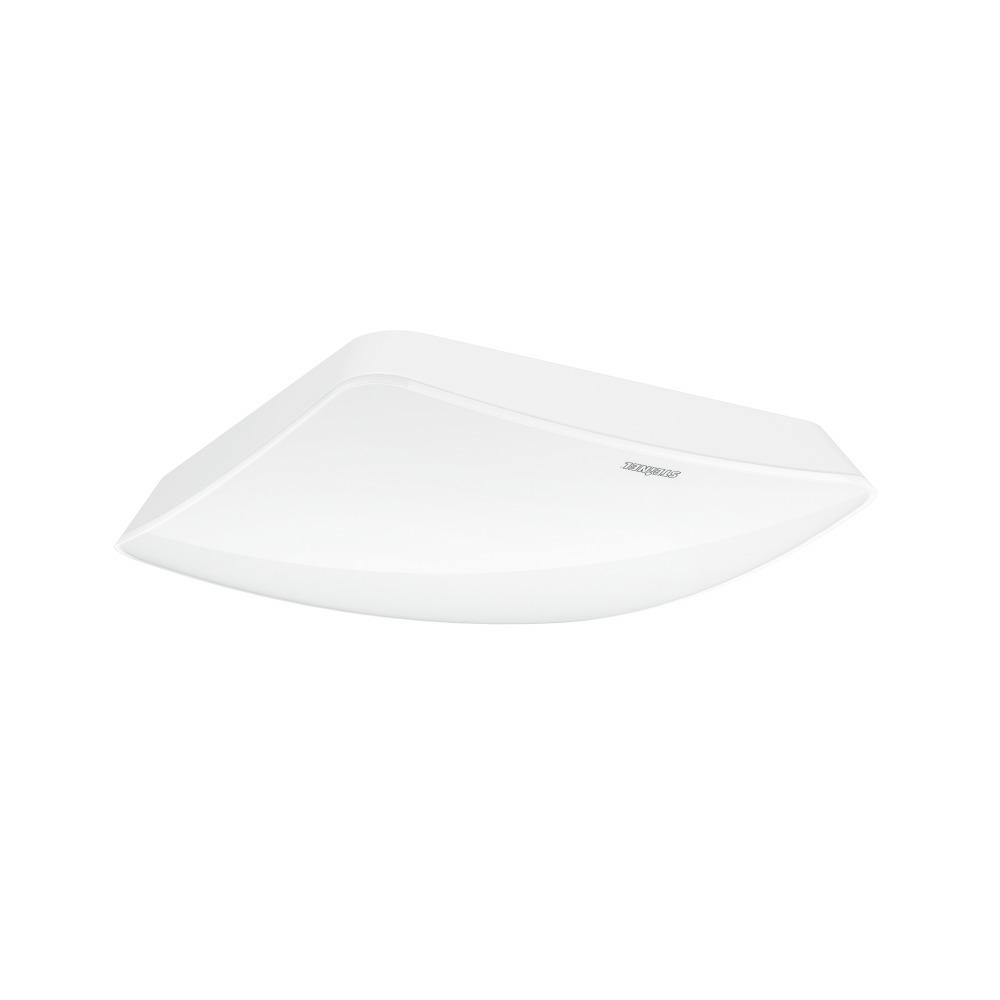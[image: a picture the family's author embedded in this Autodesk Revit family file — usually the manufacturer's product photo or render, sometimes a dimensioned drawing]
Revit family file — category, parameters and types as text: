
# Revit family: truepresence_057947
name_source: partatom
category: Electrical Fixtures
revit_build: Autodesk Revit 2016 (Build: 20151007_0715(x64)
units: mm (PartAtom-declared; Revit-internal decimal feet)

## family parameters
Cut with Voids When Loaded = No
Host = Face
Maintain Annotation Orientation = No
Part Type = Normal
Room Calculation Point = No
Round Connector Dimension = Use Diameter
Shared = No

## types (1)
- True Presence
    Apparent Load = 0 VA
    Default Elevation = 1800 mm
    Description = Type: Presence detector; Dimensions (L x W x H): 50 x 103 x 103 mm; Mains power supply: 220 – 240 V / 50 – 60 Hz; Power consumption: 1 W; Sensor Technology: High frequency; Application, place: Indoors; Application, room: classroom, lecture hall, one-person office, open-plan office, high-bay warehouse, production facilities, conference room / meeting room, hotel room, care room, duty room, recreation room, dining hall / staff restaurant, changing room, kitchenette, sports hall, reception / lobby, WC / washroom, warehouse, Indoors; Installation site: ceiling; Installation: Concealed wiring; HF-system: 7,2 GHz; Electronic scalability: Yes; Mechanical scalability: No; Mounting height: 2 – 12 m; Optimum mounting height: 2,8 m; Detection angle: 360 °; Angle of aperture: 360 °; Sneak-by guard: Yes; Capability of masking out individual segments: No; Reach, radial: Ø 15 m (177 m²); Reach, tangential: Ø 15 m (177 m²); Reach, presence: Ø 15 m (177 m²); True Presence reach: Ø 9 m (64 m²); Twilight setting TEACH: Yes; Twilight setting: 2 – 1000 lx; Time setting: 30 sec – 30 min; Switching output 1, resistive: 2000 W; Switching output 1, number of LEDs / fluorescent lamps: 8 pcs.; Switching output 1, floating: No; Switching output 2, resistive: 230 W; Switching output 2, floating: Yes; Constant-lighting control: No; Basic light level function: No; Functions: Group parameterisation, Semi-/fully automatic, Lighting scenario, Manual ON / ON-OFF, Neighbouring-group function, Normal / test mode; Settings via: Bluetooth; With remote control: No; Interconnection: Yes; IP-rating: IP20; Material: Plastic; Ambient temperature: -20 – 50 °C; Colour: white; Colour, RAL: 9003; Manufacturer's Warranty: 5 years; Version: COM2 - Concealed wiring; PU1, EAN: 4007841057947
    Height = 0 mm  [stored 0 ft]
    Length = 200 mm
    Manufacturer = Steinel
    ModVariant = No
    Model = 057947
    Number of Poles = 1
    OnlyDefault = No
    Power Factor = 1
    Product Name = True Presence
    Product group = Presence detector
    ProductGroupID = 4
    RLX_Detail_Level = 1
    RLX_LegendID = 5.1
    RlxData = Q
eAHUvXeUVNW7rtuAICAioiiCICINSM6hq1YVOWdQSUKD5JxDEyRIzjlKTgYEFFDsqi5EzAqI
OWPO6acoRs73zHrnPrXHPfeO+88Z4xzGfvp9v7e+NddccwW6W/Zv5Uq7fDnN/lz+1wnW/cnv
jell++PLWzt4l9yG7TxpabOiRsI63Be34eXLX+e5Pq3p6JH9h47qN2Ho6FHtJo40N3TcwPz5
8rLpjd3SxqVNTBuYViatk7mBaeONUWn3uKRiWo20umn10xqm1bGvZdJuT2tkozfQHFInmcey
y5e/y1Mord3QwUMmNB85dMKEgePSyuRiHwXHpfVLG5DW97+NxkgN/5cj5baRvs5zRVr7geOH
5CrsRnD7zfhfdOdKu0LpT3bw/3/+/O/pu9btevSYtLQT5kblSkt7sGTb4M2JFYNres+IPfJc
+yBP8f3hVdWmxa6JNgvy/5URzBkyO3bLu8WDtAcLBZ+NWBnbsf2b8Jjpd4Xe+2RTrPWST8Jd
ap0MN3hlc+zuVtvD/Rp0Du+ptDNWoPyU8MuzJ4Ue3bI7VrfevHDZnz4PTcm/O/bzbx2CudXb
ZDSvmxVberxDMDXXdbHqw7Jiyz5oH+R03RHbePM0v684+/rA5vb2xIrxL3rN8POJMx/tN5ay
3xj71b6y2ZfmkM0cut8zJpyWdqFcwbd2x76MhLJfHf96Rt6Xkz6t4blY3YxNsXfDj8UuNW8f
H7toQqxho5viN990dTxfh5WxvlUrxsefbhOvv2YSc4jbmrg5vPhZg3ixm5rHf7phWmxSv9Xh
gYfax0vVnhB7bGi9oPTyFvEGP0+N9alaMehv2zazbasNuRgqOrZDvNba8bGVdQtkP7q5Q/zS
2PGx1X99Gtv22VOxm/Zsjr25ZUesY+SOWKEiO2PXfj0vNqjXd9nP/70r9snDU2LHPpuZvWmD
O5bY7HV50jkW5SFy9Yfo1zhhxuF4OWeVeq33+wqzLx1jwDFu/ntVbM3h9kF6rQn+GN15t/nH
u55uE3Sy+U9fVy/ecVKL4K88WbEHC/6S/e3YDsHsNeNjJYdeE+q/uUMQHjc+1nXA0XCJJu2D
LUsnsG7BJNu2jm377BsNghVlmwezrpkWs+stbtdbXNdb3K63GNebXQ9xux7CXA+cE66xL57a
GnvP+u0aCL60a8Cun7hdP09y/dg1E7drJsw189dP7eIzHt0f7ll0eOzfJ9vG3zi6L3y4a9dY
rnlt4tUe3xvOuy4UG/RHu/i+LadvI7/vqbbOk1//dZv4uBYfxsjvOto6Hvz6foz83n9b2Tjl
4+QPv9zSxkmPk387uml86t56Ll/aokl81Yq6LifjM/rJ+Ix+xmAscsZgLHL2yb7J2Sf7Jh9d
NM9u5kqOZ67qD6f0h32/jR+kjB/48W0+Qcp8Aj8fy4KU+Qd+/jZGkHK8gT9e22eQsj6BXx+b
YxCbsGYP87Q5Bt0bHt3DPNXv1t/mSL9bf40f0G9zZPyAfs3H5TZH5uNyzd/lZHxGv47X5YzB
WCnr43L2yb7JbQ3LMVf2W/Ct28oxV/W7uZJr/f34nC8/PufL5Tq/Ltf5dTlrzFwZhzX28/9k
c4v48hPlAttn7N2Hm8Rv+rSm861qdnDXHtfq+VLt4vs3fhTDd63Rxq7hCnF8m03N4v2y6zuP
UpPzOX14tmN7PNcJ4yoP+9z6A99v4wR+HNPAj2+fB36/tl3g52PjufPLmMrd/aX+gFzjOK/x
ndd+nbfxmI/z3H+Mq3m6cfE6LpfreJ1nvoxLT7uGGfEVm8NuDb9+qHr81MtNnbc1jv+yuYXz
78zeHvuhb2vnq0zunFF0URvnL258MDwhlMwX2DkJq/+tj2oGjz3SxPV8uCIcnGmW4XzBc02D
s3uqO/+P9a7QebwUbhVkHP02zDktMr11ML/uBuc/WNgmeKBa7yfJv+rXOnh7yHautdixhq2C
yvO+c77GipbB9DcLxMkr1WsZvHfiOuf/k79lcPDR4s7X+E+L4PcaJZ3/450WwWfvlnL+a5sD
x8m2J6Y3CS41qOX80kYZwRtrws7f+WX14NThps5z3X1s1x/9E2/5Ovxmy1bO3z9+VXjx8tbO
ZxS5Nvt2ez7SUyw4HOtSIZnb+sSbatvBsZrxwqeauJ6nh4bjy0ZmOH/piabxwm9Wd/775HXu
/Hc9W8UXLvnMHe8/+1rHP5+7yPmp09rE830zJ8S+Fv7VKj7ln+ww/us/5sfGFV7wX77/owtd
/7vhBeFBHy34L+97+ObFvmVJyy3wfEcHeL7HwqN5BT6fwF8pj/KdIdsVMPgM8AXl0avk0UIC
f7U8Wlj+GlM/Dr6IapT9AZ7vwvBoUXGdMnL89QJPDzXKNni0mMAzLjXKvoH5+h78DarRGwW+
uDx6k8CXMPicbUsKPMdLjd4sSikjL22wHeBvMdhfGcPPB3+rarSsPOqPHX+barScSFdGH768
arSCPFpR4G+XRyvJo5UFvoo8WlXgqymvburHxNdQjdaUR7kGAV9LHq0tuH59D9epHxPPtUqN
+nXA51eNco3UMeoa/nzh/TnF11ONlhH4+vIo6w541hrwrDXg/ZrjWWvAs9aAZ30Bz/oCnv3h
UdYX8PxkhkdZX+bLz1h8BvwExWdoSJ4ab9/Iu8/QQOAj8ig/YgG+kTzaWOCbyKNNBb6ZPNpc
4FvIoy0FvpU82lrg28ijbQW+nTzaXuA7yKMdBb6TPNpZ4LvIo10Fvps8eofA3ymP3iXw3eXR
HgLfUx7tJfC95dG7Bb6PPNpX4DPl0X4C318evUfgB8ijAwV+kDw6WOCHyKNDBX6YPDpc4EfI
oyMFfpQ8Olrgx8ijYwV+nDw63uBa5drlGgX8BHmUaxTwXJd8zjVPDXjuAzw6UeDryKOTBH6y
PMq1C3iuVz6/STUZvoRqdIrAF5dHpwp8ljzKNQ14rmM+v0E1GZ4c8NMEnuc/NVpaHuW6B3xJ
eZTrHvDT5dEZAs/fN9TozQa9eN9HNlPgC8uj9wo8f39To7MEfrY8eqfAdzf4nO8BqAFfUB6d
I/AF5NFc8uhcgecPNX/uE/h58mgfgc80+JPboAY8f7/g0fkCX0seXSDwC+VR7jHAc1/xOX9/
UQOeHPCLBL6GPMrfi3yGDhH4yvLoMIFfLI8uEfiq8mg1g1687yNbKvBV5NFlAt9AHuW+Bfw4
g/t2uTFW4Ln30RXy1PiR0pXy1Pjh0lXy1Pih0tXy1Pg1qlH/HMOvVY0OFPh18qh/TuLXq0b7
CfwGebSvwG+URzfJo3cL/GZ5tJfAb5FHt8qjPQT+fnl0mzx6l8Bvl0d3iJ3K6MPvUo3uFnuU
0YO/Q7pXnhrfVbpPnhrfWbpfnhp/QDXaUeAfkEfbC/yD8uhD8mhbgX9YHm0t8Afl0ZYC/4g8
2lzgD8mjTQX+sDx6RB5tLPCPyqNRgX9MHg0E/qg8yr0B+HHGGGOUsUzglyobIU+NXyIdJs/9
z/NikZFpzDPmGzxn+hsLBJ4czZTnedfbuE/g5xrdjdnGHIOsp0EOeHKUPjzP7m7GLIG/10C7
yFPjZ0o7yVPjZ0g7yLczbWNMM5oZk40pRiujhTFV4MlR+vARY4Ix0WhiNDImCTw5Sh/+qHHM
4FwAfqU8Ol7glwv8CoNtOb9sA/jj8ujjAs81TY1yrdP7qMFngOfawqOHDa7HR+Sp8VzTePRh
edSPg+c+oUb9/rjv/HzwPEeoUZ4v3K88N/gM8NvkUfr2GbsNegG/Sx7l+UIPzwo+A/weg892
GH5bPPtg3zz3/NzwT6hG/driV6tGVxn08vzkM8DznMWjG+XRtQK/QR5dL9Ypo2+NwRiA9/vj
vDOf14zUP6eeacnllJZz/bTELw/XiqStqpw9pOj0RLPRlSIvTqwcCw+bnrglLY/rmf35jES5
h88F55dVzn7swZmJvpWfDF6vVTlW9PuZiW8mpkeeXFk5e+2u6Ymp09JdP/7XtZUi53amhRnn
pkdtfPvD+P98Vj8yaulDoT1vTEuU+CN3ZN2KytmM/0z8XEAP46/qnB0cWFo5xPiVDu1w+R91
701c9595zh8af2+C3uSf5H8x9D671LLYqnW149HH7018u6l09oYtO+JsW+yefg3rFPwt3j19
ZuLzMz9m31W4eM6DFWYkvsz3b+ixNuk5zPlM2YoNhzxTKYc5F3q1dHjK8Fo5zHnW1zeGns0I
ckpumJb4q/Ct2Y+cTPb802ZfdrUjST8yq0b2OzOa5Jy9c1qiYfOy2bufapnD2n689frsz/O0
z/n2XFbi9NRS2Uf/uejmsLFcx4b5DyXn1nbP3PDTfeu6OV937UPh8r9Wcf7tNX3ChU82CDiW
2Y8/FX7g9NSAY+/75ZHQinY7gpTjCjguHUuEY3nzpcOhJY9UinAsNxwoHxows0mEuT1wYmeo
Q9UgwrFkF08PdZ2U7vo35jv7xGQ7f2yr43Lbak2c/7rt1bE6WbUirMnrX/SPvXpr0o/Z0zD0
0qWLbg6T/t6TndkzObd9r0yINRs8x835iVe/zj7+RMQdy9FnWub8dHptQ7c++2vl9M0eG2LM
4EitnNE9l2bgz80umvPkxtrhl3rMSKwvUTznruFnQpyvUQOy4w9/d2UG10bT5jviA3s/EWId
3li5I35mWHPn9zyyIz6i3NkT5OrJTulxfk337Hj3tQXcNXbXLWVyrtu3Jjv9nemJostuzPlq
1eAY+2p/uFbOxRdedPPJfKt+zo/9Pszmuv0pX/uc5fvrZ3BOGxnV0q8IDg9qE6mxICtxpnih
YOr+jpEv92YlRpaeE07xMecHZyU+a5g33qVll8gfp4clrt+wO6dUkwmR5u9XS4zZWC3R7Oy8
yORX9uQ8snxYgnzvmeviT/TNStB/rtSO2MqdWQnGaVl6aXj5nqQv/XPuoOTQZM/UJ3dF2nyb
3HbD/GrRYj8kxzy/Y1g0/6A9bl/LB2RFf+t7lZvDzbuzoteVXu/mduO+rOiah2e5ObcdlhXt
diAtYL93vDMsWqDs7gjz+fRytWh8QrUo81z97+7Id48Oi5IfOXB10OKerCj9u1fsDHfbmRVl
nqMfXhw7tSfp699YIP7qwGTPykW7c7o9l9z24/7VEoeure7G7Lh0WOL3d/e4fa05Mj7x/Fer
IllFvggu98hKfPrcvvArX3SL/LtoUqLGiinh9w8tijxddFri5yF/h3ienS+elbh0cWhsd7me
kbxVJiVCG+fE+jdbGmmwflqia7vLsV+2ZER+WZqVqNEvV5y5nf9rROLr0NGct3dcHVl8tmKi
7FNVErfsfSDy0ydVE+/OqZrofOvKyPz5+3Muvj488fW8uyJllxaJn35xWuLoHXUjaRcuxmqt
TK7/4T/Wxs6dmJIYsX9spP3vq2N3XzPZncdGleeEnvgl2X9k1dzQmYPJ/m8aLA1vLTYlsfWa
6ZHnP/44/MXaZL4lM1/QZXHSh79fE7lm3kg35jM/fx/+7efpidKflYgUmXJ/5P6v+iVmhI5H
rhuZHi30c8Q9dy98USlasWPlRK5S+yON3xsRff2L5HFdc2hatEDmVfF/LtWPvHF4UrTmiodi
4YELIyuDCdGLpdbHLpTcFDlUdFp018G0GGv4zU1Z0Ycm3hlmDVtUmRSdb9cDa3h03bRof7se
WMMuy7Kid5pnDRsXHxktse+xCGv44dcVowP2V4myhiVurhad2bpqlDV8qdH+yPNPDo8y5tBv
iwTLXpwWZQ1PdP49/NaK5LUxoMmG8OQTU6Ks4fFmm8JDCk9218NN/WZm5/yS7K+/dlr2uweT
/SdWLY69XWxKlDW8csyFWMN1yfzU/rzxY4uT/o4X1+TMWDzSjTny3Nex7/8zPcoa3nLP/TkN
H+4fLTDl0Ui4bfnEsg1BtHrhGpH46UqJ6mMrR1nDHTkjEjOmH3PHdXJBJJF/1Q3R5gV2Rd7N
qp04/mPtaIeCvwVHv70yUfrHltF6/Q5Ebh2wP+fCt2OiXx0/HPzYYnLOn63HRp8eMyIy/eu/
Y7lWTo3O+bdfZEn9GbEr8s1wcxg8NhKbFM2Kcl3d+NzicMWrpkVZ/+ub7g7//tL0aK8aZSI3
1CkYHHx9avTvU70jS19eHlnVfpQ7loo99ke23TE6yppPnXZD9PmNETe3VTfVib7bKTm3Xq+2
jGY/eqU7F9vzj40OvnF/pE3fh4LOM8ZGf75lQoS5fXMoK9rdzmOTK9tHSrTLin574Vt3fz3X
YEZ0s533F9cXi3RqlBU9u6pymHnOKjQtuvbhWe46OZPbjsOeG6ynnhXueVL9wazon/ZsYcwN
C7Kil8xznQyabfu68Qbn7TvvqP/bu3cfu5Ys57mx+MmR0VxrV+dwDZz5aFR0aMH9OYz/1bpI
9I45Nyay6m+L9NxRO9ryxdoJ1v+tr/NH75/X0l3zv2/dF5n275hE/cLHg8tPT4nMrDk2wTHm
e6ZAUPShrATzmZ/7vfCg8cnn5Nc7V4W7dZyRyP6xaGTJiPTw/PlTE49sGRApm39VrPZL0xLc
L+MOrYm9sCH5fU3dn/LHK/05NcE1/GDmspwX5o5y9+YjJ/fnDOk9OpHvj4KR0S8US5wvF01w
nVT+tXai/6TkPLs2bJnYcTF/guuk/3tjEjMG789hntszxibq1JuSwzwHjMtKNF37UYx1eGDW
jMQNh+36tvMbOzUlUTeaN8aaLK8wPfH89LlhrtV1z05NnD16MPxzZl/3vZW+/4nmMpPbyGNc
YeQ18okrTfOLAqYFjauMQsbVRmHjGqOIuNa0qLjOFK43ihk3GDcaxY2bjBJGSeNmo5RR2rhF
lDG91Shr3Gb4MRkfyhnpRnmjglHRuN2oZFQ2qoiqptWM6kYNo6ZRy6ht1DHqGoxXz6hvNDAa
GhlGyAgLvolk0bgIGxmNjSZGU4OfyZobLURL01aitSm0EW1NoZ1obwodREdT6CQ6m0IX0dUU
uok7TOFOcZcpdBc9TKGn6GUKvcXdptBH9DWFTNHPFPqLe0wHGAONQYY/vsHmhxhDjWHGcMMf
IzrCGGmMMkYbHK8/VnSMMdYYZ4w3JhgTjUlisilrMMWYamQZ04zpxgxjppG6DqzHvcYsY7Yx
x5hr3GfMM+Ybfk3QBcZCY5Gx2GB9/NqgS4ylxjJjubHCWGmsEqtNM401xlpjnbHe2GBsNDYZ
rB1sNrYYW437jW1GprHd2GHsNHYZu409Bvvfa+wz9hsHjAeMB42HDM7vw8ZB4xHjkHHYOGI8
ajwmjpoeM46Lx02fME4YTxrZRsyIGzkG650wThpPGaeMp43TxjMG5+1Z4znjeeMF40XjJeNl
o60x3HjFOGOcNc4ZrxotjVaGv664xiDT4FpMvUbxHCOkXtt4zjn4+4F7A5h7J6O9wbUG+DYG
8wL8+f+LqZfLnoG57RofNinj6kXZQVqhjQ1XXr8qyDxaOfTGi6eD50d1D9+282BwoMtj4X+u
6x28PSo7/En3DcGUw/+GoxNmBzdfLBKcT+sTHO1TKKjaa3hgS5G29qnOQdqBaQ3GvX97kLZi
WcNin/4drr+8QYTtTx/pEKHeMbZxpPxnc8OMj7L/SwuLh8vm7hBBn2zdLjL64tYQ+7s97wdh
9vd+2xLBjLLVI2jz7EoRv9/K79R081hQOxr89HHRoIr9G8CsQz2DD8N3OM357eXwo23XBg8/
s79h2VuOBpP+mRNevCY7uMP2+c3mFwL2s+uHp4NyVxUPzXw2b/DKoUENOX7yw1tOh0qXzBUq
UrFkmP7H29SwcSo0WLH6Lnes9abtCE61ey+8cu+KoHanm4L+lxYGP19bM7i0en5Q76FIsHbB
PDcf6rKL+rjPh5QdETzSrniE+fWaXjBCfTr9ykjn32e7/NFfdwafTPwn+PvZDcFvr34dnH33
YJDrr/yRN8qfCard+XrAeVl+9ydB94MvB0Uqvhe8Nf/FoP3O6yJ15p0JZk8pFamy+Uxw/tma
kdu/fyVgnTl/V7VoHqG/x6jWkWs/eiFgfRnnyOL6Ec4n68r5/OhC5Qjnsd/n5wLOw4aVZ4Nx
N/wWZr+sB/Nh/XIVPxt8cdd4N0+O/3itXMnza8fBOnBcrEORQ1dFWIdTdQrZvDoEB5dsCbgO
WC+Ol/XjOG9854wbj/PD8bJ/rsfHr3rFKeeJ+S69dCZ4ZlzboOT8s8HgfiuCP6tUj7ySb1Po
q+I1IrtvOxF6uVHzSKvTa0Pj/qgeKb3/q9C/71SPtC9WKPxq2ZKuRqkfO/ZvwOfrC1wOqEt9
+4mrfx7yqat3/fKuq/8z7T1Xv7vidVfvL/uGq39rfsppyzOnXP7ym086vdT9SZfXLbTd1V2e
2ObqpZc6uBplf72PJMLs/6u0p8LU+Qvf6uoDf5dzdeaeUyE+bzTjpRCfnzzbwNWZt7d1dfmJ
yf1P+ie5/7/yZrvxKyxM7n9gKLn/OV8m9//dnR3d5yjj3TzqZHJ/8eT+Zy0o6+qKk8q7/Xfa
8ExyfzefSe7/WCRZX9PZ1bu2tnLrOPTTVm5dH/6ymdNTB5q5PDN3fVePfrtesi8juf5DTdn/
p58l1//ZBsn1b1fiUze/MhuT6/9q2fdcXfah5Pq/fCK5/m91Tq7/AwuS+z//UnL/jbo0i9i/
4wpnb2nptFGXcpHQg5tDnG+ui9+7l4iU/ndz6PpoPne9nOv3b0D+UIFPAq6XViM/cfV1g951
+ulzbwcVdiwK3fTiC67m+qPmOcH19vkTrzk9+/tr7vM3ez3tlOfK1tq7Qju6Zbv6zoHbnfL8
iZTdF+L8s1+eH+NGHgjxPFlx0wH33Pmy1P7QuX45YT7PvKWUU547jMdzKK3LllCnW54Muc/t
+cR8Ms+kuzrvkuT+697+jJvnyC+z3XGdm5ucR6sVyXk8l1jh5r3v+gkB68P1wHj3VW8XsD4/
rfg9zPGtLJ1w+780rWSY9bmwsbSrx+TE3P7GvLfL7b9Lv3ZufXmeMB+eL4d6bgplVr8t5NTm
yfirK7R2fTyHOJ715Zu7ukuV+k55XrE+XB/08xxjfXiusT48/1ifU0uS523K1uT54jnIeDwH
WZ8m65Lnj+cV87lc/nV3fBuLJvd/+OPWbp5L27Rx18m4O94JuG5KbvvQ6cVinzmd3OZK93mZ
Qjcnr6elNZw2GJy8zo4eTl5nX/ROjjPL5so4F7b/4/T5AZX4t4Th5/991Gm9J/O4cU881yW5
v/krnB54aZfTk+sedrpg8RGn315x1Gms2TGn8zYdd9q14JNOQ8+ddPrIxWecZp7Z6/a78tgl
pw2K3e72W/Hlo067Ncvn+u4p0t3pr8vXOL3tvRNOb+2RHG/+keR4ra9NrssvPZLr8swXn7q+
tLL/OB3+cwG3HgNCtzjNt7uW0xv+eim4t/36YHF4UbCp6KIg7aUXg18eOhGwn3NbXgwOvfZ8
8E3kZGD//jZYtvWZ4J8uiaBwrReC6+IvB1l/93HbjQ0KBiu7XxW021cwYL6ji87NYP6/1t+Z
8UeHl4N1rxcIxj78UnBm7xNhxn9hbIXw5V4v8PdUiPm/uWRniOOpMCgIsd9yGy5ncLwDuz6S
wXq89s4LGWnN385Y/djh8MlVj2U888I/YdaLvlkF/sgoP2Z4eFbwfUb1JYvCrOfArtVCO47k
DbGftKdzhRpcahLOHJ8Wum9b+zDrfqHqytCsT1qGChf7NHSy5b8ZBe+/K2zf92T0vb2tOw7W
4fCRtsGta14Obu+9ImCN0nYfyhhbclnAPN5tsCtgfNaJebBOF76uFVpeOhGcnLAmdHTs6SDt
r69C9+55PhjQ/5dwr29te/tj37q5n7nt2zfn85gC+RXyaF6BzyfwV8qj+Q22K2DwGeALyqNX
GYWMq43CxjUGWRHV15oWNcivM/w4+OsNti1m3GCwT7Ib5dHi4iZl9OBLCDw91Cjb4NGSAs+4
1Cj7Bubke/A3q0ZLCXxpefQWgS9j8Dnb3irwZeXR20Q5ZfSlG2wH+PIG+6tg+PngK6pGb5dH
/bHjK6lGK4sqyujDVzWqGdWNGvJoTYGvJY/WlkfrCHxdebSewNdX3sDUj4lvqBrNkEdDAh+W
R7mAIaKMvqjhx8Q3Uo1yTIBvbHC8XLNcI02MpkYzgW8u8C3k0ZYC30oebS3wbQSen/EA385g
3fkZkLUGPGsO+A4Ga0w/69vRIO8kj3Y2WGPm0EV1V9NuBvO9w+AzuNOg5y6ju9FD4HvKo70E
vrc8erfA95FH+wp8pjzaT+D7y6P3CPwAeXSgMcgYbAyRR4cK/DB5dLjAj5BHRwr8KHl0tMCP
kUfHCvw4eXS8wE+QRycak4zJxhR5dKrAZ8mj0wR+ujw6Q+BnyqP3CvwseXS2wM+RR+cK/H3y
6DxjvrHAWCiPLhL4xfLoEoFfKo8uE/jl8ugKgV8pj64S+NXy6BqBXyuPrjPWGxuMjfLoJoNr
dbPRXeC3yKM9BZ7rks+3GtSAv18e3Sbw2+XRHQK/Ux7NFHiuVz7fZVDvNvYYe1XvM91vHFD2
gDz6oMA/JI8OEfhhBp8/bFADnhzwBwX+EXn0kDw6QuAPy6OjBP6IPPqowD8mjx416MX7PrJj
An9cHn3ceMI4YTwpj2YLfEwenSLwWQafxw1qwOfIowmBPymPPiWPnhL4p+XR0wL/jDw6S+C5
f/j8WYP6OeN54wXVL5q+ZLys7BV59IzAn5VHuccAv9jg83OqyfDkgH9V4M/Lo6/Jo0sF/nV5
dLnAvyGPvinwb8mjbxv04n0f2TsC/648+p7xvvGB0UMe3SDwG41NxocG9/Q64yNjjfSCPDV+
lfRjeWr8Cukn8tT4ZdJP5anxn6lGlwj85/LoIoH/Qh6dL/BfGvOMr4y5Av+1PDpb4L+RR7+V
R+8V+O/k0RkC/708+oM8Ok3gf5RHf5JHpwr8z/Lof8QvyujD/6oavSh+U0YPfpL0d/mJppeM
8dI/5KnxY6V/ylPj/1KNjhb4v+XRkQL/jzz6rzw6XOAvy6NDBZ4fNKjRQSaAz2UMNJvb9B5T
wOdRjfazDPBXqEbzyqN97XPA51ON3m0Z4K9UjfayDPD5VaM9LAM898haY7XxnsC/o2ylPDX+
TSn3N577n+fFqwbPrGeMlwyeMwuMMwL/snGfQR89s4yZxmmBP2VkGTEjYZBNN8gBT47Sh59i
TDayBf4JY4Ixznhc4I8pGyNPjX9UOkp+hOkw46DR39hp7DeGGIONBwX+gDHAoI+e3sYWY5uR
afQxdgg8OUofvoCdh4LGVQJfSB69WuDtfwTDgb/GYNsiBtsA/lp5tKjAXyePXm/QW8zgM8Df
II/eaBQ3bpKnxpdQjZaUR/04+JtVo35/pcz7+eBLq0ZvMcoYtxp8Bviy8ih9txnlDHoBny6P
ljfoqWDwGeArGnx2u+G3xbMP9l3J8HPDV1aN+rXFV1GNVjXorWbwGeCry6M15NGaAl9LHq0t
6iijr67hx8T7/XHemQ9/JO5esbvpv/6twv/8LPnvQnK77uT3Jr4vj7ZPfjYrivos5PqT411h
ns+uVEaPz/CMR53X8J+R4X0WNu/78pnz/WT0+CygTeOxPz67hsgyenyGJ6POb1A3Mnyfz6LK
WKcCBv1PKmMOPqOfbakLGtQnDDL6fMbnZNRXGdQ8W3yfz/icjLqQ4ft9n8+upk19ePqPE1lG
j8/wZNSFDeojhu/zWZmUjHWj/yZlHIfP6Gdb6iIGdXGDjD6f+bVn3ch8P33U1yq/0ZSMPp+h
ZGhRAy1m+D6foWTodQZ6veH7fIaSoXzu1ff5rJF95scjA79f5uDrG8zT5+dF7Y8jtaei+jhe
xqHHrxXrQUbt15lzQ0ZdwmAfZIxPfYtBRo/PSirzc6C+WZnfJ1l6Sh/7pGenMj8vslLK/Lyo
S6f0MTeyJsroY270bFXm50+2WRnHwTw4hjIGx8GcfXabMq4nsjLGrQZ9ZMyN+pBBRo/Pyirz
86d+WBl9zJfsYErG3NjnfmXMxWfllFEzX+q9yujz2R5lrF8ZgzVuZvhzVMYcWXmDrIx95Rio
Wxi+z2cVlFEzX+qWyjiXPvPXFdcaGfXtBuNRc1zUrQwy+nxWSRk1x0XdWhl9PqusjJpjoG6j
jD6fVVHmj5O6bUofx0pWVRk1x0XdThnj+ayaMmqOi7q6Mvp8FlFGH8dKT3tlfj3Iaiijh2Ol
7qiMPp/VVEbNsVLXUkafz+oqo4/joqezMnp8VluZP3bqOil9HD/ZG8ro41jpeUsZPT57XRn7
4LiYx1llzM9n9ZRRc6zUryijz2f1lVFzrNQvK6PPZw2U5VFG3TAlo5csrMyvGz0vKGNb1oks
Qxk1x099Whl9Pgspy62M+pSyvKbsl30GyvIpo/bXBhnXDHXU4F7Ib1/JqBsZZKw569nYWGuQ
8QzzWZOUjF76Ninj3qePnqbKqFl36i7K6PNZM2VllFE3V0YP54K6g7Iypj5roYxnBBl1S2Vl
lVG3UnabMmp/n3NPsy11G4Pj5f4lo25rkJW3r2TU7Qwy7jcyan+/cW+RUfs5k3Es1B0NtuWe
IaPuZJBRc/1QdzV8n8/8vcX9QUb9jkEf68w1xRqvNvx4PluVknGdMf4yZYzls27KqLnOqFP7
fHaH+qi59qhXKGM8n92pzF+f1Hel9HGNkvFzCnOmj2uUnpUGmb+Oybor89cxdQ9l9HEtk/Gz
E9vS18igJ6LMX+9kPQ36GtnXxgZ1L4OMPp/x85rv4/qmJ6yMHp/1Nk8fNdc89d0GGX0+42dA
38c1T89GIuujx2d9lPn7grqvMvq4N8j4OZRt6eM+oCdDGT0+yzRPn79XqPsRWUYf90umwc9w
vo/7hZ4Gyvw9RdbfoM/fU9T3KKOP+4qMn5F9H/cVPTsMMn/vkQ1Q5u896oHK6OP+I+Pnd7al
j/uPHv6tIpm/R8kGEVnm71Hqwcro4z4l4+dB38d9Ss8BItvW38tkQ5T5e5l6qDL6uJ/J+H0C
29LH/UwPP3+S+XuebBiRZfRwP1MPN3yfz/jdk+/jHqeHn3fJ6PHZCCLLqLnHqUcavs9nV2hb
+rjH6eHnZfro8dkoIsuoucepRxu+z2e5tS193M/08HM7ffT4bAyRZf45QD1WGX3c465H29LH
/UzPMYNt/XOAbJwy/xygHq+MPu5xsj+U0cc9Tg+/Y2A8/xwgm0BkmX8OUE9URh/3Pdlvyujj
HqeH3y2wLT0+m0RkmX8OUE9WRh/3PdkvyujjfqaH36uwLT0+m0JkmX8OUE9VRh/3PdnPyujL
NOg5abAtPZkGWZZBlmlf+xnU0wzf57MflGWacj/Tw++C6KPHZ9OJLPPPAeoZyujjHif7Thl9
3M/08HsltvXPAbKZRJb55wD1vcro4x4n+0YZfdzP9DyvzD8HyGYp888B6tnK6OMen2V8ZbBf
+rif6eF3YGT+OUA2h8gyerifqecavs9nXyijj3ucnnPK/HOA7D5l/jlAPS+lj/ue7FNl9HGP
08Pv69gvPT6bT2SZfw5QL1BGH/c92cfK6OMep4ff6bEtPT5bSGSZfw5QL1JGH/c92UfK6ON+
poffD7ItPT5bTGQZNfcz9RLD9/nsA2X0cT/T854y/xwgW6rMPweoG2u/9HGPk71vsI969jVk
LDOWGz7jHqdeRWR99PhshbKwMuqVyiLKqEPab0NljLXaYLy69pXxqNcYPuM5Qr2WyPro8Zkf
r44yetYZ9JHxHKFeb5Cxnc8CzYU+ni30bDLoo8dnG5Q1UUa9MSWjl8x/79PMPNvSU1/7uEkZ
42822EcJ+0of9RbDZzyrqLcSWR89PvPjFVdGz/0GfWRTDeptBhnb+ayh5kIfzzR6dhr00eOz
7cpaKaPekZLRS+a/92ljnm13GLsMxrvBvpIxfmpGL/Vuw/dNU71HGT0+89+/3KKMnr3qK62M
el9K1k71fmXUjEePH6+keXJ6DhjMhayDQf2A4bPpqg8qo8dnDyqj5tlM/ZAy+nzmv88pZRm9
9PjxyOgje9hgvzfbVzLqRwyfzVR9SBk9PuN3/PQVVkbPYSJl96o+ooztfMZ/K6DvamX0PEqk
bJY56scMMrabZZDx3xx832xz9Bwnsr5Z9tVnR4ksu1MZ9TEiZbPMkfnvkbqbZ1t6+O8V9F1l
X8kY/3GDrKB9JaN+wvDZHNUnlNHjMz9eAWX0PKk+dkUfdXZKxt9F1DFl9PiM/17DfvlKRk+c
Qtl9qnOU0eMz/juP75tnjp6niGxbenyWUNZHGfXJlIxeMv89UqZ5tj1p8N+vGC+3fSVj/FMG
WW37Skb9tOGz+apPK6PHZ368WsroeUZ9ZPxdSf2sMrbzGf/NjH3Qx9+L9LxgkNHjs+eUDVBG
/XxKRi+Z/x5pkHm2pedFg/Fq2lcyxk/N6KV+yfB9i1S/rIwen5XTnGsoo+cV9VVXRn0mJRui
+qwyasajx49X2Tw5PecM5kI2zKB+1fDZYtVvKKPHZ+eVUS8xqF9TRp/P/PdDVS2jlx4/Hhl9
ZK8b7LeafSWjftPw2VLVbymjx2dltVZVlNHztvrIlql+Rxnb+ayMtm2gjJ531Uc2RvV7yqjZ
lh7/vRR94wx6+O+6zHm8fV1uvG80UTY2JfvAPH2jlVF/SGQZ260wqJtqW/p89pF5+kYqo75g
kNGz0rhg+G3p89nH5ukbroz6EyLL6FllUI/Ufunz2afm6RuqjPozIsvoWW1Q36Nt6fPZ5+bp
o15jUI9I6fPZF5bTN9i+klF/aZBRrzWoh2tb+nz2lXn6Biqj/prIMnrWGdTDtC19PvvGPH33
KKP+lsgyetYb1H5b+nz2nXn6+imj/p7IMno2GNRDtV/6fPaDefr6KqP+kcgyejYa1EO0LX0+
+8k8fdSbDOpBKX0++9ly+u62r2TU/zHIqDcb1AO1LX0++8U8fb2UUf9KZBk9WwzqAdqWPp9d
NE8f9VaDum9Kn89+s5y+HvaVjPp3g4z6foO6m7alz2eXzNNHvc2gviulz2d/WE7fXfaVjPpP
g4x6u0F9p7alz2d/maePeodB3Selz2d/W04f9U6D+u6UPp/9Yzl91LsM6p4pfT7713L6qHcb
1D1S+nx22XL6qPcY1L1T+nyWpuwO9VHnUkbPXoPab0ufz/zvlroqo86jbenZZ1D3Ukafz65Q
1lkZdV5l9Ow3qLun9PksnzLqAwb1HSl9PvO/m+uoPmr+TRjrQs8DBnUXZfT5zP+esL0y6uS/
S5kVpedBg7qVtqXPZ1cpo37IoO6c0ucz/7vNtuqj5t9CMT96HjaoOymjz2f+96ytlVFfoz56
DhrUHZTR5zP/O9+WyqivVR89jxjU7ZXR5zP/++fmyqj590/MmZ5DBnU7ZfT5zP8uvKky6mLq
o+ewQe23pc9nN6iP+ohB3VYZfT7zv79vrIyaf+PF/Oh51KBuo6xxSub/W0JUGTX/Boxt2e4x
g7q1Mvp85v+7RqCM+mb10XPUoG6mjD6f+f/G0kAZtf+eYZwyavcPoGwuoyxbZvC9hv9ehWyp
Qe1/PzRCGbX/fohsiUF9m8GxZdrX+Ua61RWV9bd6gcH3tf57ZTL6qH1fb6vvM263rJK2JZtr
UFdR1t3qOUZlq/3vd3uqj56q6iOjj9r3dbN6lsHPZP7nPLJ7DWr/+/Euyqj9z5JkMw1q/3v5
Tsqo/c+rZDMMav9zcjOrpxj8viPDYK1a2NepBr938L/LIKOP2vdFrJ5o8LuhiLZtZPUkI2y1
/70PGX3Uvo/r4pjB+fbXC9eBzxppvJXKqEcqo4+crLGy8cqomyhbroy6qTKuU/bBPpunZMct
o/bXPT0+a6E+6scN6pbK6PNZP2U8E+mlp3NKRh+Zf57yjCWj7qK+R61mW+bh71/uaTJq/zw4
rIy6o7bl2UTOs8U/13jWkVH75yTPTjJqvy0Z+6DuZHAd8Hwmo/bHwd8pzJn5dlXf/VaTU/vv
QcjoI+umvq3KqP33Q9st4+84/m7roz4yxiPz35dsU0bt97Hbsn0Gf3/6v3/JGI+sh8Fx7FJG
3VPZTmXUdytjW/5OZyz/vcAO9dHj58f3dRwbx5CpbcmeMKgHKKPHZ/7a4Hoho+6vvtXKqEek
ZPSS3aNsldVk1P5e2Kxt2edA9W1SRj1I2UZl1IOVrbWMnHpISsb8yIanZBsso2doSrbeMuph
ytZYzbZs548j1+XLf/xy+fJH9d7ixYffXt7+rcmfxl+XE/8SNVz+aYPlu6fw1f3f4i8rLv8r
8eflFX9eXvbn5Xv/taYW/1xOKe+9ePkjNufPL32dXP7RyfZ9X3fe03LNrqFZ17dcU6ZU2uJu
BbqUabP2k4pp1xc4v8v9cxObnfuzceG2Ro9tLt2YYmEysq//e14m+F/D/7+a/7nfm1N6WFW3
sinZf7f5rHy5CY/9vLNyFbYXLdr7IxtZFlJbfinyf9arFddPT/6q4mGb+7WfNYrXevP+8Iqe
9zfI2292zHD+rXYRy0sF5KZxq50/kR6KP9nqdufLbKodN5y3LG6fOb/w2ibxji9+ujtlzJh8
mH3gW375+G30Jce/P8w88JqP69Ec1OPm4Lz25bzm4Lzmpv77Y35MjoOxGJ/j4Hi0L/P3u31x
TGxPzjExLp5jYn94m2/QKKi8F886+bWq8vGxcnxGzni2X+dRv7bar3rcfJzX+M5rv85rPup3
6+N86ivbUl9Tdf7fJvGrVmwPr6lQJntN9WZx+59GuA3/Vd0m8RM5r8fwvTMbWc8tcfyzhUPx
E+eqOY9Sk/M5fXi2Y3u8/c8y7GZc5WGfW3/wX/3nqgV+HNPAj2+fB36/tl3g52PjBTXzV9nL
mMrd/NUfkGsc5208xnde+03mOa8zH+ftlZPlGFfzZP6+n+NK5snjdZ75Mi79m64L4iceqxH8
s3VXdu4bIvEGe2sGGz5+KduyuH3mcsvi9pnLP215a/zj8U1c3qlc2fjuGU1dPq/gW7GZHZq5
fFiNt2Mv9Gzucjsn5ba1b+HyJpkDy+3p3dL3h1P6w77fxg9Sxg/8+MwxZT6Bnw9ZyvwDP3/G
YCyOizFsrm6/7NPmGiZnnzbXMMfLHGMTrttLzhzt1X17ydUfS+mPkWv8eMr4cXLNx+XMkbUj
1/xdzhxZa3Idr8uZo83V5czR9u1y5mhzdTmvFLS5utzWdrfN1fez/r6f9ffjc778+HE/vs6v
y3V+Xb/Nn+vB5czRz58xOPc63jjnnvmzT8691ifOuSdnjrxWkJw5cm+Sr7FXs37acqdb/1/K
t7Bxdrn171anZTyWtjtcs/zF7GONW8UrfrA7PKjuNbFDWa3dOPjU19Wlvsau7/iW8XrT343R
k/qqu4qrmts4t8XJU1+Hl/qavDdKNIo3WFjb9aS+So+Mz9g29XV7jMe45Kmv5GP/zIM89bV9
nCOOgTz11X6pr/yzbcN+29TXAtq+Ar+v1FcHpr5S0OYZ+HmmvnbQssAfV+qrCW28wK9J6usL
U19rmPq6w9TXIKa+HjH1tYk298Cv/8AFzYJY2m1xzuP1g1sEne58J+bOacorF1NfxWhrE6w4
dXEP65P6usbU1zhqfHc9pL7qUccSsG3q6yBTXxOpdXA9qa+S1Lq5PPV1k1pzl6e+klLnyOWp
r63ct6VZOY6BOaS+2jL1lZe6NlxP6msxdS25PPXVmbr2XJ76ek3OM/NmX6mvLh1RPBp/Yn2t
gHU2jVvtPOeB80HOeeB84HkOPzC8lc/DPrf+wPcznh8H9ePr/LptdX7dPct4TTI/38P46o9r
PozjvMZ33ubDfp3nmWbb+5x5+n7m77yOy3nGo2Z8Pk+53uL+emM8nj/0/H+9ztK/wjL11ZbJ
717/n/9zQrntgzzGFQKfV+D57pg/Vxr+e2k83xVTowUEvqA8epVBbyGDzwB/tTxaWOCvEfgi
An+tQV9Rw4+D9/u4zryfA/561Wgxg+wGgxrwN8qjxQ36bjL8OPgSqlF/7PiSqlF+1qC3lMFn
gC8tj94i8GXk0VtFWWX03Wb4cfB+H5wL5lDOSDc4b4AvL4/6P/gKKlDOA+A5B4CvKI+y1oC/
XR5l/QFfSR715whfWTXqzyO+imrUn2t8VdUo5xLw1eRRzi/guZYAX10e5dwCvoY8yjkGfE15
lPMN+FryKNcA4GvLo/6awddRjXK9AL6uPMq1AHiuA8DXk0e5DgBfXx4tI/AN5FF/neAbqka5
bgCfIY/66w3PT7HUKNcT4MPyKNcY4LmeAR/Io1x/gI/IozwfAB+VR/0zBN9INeqfM/jGqtEm
At9UHuVXq4BvLo+2EPiW8mgrgW8tj7YR+LbyaDuBby+PdhD4jvJoJ4HvLI92Efiu8mg3gb9D
Hr1T4O+SR7sLfA95tKfA95JHewv83fJoH4HvK49mCnw/ebS/wN8jjw4Q+IHy6CCBHyyPDhH4
ofLoMIEfLo+OEPiR8ugogR8tj44R+LHy6DiBHy+PThD4ifLoJIFPl0cnC/wUeXSqwGfJo9MM
evG+j2y6wM+QR2cK/L3y6Cx5dLbAz5FH5wr8ffLoPIGfL48uEPiF8ugigV8sjy6RR5cK/DJ5
dLnAr5BHV8qjqwR+tTy6RuDXyqPrBH69PLpBbFRGH36TanSz2KKMHvxW1ej9Ar9NHu0t8D0N
tttu0Af4HfLoToHfJY/ulkf3CPxeeXSfwO+XRw/Iow8I/IPy6EMC/7A8elDgH5FHDwn8YXn0
iMA/Ko8+Jo8eFfhj8uhxgX9cHn1C4E/Io08KfLY8Ws7IbVwhT42nP92YaJQX+PHyaAWB5z6n
RisKPM8FavR2gR8pj1YS+OHyaGWB5zlFjVYR+MHyaFWBHyiPVhP4e+TR6gLPc5YarSHwfeXR
mgJ/tzxaS+B7yaO1Bb6HPFpH4O+SR+sK/B3yaD2B7yqP1hf4zvJoA4HvKI82FPj28miGwLeV
R0MC31oeDQt8S3k0EPjm8mhE4JvKo1GBbyyPNjK4BmOGv27xcdWov87xOapRf1/gE6pRfx/h
T6pGjwj8U/LoIYE/JY8eFPin5dGHBP60PPqAwD8jj/rnD/5Z1egegX9OHt0p8NvkUZ6La4x1
xvMCf7882kfgexurDLZ5QeDZlhrNFHi2XW6wzYsCTy812l/gM42lBtu8JPD0UqMDBJ5tFxls
87LA00uNDhJ4tl1gsM0rAk8vNTpE4Nl2nsE2ZwSeXmp0mMCz7VyDbc4KPL3U6AiBZ9vZBtuc
E3h6qdFRAs+2Mw22eVXg6aVGxwg820432Oa8wNNLjY4TeLadarDNawJPLzU6QeDZNmZcYTQR
zZSR47nH0Bby1PgcaSt5ajz3GNpGnhp/UtpOnhr/lLSDPDWeewztJE+Nf1raRZ4af1raTZ4a
zz2G3ilPjX/W6GlsM7ivyLob5IAnR+nDTzImG35t8aw3ORlrm20cM8oJ/OvyaLrAZwn8G/Lo
NIGfIfD3Cvx8efQ+g/2eMI4J/OPyj5myD8A/Ko++KfCH5dFHjIeNB+Wp8QdUo/vlUT8Ofq9q
dLfYpYw+/FuqUT83PMfG5zsMasBvl0eXCfwWeXSzPLpC4DfJoxvFBmX04derRlcK/GqBX2uw
7yWGnxt+sWqU+QN+oTzqz9Mc8/484mcZPMP+139mRf/b6yaTr5V0r2v8MuXVkxMPZCWG9Ojh
Xu/447fTEpHhs2O8ei9aNivR++dccV7r9mXKKym/vX1M4psf5uS0LzQ6siNzVGJTrn05I5+p
FKkypXkiX/kiiXavb4gsyFsrMfjXmgleBXjvQ0USk29o7vKVC/fn1L15VIL+B6vMy7n87ugE
46S+wnJv37zxsWWy3OsUR0/eEZvyZfL1iHpNpHu1ZdceI8Nd9ydfg/jY6SXhZd8kez79+Pdw
2/TktqmvvIw+Mjfy9DVj3L4uRPdGms1JzuHuckWi/aYm51bqz5rR85eTc25UrHm0wsHksRSr
PSraJt9+d4wTLo6O3jvyPnfsqa/IrFwqK/ofe40da1Xk62nRm+y1d6yhXpfp1vb+A1nRg/ba
RF51d+V306Ib7PV59HxdNiva2V6xx7apr9T8sOyY6IaycyOsz67ho6JdTu2NsG4bsppHj5Ut
EmWdW46vFe0xv2aUdT77SJFogeubu/zS3H2Rz1qPitJf6I/7IhU/GR1lnNRXcB48kC84eUvy
9YJF6+0M9/gy+QpFvTbUvZpzy8RhsZn7k69KvDrfktj+b5I9z3S8GPs+Pblt6is7v/h4bs7D
+ce4fT3ebF/OD900h1uLJF6Zlpxb0aU1E+tH1nJzPl+0eWLS4eSxXJH3zkTGjX9EVn43O5L6
us/U14Cmvio09RWiqa8ZTX39aOprSVNfXZr6StPU156mvg419TWpqa9STX3FauprWFNfz5r6
2lbda+4aaLw6K3Gwy/fuGugRm5JofXFOmNf21d0xPbFjSEH7b4jpkTcWT0t8X/X+8PpIEKnf
a1Ki9VX3xiJ/Lo70zM5KLL/iXIzXFKa+FnDL3X0SH/y0OWfohecj7/7QMXHXF4UTF4dWjdT8
PT1xQ8X0RJl8ZyNvvF0i0feP5vbK0iaRW/dvy3lyfP8Er7a8WGN5ztvLR7n7okXfIvFT9yXv
qT3PXR3/4+ppiaxyzSPF8uyIbSuafBVp+OLq2K6a9lrB14dGrsypG178avI1iLf8Oj183F65
yutWv3zwq/CPx5KvU0x9zeLAs5sir63ok2CeGwYVjv74b0f32udSW9OjdT5PT9z08iuRw9c2
izYYdrN7FWO/V++JLqywPSf21YP/7bWPqa+DtCdg1D/79KpK91rJz+zVoLntHuQVtE+EsqKr
7ZWU3F931poWfdVeVclx9Xp8UnSB3YO86rT6Mbt/7dWWrO35FlnRrnY/8hrZ1FdhXvXX3dHz
P2yKXLrzpcjHRzpF6/59tbu/+hQrHz03PD3K/MefLRk9dHXzKONvumJ7ZOau/tHG9Y5E+rdY
Eblz4Ch3X5Qofm3Q/b7kPTWzRqHgserTopyX13ruCzeITY4u2jErct8jS8MlM5L318JimbGT
1sOYD9ZZHGsSTI7+MPe+SLNrf4nZe12jXCeprxPN7Ls5Z9aXd0eZ5+cvXp1YdLhTlOvh76Pp
id4vJ+e5PL15InKkpBuz4PYBiXp7F0VqxZ6IrP57dOL9hve5Z067jOGJalP3R3gtqV9jW+9E
Liv+TyS3zSuPgV4h8prmM6408hsFjILGVUYh42qjsHGNUcS41ihqXGdcbxQzbjBuNIobNxkl
jJLGzUYpo7Rxi1HGuNUoa9xm8D1culHeqGBUNG43KhmVjSpGVaOaUd2oYdQ0ahm1jTpGXaOe
Ud9oYDQ0MoyQCJtCIOgHThhwcwD7gEaisSk0EcwRmopmpsBxQXPRwhRaCtYFWonWpsBaQhvR
1hT4nh04F9Be+PPVwWoPWUejk9HZ6GJ0Nfy23czfYdxp3GXwvXYPo6fRy+ht3G30MfoamUY/
w8+5v/l7jAHGQGOQMdgYYgw1hgk8a1BG6tfE63DLRxgjjVHGaGOMMdZgTccZ440JxkRjkjHZ
mGJMNbKMacZ0g+/XZxr3GpzHWcZsY44x17jPmGfMNxYYrBXrBH4t/fr4tfZr78+FPzf+XLWy
bcGviz+3nGfw594fbzPLwF8rHCP4a4nrChqJaqYQFf7a5PjAX7v+Wuba9t5/5nv9tn4sP3Yj
2wb8vv1c/Nz8XP3c/TF55ThT8Wvg1a+NV79mXv1aevVr7NWvvVd/Trz6c+U1v80nFX9uvf7v
WKPUc4q/IoWF5v9vhf9Xjjm57Wf8488Erz++NFi6dZ69zmpeMGnE6eD9akcdDQafDp5++1Sw
/fMTweuFEw78fa+dCs52eDbYNLuN247XWa030GJL2wTX5royVCj8e3hi7hIhxscz7nuJWmHG
LtmuaYhxVpyaGGLcOrMeD7GfMx9dEWYubPe29dJ34ZemIbabZRnjnCyQN8x2NWwbtsscNinE
dhcOXBliPsyD42AeK1s/647taZsD2zM24zEHxuf42J65MB5zYXyOj32x3c4ijbm90gb3q+40
o3s0sr58evj0a5UjF078Hjq+tbKra398o6tRPu9Q8Qqnu1f/GdC39p0LAXm/fz5y9ZpS77n6
hR5vu3rrH2+4ekj0vKuZC/37H4m5mjlSX3PVMVdzDNSvTNyc7Ldjo+a42R9KzXGgZXqcDJNz
3NSNPqzsao6X+sKbH4T4nHVw9YnJrl5fIDmPoQ8k5/Fq3uT+t92e3P+KMcn9r380uX/OAeO4
c2HjXl8huf+KzZL7/2pdcv+djib3f87OHftLm5vcf6cqyf2XKZrc/8Znmrl1/GR1U7e+/9Ro
4upjT0ddvfWO5PmYOKmWq4tvTp6PtR8mzwfK+IfSk+dj4LLk+bjz9eT5uO1S8nws6ZY8D31+
TZ6HShnJ81Dv+eT+Z69L7n9r7eT+byxMvjfUv00z2+/kUM3j5+y4J4fy1nnV1n1vqM89bzl9
/ps3Xf5jyY9c/ebBD1298c8/XF3ryB+uTs5zbyg578mh9xO13PjLP+O4JofO1Gzk6veHNHL1
lKuS+3+6ZXL/aWta2PmaHGp08U47f3tDjcaccXrhi2ddfvh8OVvnvaGv+t1q531y6NdLcVf3
fi3m6uT52uvOG5/3zrPFze9Uuy1ufld8cszVpTsdd/W6zXFXV74ux9UnM1q6/ZQ5ndzvyYzn
XM3rQNnv20uS+/3u6hxXd/squd/kdbrXXa/sd3P+5H7tVYhu3KZfJvfb+47kfl/fntzvsOLJ
/Y7OTq5704bJdb9/SHLdr/wpue7Vbk2u+/WPJdf9zcvJdR9zPLnuyft1byh5/04OnStYxa3z
vgpV3Dp/0Jg6PfRYH5dnqD/j2T9KuufBiEfzOd19mxs34+ltv/HXc5rdT6xPxnNDPnD18Tff
cvruv1xfezOuXn7e1W2OnXV18j7bm9Fm2tMu/6JsjtOVNR93nz+4/XFXn/nMrU9GVtdVrtb6
ZYzZ1NXVma/kclrm/idZ54wGvzzEtw1pDR4s4eoxDW909U//vM5fl2llXud+25tx8oY5rr5Q
qoKru1/Bfb83g9dy0re6d3I+Xaok5zN8c3I+PIf4vOi7jzptvPmI0x0lDjm9sfKDTld8lJx3
g5zjNm566Pb11OmhfzN3uM/H8SpB+6PrMGPwf9q7+rS92pC84sLk8VSMPuDqVrOSxzPrmuTx
ZO58Mzn/U7OTxzWpvDuOS6fcfZJxOE9Ld55m3tXM6W9vuvspI3fh5PP9YtXanPeMgrWrus91
P2a0PVzc1bt+yON0QOnkeV54T/K87no1eZ4PfZs8v8nnuK3b7uT5LXQ4eX5/yJ/c/809k/s/
ON89V0Kla59z61Br3JtOY9EPnb40mP2ku+cB2qQA80sPfbWdeaeHCt+X3H5HjXp2nOmhWXcn
nBb/uZSd5/TQyYPZTvUcDj21JMeNl3kk2Tfr7eR2+UuWdn1PnEr26++N0OAtyfMz6enk+Upb
ldx+7OTkPHs3SM77z2bJ+RYYmZyv/v4L1d34bLCjVk7AdTt/xfOOB8wXybUg6JhvQbA18UJQ
t/Fa+x7ixeDLT3u6vGf1fEG8+IsBr7C+NOaFYP+Ew2G2HWnXLOPMOTAtg/tihL3ismrmqaDp
yqeDuTfGg9yVnwt+SF8WFPz1haBh85buddLFv8vn9jN9wjdhXhfNdc9YY5o+4+aWmdU3NHzg
qaDRxTczGGOWjc380l4pmnG2pl2TnRc2rHjNEncNvlSkZcB4dTfms89XN9y28WKYvuFzDoS5
vy5ULZIx6+5oRv6es8Npd3bLeLF+rzD7Y76zzvfJiGe0DKcdHpRRLxyE034YnvGN/R3I/jgu
7sMvP33X3X+LzvcJZdprOcd1OhXiPrbtG3Kfv5vnYEOeC6HnZoXml3kusFcIu2vcvoVzP9fb
t3Hudw95VKP++1R8XoHPZ/DnSoPtAc/31Xi0gMAXlEevMugtZPAZ4K+WRwsLPL8/ALz/nh/P
7xPo43cKfhy83we/Z/BzwPM7B2q0mEHG7x+oAc/PIHiU30nQx+8l/Dh4fkdBjfpjx5dUjd5s
0FvK4DPAl5ZH/c98+DKq0VtFWWX03Wb4cfB+H5wL5lDOSDf8z2T4CqrRigJ/uzxaSeArC3wV
ebSqwPMzITVaXeBryKP8ngXwtYzaRh3D/5yJr6carS/w/B6GGm0o8BnyKBct4HmIA56bDI/y
kAU8P8/i0UYC31gebSLwTQ1+RuPnVz9nPD/DUqMtBb6VPNpa4NvIo/5nUXw7gW8vj3YQ+I7y
aCeB7yyPdhH4rkY34w7jToG/Sx7tLvA95NGeAt9LHu0t8HcLfB95tK/AZ8qj/trA91ON9hf4
e4wBxkBjkMAPlkeHGEONYcZweXSEwI+UR0cJ/Gh5dIzAj5VHxwn8eHl0gsBPlEcnCfxkeXSK
MdXIMqbJo9MFfoY8OlPg75VHZwn8bHl0jsDPlUfvE/h58uh8gV8gjy40FhnMc7E8ukTgl8qj
ywR+uTy6QuBXyqOrBH61PLpG4NfKo+sEfr08usHYaGwyNsujWwR+qzx6v8Bvk0e3C/wOeXSn
wO+SR3cLfLo8ukfg98qj+wR+vzx6wKAX7/vIHhD4B+XRhwT+YXn0oDz6iMAfkkcPG0eMR43H
5NGjAn9MHj0u8I/Lo08I/Al59El5NFvgY/JoXOBz5NGEPHpS4J+SR08ZTxunjWfk0WcF/jl5
9HnxgjL68C+qRl8SLyujB/+KavSMwJ+VR+cLPPcX250z6AP8q/LoeYF/TR59XR59Q+DflEff
Evi35dF35NGTAv+uPPqe8b7xgfGhPPqRwF+QRz8W+E/k0U8F/jN59HN59AuB/1Ie/Urgv5ZH
vxH4b+XR7wzm/L3xgzxazihvDJKnxtObbuwyKgj8Dnn0doHfJo9WEfit8mg1gd8sj9YQ+E3y
aC2jjrHeWCuP1hN4nmvUaAOBXymPZgj8cnk0EPil8mhU4BfLo40FPksebWo0NxYY8+TRFgI/
Vx5tJfCz5dE2An+vPNpe4GfIox0Fnr/nqNHOAs/8qNGuxh3GZGOiPHqXwI+XR3sI/Fh5tJfA
j5ZH+wj8SHk0U+CHy6P9BH6YPHqPwTX4o8F1+J3xk/GzPPqNwP9HHvX3Bf4X1egXAv+rPPqp
wF+URz8W+N/k0Y8E/nd5lHm+Z1wy/pBHTwr8n/LoWwL/lzz6hsD/LY+eF/iz8ugrxtPGs8Y/
An9GHl0o8PONk8Yp41+BvyyPLhH4RUbcOGn4H7rwbEuNLhN4ts022CaXfQ54evHoChPAs+0T
Btvkthrw9OLRVVYDnu2OG2yTx2rA04tH11gNeLY7arDNFVYDnl48us5qwLPdEYNt8loNeHrx
6AarAc92jxiHjXxWA/5KeXSL1YDfaPqQwTb5rQY82+HR+60GPNs9YLBNAasBTy8e3W414Nlu
n8E2Ba0GPL14dKfVgGe7H41BxhBjqDHC4H4D/M/SUfLUeO4xdIw8NZ57DB0nT43nHkMnyFPj
L0onyVPjf5NOkafGc79NNaYblwSeewydKU+N5x5DZ8lT4/8y7jPOGtxXs4w5BjngyVH68LuN
PYZfWzzrTU7Gul5lWsi4WuALy6PXCHwRgb9WHi0q8NcJ/PUCz//EIDXK/4wg+73RYH+A538i
EH+TwT4AX0Ie5X/iD/D8T/vh0VJGaeMWeWp8GdXorfKoHwdfVjV6myinjD58umrUzw3PsfF5
eYMa8BXk0YoCf7s8WkkerSzwVeTRqqKaMvrw1VWj/M/xAb6mwPO/w8S+axt+bvgTdt6pUeYP
+DryqD9Pdc3784ivZ/BH4n7fZ1djlDq3+8R/NitK6bOK7rNkXx7z9Kcro8dnyf7kq16vsNx/
xj7wPvtY27JdXgPlM/pQn2USWcbn+Qw+622Q0eOzPsqQKw0+q0RhfczVZ/STUec3qAsavs9n
fE5GXcDw/b7PZyVoUx/j0H8tkWX0+AxPRn2VQZ1h+D6fFVXG/goZ9FdWxtg+o59tqa82qKsa
ZPT5jM/JqAsbvt/3+awIbeq7xpzvJ6PHZ3VpUx/b+M/I6PFZbdrUx3rwWXUiy+jxWU1ljMOx
81l9ZRyHz/yash5k1A3/B3tvAijdUZYJd0hYjDBsQVBBgrIEgUMtp05VYYBcCPsaNtmUJBDC
EkJIAoRNwr4vAiI7ISyyKCIu4w4uKOM27vrP7z8/MzoOOi6oiKhI5nnq1CHNl+8j91z63q+6
+wm8t/t9vrdOV3c/fZ56a4Xxenzv14cRPxlGjJ/vhPGRGB9PgPHxBrApbsL4SIyP/Hc+3h02
xU3YjSrG63wTjPidKsYyE8ZHluXjDWF8PAU2vcaE8ZEYH3ltPt4FNsVN2KkV4+t9M4z4PSvG
9zthfGRZPpKffLwJjBjjJmziLn8ffE77Vhjjpuf0b14xxtGn3bhi03P6D68Y4+jTblGxqQ6s
x70qxtegT/u2ik3P6d+nYoyjT7tpxabn9E+sGOPo076jYow7sdr9KjaVIX6zik3P6T+gYoyj
T/v2ik3P6Z9WMcbRpz14CWMdaA+tGOs3YdNnys+PGP3vhvGzPxZ/p8/ukRXjv/OzvCXs+ccQ
HO+nE3YrQhVjLOP+ByFgyzF/XrGr4JExLHdSxfhAjP6t6aDsFEP/f1WMDyxH7DvpII73K2L0
bwMjxnsNMfq3hRGjz+vT/9+wKW7Cblcx3n+I0e8qNtWL/l9VjHGsB7Hp/sJ7AzH6BsbXmOpK
//9UjHGsLzFbMd5/iNF3FZveE/2/rRjj+L6I+Ypdu2L0+4pN753+31eMcXz/xELFeP8jRn+o
GH2+f/r/UDHGTVisGO97xOinitHnZ0L/nyrGuAnLFTu+YvTvULFvrBj976oYy/HzpP/PFWPc
hJ1csetXjP4dK8YYfsb0/6VijJuwO1WM90di9O9cMfr8Luj/a8UYN2GnVOyGFaO/U7HpO6T/
7xVjHL8zYnepGO+jxOjftWL0+T3S/4+KMW7CTq0Y7/fE6N+tYvT53dK/rGKMm7C7V+wGFaN/
j4oxhhygf8wxBMdjwSfsnoSA8X5KjP69YMR47yRG/94wYvTJH/rMOae4CbsPIcTxPkmM/n1h
xOiTU/SvWssybsLuh+eMOxF/idG/P4wYfXKP/tVr2ROXsAfgOeNuVjH6DyQEjOXIR/rMG6e4
CTuNEOJ4vyVG/0EwYvTJW/rMUaa4CXswIcTxnk2M/kNgxCa+02c+NcWR88QeSghx34G/xOg/
DEaMPjlP/9q1LOMm7LvxnHHfWjH6DycE7Mb4yzj6j4ARo8/fC32276e4CXskIcQdi7/E6D8K
Row+f0P0mc9NcRP2aEKIuxr+EqP/PTBi9Plbo88cYoqbsO8lhLir4i8x+o+BEaN/Cow+88Ep
7hQ8I3Y6jNhx+HsK7HTYGTBip+DvDoz+VJZxE3YmnjOO/l1g9B8Lm643YWccM2KMuyuMMcxX
GceYCXscIWD0+dulfxZsipuwM2tZxvH3zBjmU4xjzIQ9nhAw+vw90z8bNsVN2ONqWcbxN84Y
5t+MY8yEPYEQMPr8jdN/ImyKm7DH17KM4++eMczzGceYCXsSIWD0eS+g/2TYFDdhT6hlGcd7
AWOYLzOOMRN2DiFg9Hl/oP8U2BQ3YU+qZRnH+wNj2EfAOMZM2LmEgNHnPYP+U2FT3ISdU8sy
jvcMxhxfMcZM2Hl4zrL0eR+h/zQYMcZN2Lm1LON4H2EM+7YYx5gJO58QMPq8t9C/ADbFTdh5
tSzjeG9hDPvWGMeYCbuQEDD6vLfQfzpsipuw82tZxvF+w5jjKsaYCXsGnrMsfd6D6D8TRoxx
E3ZhLcs43oMYc5WKMWbCLsJzlqXP+xL9Z8GIMW7CnlnLMo73qhJTMcZM2LPxnGXp815F/zkw
YoybsGfVsozj/YsxX4YxjjET9tyK0ef9i/7zKsa4CfvlijGO9zTGfKlijJmw76sYfd7T6D+/
YoybMPatsC6M4z2NMf8GI8aYCbuYEDD6p/MZ7AWwKe50PoPxSIQp7gw8Y8wXCaHs6fg7YS8k
BIz+mTD6L4JNcRN28jEjxrjHwhjzBUIoy5gJe3HF6D8ORv8lFWPchJ1Sr8e4s2rM52scYybs
pRWjz3sf/ZdVjHETdmq9HuPOrjH/WOMYM2Evrxh93vvov6JijJuwe9brMe6JNeZzNY4xE/bK
itHnvY/+qyrGuAm7b70e455cY/6uxjFmwl5dMfq899F/TcUYN2EPrNdj3FNqzN/UOMZM2Gsr
Rv9cGP3XVYxxE/aQej3GPbXG/HWNY8yEvb5i9M+D0f/+ijFuwnisAbnBuKfBGPNZGDHGTNgb
Kkb/fBj9N1aMcRP26Ho9xl1QY/6yxjFmwt5UMfoXwuj/QMUYN2Gn1+sx7uk15i9qHGMm7M0V
o/8MGP0frBjjJuy59Xq3AMZYxvw5jO+XGOOIvQU2Yc+s/lsrxpgJe/bS9S4Czph31jjGTNjb
Kkb/WTD6b68Y4ybsOfV6jHt2jZmux5gJewees370nwOj/8JalnET9i48n94HY3mti2scY54L
Y8y7YYxj2QnjERXEGPc8GGNeVDHGTNgleM44+t8HuwT2Hhgxxk3YI2pZxj0fxpgXV4wxE3Yp
nrMs/Yth9D+yFDdh7wXOOPovgNF/H4wYrzdhD61lLwb2QhhjpusxZsLej+csS/9FMPofgBFj
3ISdVq/HuBfDGPPhijFmwn4Iz1mW/ktg9D8II8a4CbtfLcu4l8IY89KKMWbCPoTnLEv/ZTD6
H4YRY9yE3auWZdzLYYz5UMUYM2EfwXOWpf8KGP0fhhFj3ITdrZZl3CthjPlgxRgzYT+C5yxL
/1Uw+h9YipuwjwJnHP1Xw+j/KIwYrzdhO7Us414DY8z7K8aYCfsYnrMs/dfC6P8YjBjjJuyO
tSzjXgdjzDsrxpgJ+ziesyz918PoX7oUN2E/Dpxx9L8fRv8nYMR4vQnLtSzj3gBjzHsrxpgJ
+0k8Z1n6b4TR/ykYMcZNGMdxprg34Rlj3lcxxkzYf8ZzxtH/ARj9n4YRY9yE2VqWcW+GMWa6
HmMm7GfwnGXp/yCM/ntqWcZN2M/iOePovwVG/5KluAn7OeCMo/9WGP13L8VN2M8DZxz9t8Ho
v2spbsJ+ATjj6L8dRv8dS3ET9ovAGUf/HTD6vwIjxvcxYZ+oGP13wuh/EjbFTRjH6Ygx7l2w
T8I4nkeMMRP2S4SAPbpi9H+ZUMUYS2xqYz4Sz1mWMc+o12Od3w1jfd9eMb7uhP0qnvN69C+B
0X/rUtyEfQo44+i/B0b/12DEeL0Jm97HJcAuhTHmLfV6jJmwX8dzlqX/Xhj9Ny3FTdingTOO
/vtg9P8LjBivN2EcI53i3o9njHljxRgzYb+B54yj/wEY/d+EEWPchHEsdor7ITxjzBsqxpgJ
+y08Zxz9D8Lov34pbsJ+Gzjj6H8IRv93YMR4vQnjePAU92E8Y8zrKsaYCfuveM44+h+B0f9d
GDHGTdhJtSzjfhjGmNdWjDET9nt4zrL0fwRG//dhxBg3YbesZRn3URhjpusxZsL+AM9Zlv6P
wuj/IYwY4ybs5vV6jPsYjDGvqRhjJuyP8Jxl6f8YjP4fw4gxbsK+vZZl3MdhjHl1xRgzYX+C
5yxL/8dh9F+5FDdhfwqccfR/Akb//4ER4/Um7MRalnE/CWPMKyrGmAn7b3jOsvR/Ckb//4UR
Y9yEcW7DFPef8YwxL68YYybsz/CccfR/Gkb//4MRY9yE3biWZdzPwBgzXY8xE/bf8Zxl6f8s
jP7/DyPGuAnjfIwp7ufwjDEvqxhjJuwzeM64m+Mvsc/AnlfjiDGW2P+EMe44/CX+P2DLGOPo
c84I426Jv0+H/TnsL2ATdkH1/1fFboVHYvT/cgl7WvX/d8VOwiMx+p9dwp5a/b+q2K3xSIz+
Xy9hT6n+/6nYd+KRGP2/WcKeXP2/rdht8EiM/t8tYU+s/t9X7LZ4JEb/c0vY2dX/h4rdDo/E
6P/jEnZW9f+pYh0eidH//BL22Or/c8Vuj0di9L+whJ1R/X+pmMEjMfpfXMIeU/1/rZjFIzH6
/7aEfU/1/71iDo/E6H9pCXtU9f+jYh6PxOh/eQl7RPUvq1iPR2LFrxwi9t38d/jT2EmoGP2p
n4vYQ2H0j61lh4rRP24JezBw+letWIRPjP7VlrDTgNGfxjoSfGL0r1HjiD0ARn8a18gVoz/1
YxK7H4z+NIZxh4rRvyaMvw9i94HRn8Yrvqti9P9TjSN2Lxj9aWzi5IrRv06NI3YPGP1pzOGO
FaM/9VMTuxuM/jS+cKeK0T8BxvoRuyuM/jSWcOeK0Z/65YntwOgv9/3/PDDeH86A8Xq8Z0zY
N1eM/i/A6D92KW7Cpvsa73XE6HNOGK9H/xdh9M+qGOMmbLrH8r5LjP5Nahz9T8Don10xxk3Y
dL+nBhCjf9MaR/+TMPpPrBjjJmzSnh+rGP2b1TjG/BKM/pMrxrgJm/TyRytG/ztqHGN+GUb/
KRVj3IRN2v0jFaN/ixrHmF+B0X9qxRg3Ybes2EcqRv9WFWPMr8LoP20pbsJOqtiHahz9W1eM
MZ+C0b9gKW7CpvbVB2oc/dvUOMb8Goz+0yvGuAmb2oTvqxj929U4xvw6jP5FFWPchHUVe0/F
6N++Yu+qGP2p3U6MscSmNvUPwP80jPnXlEO8cQkbgJOn76wYY3zFvhcYcfpTvkCM1yOWahyv
919gzBmn633/EnaHGsdyjGNMrNjp8InTn65HjHHETq5xvN5vwJjnTtd77RJ2pxrHcoxjzHdV
7Ez4xOlP1yPGOGKn1Dhe7zdhd4Q/Xe/VS9hdahzLMY4xd67Y4+ATpz9djxjjiJ1a43i934Lt
wJ+u94ol7O41juUYx5i7Vuzx8InTn65HjHHE7lnjeL3fht0N/nS9ly1h965xLMc4xtyjYk+A
T5z+dD1ijCN23xrH6/0O7F7wp+u9ZAm7f41jOcYx5j4VexJ84vSn6xFjHLEH1jhe77/C7gd/
ut6LlrAH1TiWYxxjHlCxc+ATpz9djxjjiD2kxvF6vws7Df50vRcsYQ+rcSzHOMY8uGLnwidO
f7oeMcYRe3iNewH834M9FP50ve9bwh5Z41iOcYz57oqdB584/el6xBhH7NE1jtf7fdgj4E/X
e+4S9r01juUYx5hHVex8+MTpT9cjxjhip9c4Xu8PYN8Df7res5aw59Q4lmMcYx5TsQvhE6c/
XY8Y44g9t8bdBT71lnp8ZsVOrRj9xy5h1Fb6j6vY3eETo3/WEvaLwOg/vmL3hE+M/tlLGDWT
/hMqdm/4xOhPGkrskzD6T6px960Y/ScvYb8EnP45Fbs/fGL0J20kRt2jf26Ne2DF6D91CaPG
0T+vYg+CT4z+pHnEfhVG//wa95CK0b9gCaN20b+wYg+DT4z+pGXEfg1G/5k17pHwqVHPgP+s
ij28xjHmoiWMcfSnuGfC53f+bGATX56xhE08+ElgPwd7HuJeVq93c/jEiX1fxej/IYz+K5bi
Juz5FbtFjaN/ccWeXTH6L6gYy/0RjP4PLsVN2Asr9pwaR/9FFXtexei/uGLPrxj9l1TspRWj
/6GlOOLEXrqEvRgY/Q9XjO/3Z2D8TF5esR+Hz3rz/b+yYh+vGP1XLWF/DJz+qyvGchP25op9
rGKMeU3FPlox+t9fsQ8DI/5a+K+r2AcrRv/1FfuhitGfyhLj69J/Q417f8Xov7Fi760Y/TdV
7NKK0f+BJexPgNN/S8V4/Qmb3hvfLzH60/fL75YY/R+qZS+pGK/11oq9u2L031ax1wAjTv/t
SxivR+z9S9jbgTHmHUvY24DRf2fFXsdyMPrvWsLeCoz+u5ewtwCjf8kS9oPA6L9nCXszMPqX
Vuz18InRf2/F3lAx+u+r2KuA8X3wPXygYq+sGP3psyLGz5D+B2vcyytGf5njLwROLn+kxh1z
3F8tHnjc7592yaePueQav3/pl1532b9cxv/jBPUv88h0/P/fL3v3pSe98gr///yXL/uHcoI6
/j7/Pz5xKUqM/+HJTT512o1//bQb3+Np/P+n+P8Tfv21f37SeFj7Rz/4yg+f9MoP42/5/6Uf
fOW33+20E/j/l5x50guPu9dJrz3xoS88YXHdm9/7un91jQdd8wTUePrvnEvfd8ov/+bNdujz
HY7/XX4S+oQc/nH/4m5y+Bc8Ano14OMJ7GPA/tXrCBWo8Pi614F32WWfPfZaiwc/6ylnPvWc
U88/45lPPPfsZ/yGLRRhcvLPf3j9O33onbe8E59ftQQfX4PvfsZjzzqWl7uMy2c+94X7/8KT
3vGzbD8s/v5l55y8/PySO//RHQ7FEX/HKYbPz3zb/e/IGF5nek7/+Iv5GngJLL1Zfg3U6xd+
+J9uyjbH4p/O+rGff8Ldd8rzv3/Z3/zcx992/+n5d03PEXPyFIOyd5zKLteD1xpfjy941XLd
z77rDSdPr/H5v/n78vxV+Y4/v/z8A/e4Xak76zE9/+prXYXuYroWnx8+7uoLXPvkKY7Pp9dh
/Y+EL8dM12XZ6Tlfb/rv+OlJebzssr899rjFXe/7sPvwC8fP/qv+9RpL3kv++W2n0JYgUMKy
fbj47d+67x0//A/jJmeH+k84hrJ58Z1HO738fCu5GLqL/8YFXpcH8lqLU/B/2MWwS2CfhH0G
tsD1rwM7EWZgp8AeCOPrnge7GPZy2Othb4FdAvsg7GOwn4Z9EvZp2O/C/hT2GdhnYZ+DfRHG
uanHwa4BuybsOrATYDeC3Rh2IuzmsJNgt4UZWA9LsJNhp8BOhd0Tdl/YA2EPgT0c9mjY6bDH
wZ4AOwd2HuxC2EWw58Iuhr0Q9mLYS2Evh70S9mrYa2Gvh70B9ibYm2Fvgb0N9g7Yu2CXwC6F
vQ/2AdgHYR+G/TDso7CPwT4O+wnYT8F+GvazsJ+H/SLsk7Bfhv0q7Ndgn4b9Buy3YL8D+13Y
78P+EPbHsD+F/TfYn8H+O+wzsP8J+wvYX8I+C/tr2N/A/g72Odg/wj4P+wLsi7B/g30J9mUY
+xuPgV0FdizsONhVYVeDXR12Ddg3wI6HfSPsmrBrwf4T7Nqw68CuC7se7PqwE2A3gH0T7Iaw
G8G+GfYtsG+F3Rh2E9i3wW4KOxF2M9i3w74DdnPYLWC3hN0KdhLs1rDvhN0GdlvY7WAd7PYw
A7MwB/OwHhZgAyzCEizD7gD7LtjJsDvC7gTjXOZTYDuwu8DuCjsVdjfY3WH3gN0Tdi/YvWH3
gd0Xdj/Y/WEPgD0QdhrsQbAHwx4CeyjsYbDvhj0c9gjYI2GPgj0a9j2w74U9BnY67AzYmbDH
wh4HOwv2eNjZsCfAngh7EuzJsHNgT4GdC3sq7DzY02Dnwy6AXQh7OuwZsGfCLoI9C/Zs2HNg
z4U9D/Z9sOfDLr7r4mLY4gV4hC1eiEfY4kV4hC1ejEfY4iV4hC1eikfY4mV4hC1ejkfY4hV4
hC1eiUfY4lV4hC1ejUfY4jV4hC1ei0fY4nV4hC1ej0fY4vvxCFu8AY+wxRvxCFu8CY+wxQ/g
EbZ4Mx5hix/EI2zxFjzCFm/FI2zxNjzCFm/HI2zxDjzCFu/EI2zxLjzCFu/GI2xxCR5hi/fg
Eba4FI+wxXvxCFu8D4+wxfvxCFt8AI+wxQ/hEbb4IB5hiw/hEbb4MB5hi4/gEbb4YTzCFj+C
R9jio3iELX4Uj7DFx/AIW/wYHmGLj+MRtvhxPMLKf7o/6/58FXDhWNhxsKvCrga7OuwasG+A
HQ/7Rtg1YdeC/SfYtWHXgV0Xdj3Y9WEnwG4A+ybYDWE3gn0z7Ftg3wq7MewmsG+D3RR2Iuxm
sG+HfQfs5rBbwG4JuxXsJNitYd8Juw3strDbwTrY7WEGZmEO5mE97NSd91/91J03f9upO392
6qk7L332qTsf/sSpO2eecLed373objs3/tu77VzwtLvvXPNq99i52UfusfOF0++588e3utfO
9Rb33rnqX99757p/eZ+d93z+vju3+ab779zuPg/Yuf2bHrjzqX84bed1j3vwTvrbh+xc9OqH
7dzwrg/f+evrPnLnT/71UTt//O/fg3bG6V9ld3jIo3fyWx6285bhtJ2/vNV9dy4+6x47F/3V
XXae+9E77fzKj95h50ufHXZOeZjfucbnb79zk0/cdudNP3HrnV/9vVvu3OmEm+98+lk323n4
4qY71/7AjXf6J37Ljr3njXZet/NNO1948Ak7t/y+6+188Revs/OoG1x757SLr7XzuS9/486j
X3/8zm/5b9h50WevvvMHP3K1nRu96Ko7P3f2cTv2UcfufP7RV9l5zTnH7LzyFYudY8++7JRb
/OF/nPKpR3zplJP/5d9O+buP/Osp93vmF08Z7wH62/YnIE6L020zdH7txGlxej5r2i4hTovT
bTN0fu3EaXF6PmvaLiFOi9NtM3R+7cRpcXo+a9ouIU6L020zdH7txGlxej5r2i4hTovTbTN0
fu3EaXF6PmvaLiFOi9NtM3R+7cRpcXo+a9ouIU6L020zdH7txGlxej5r2i4hTovTbTN0fu3E
aXF6PmvaLiFOi9NtM3R+7cRpcXo+a9ouIU6L020zdH7txGlxej5r2i4hTovTbTN0fu3EaXF6
PmvaLiFOi9NtM3R+7cRpcXo+a9ouIU6L020zdH7txGlxej5r2i4hTovTbTN0fu3EaXF6Pmva
LiFOi9NtM3R+7cRpcXo+a9ouIU6L020zdH7txGlxej5r2i4hTovTbTN0fu3EaXF6PmvaLiFO
i9NtM3R+7cRpcXo+a9ouIU6L020zdH7txGlxej5r2i4hTovTbTN0fu3EaXF6PmvaLiFOi9Nt
M3R+7cRpcXo+a9ouIU6L020zdH7txGlxej5r2i4hTovTbTN0fu3EaXF6PmvaLiFOi9NtM3R+
7cRpcXo+a9ouIU6L020zdH7txGlxej5r2i4hTovTbTN0fu3EaXF6PmvaLiFOi9NtM3R+7cRp
cXo+a9ouIU6L020zdH7txGlxej5r2i4hTovTbTN0fu3EaXF6PmvaLiFOi9NtM3R+7cRpcXo+
a9ouIU6L020zdH7txGlxej5r2i4hTovTbTN0fu3EaXF6PmvaLiFOi9NtM3R+7cRpcXo+a9ou
IU6L020zdH7txGlxej5r2i4hTovTbTN0fu3EaXF6PmvaLiFOi9NtM3R+7cRpcXo+a9ouIU6L
020zdH7txGlxej5r2i4hTovTbTN0fu3EaXF6PmvaLiFOi9NtM3R+7cRpcXo+a9ouIU6L020z
dH7txGlxej5r2i4hTovTbTN0fu3EaXF6PmvaLiFOi9NtM3R+7cRpcXo+a9ouIU6L020zdH7t
xGlxej5r2i4hTovTbTN0fu3EaXF6PmvaLiFOi9NtM3R+7cRpcXo+a9ouIU6L020zdH7txGlx
ej5r2i4hTovTbTN0fu3EaXF6PmvaLiFOi9NtM3R+7cRpcXo+a9ouIU6L020zdH7txGlxej5r
2i4hTovTbTN0fu3EaXF6PmvaLiFOi9NtM3R+7cRpcXo+a9ouIU6L020zdH7txGlxej5r2i4h
TovTbTN0fu3EaXF6PmvaLiFOi9NtM3R+7cRpcXo+a9ouIU6L020zdH7txGlxej5r2i4hTovT
bTN0fu3EaXF6PmvaLiFOi9NtM3R+7cRpcXo+a9ouIU6L020zdH7txGlxej5r2i4hTovTbTN0
fu3EaXF6PmvaLiFOi9NtM3R+7cRpcXo+a9ouIU6L020zdH7txGlxej5r2i4hTovTbTN0fu3E
aXF6PmvaLiFOi9NtM3R+7cRpcXo+a9ouIU6L020zdH7txGlxej5r2i4hTovTbTN0fu3EaXF6
PmvaLiFOi9NtM3R+7cRpcXo+a9ouIU6L020zdH7txGlxej5r2i4hTovTbTN0fu3EaXF6Pmva
LiFOi9NtM3R+7cRpcXo+a9ouIU6L020zdH7txGlxej5r2i4hTovTbTN0fu3EaXF6PmvaLiFO
i9NtM3R+7cRpcXo+a9ouIU6L020zdH7txGlxej5r2i4hTovTbTN0fu3EaXF6PmvaLiFOi9Nt
M3R+7cRpcXo+a9ouIU6L020zdH7txGlxej5r2i4hTovTbTN0fu3EaXF6PmvaLiFOi9NtM3R+
7cRpcXo+a9ouIU6L020zdH7txGlxej5r2i4hTovTbTN0fu3EaXF6PmvaLiFOi9NtM3R+7cRp
cXo+a9ouIU6L020zdH7txGlxej5r2i4hTovTbTN0fu3EaXF6PmvaLiFOi9NtM3R+7cRpcXo+
a9ouIU6L020zdH7txGlxej5r2i4hTovTbTN0fu3EaXF6PmvaLiFOi9NtM3R+7cRpcXo+a9ou
IU6L020zdH7txGlxej5r2i4hTovTbTN0fu3EaXF6PmvaLiFOi9NtM3R+7cRpcXo+a9ouIU6L
020zdH7txGlxej5r2i4hTovTbTN0fu3EaXF6PmvaLiFOi9NtM3R+7cRpcXo+a9ouIU6L020z
dH7txGlxej5r2i4hTovTbTN0fu3EaXF6PmvaLiFOi9NtM3R+7cRpcXo+a9ouIU6L020zdH7t
xGlxej5r2i4hTovTbTN0fu3EaXF6PmvaLiFOi9NtM3R+7cRpcXo+a9ouIU6L020zdH7txGlx
ej5r2i4hTovTbTN0fu3EaXF6PmvaLiFOi9NtM3R+7cRpcXo+a9ouIU6L020zdH7txGlxej5r
2i4hTovTbTN0fu3EaXF6PmvaLiFOi9NtM3R+7cRpcXo+a9ouIU6L020zdH7txGlxej5r2i4h
TovTbTN0fu3EaXF6PmvaLiFOi9NtM3R+7cRpcXo+a9ouIU6L020zdH7txGlxej5r2i4hTovT
bTN0fu3EaXF6PmvaLiFOi9NtM3R+7cRpcXo+a9ouIU6L020zdH7txGlxej5r2i4hTovTbTN0
fu3EaXF6PmvaLiFOi9NtM3R+7cRpcXo+a9ouIU6L020zdH7txGlxej5r2i4hTovTbTN0fu3E
aXF6PmvaLiFOi9NtM3R+7cRpcXo+a9ouIU6L020zdH7txGlxej5r2i4hTovTbTN0fu3EaXF6
PmvaLiFOi9NtM3R+7cRpcXo+a9ouIU6L020zdH7txGlxej5r2i4hTovTbTN0fu3EaXF6Pmva
LiFOi9NtM3R+7cRpcXo+a9ouIU6L020zdH7txGlxej5r2i4hTovTbTN0fu3EaXF6PmvaLiFO
i9NtM3R+7cRpcXo+a9ouIU6L020zdH7txGlxej5r2i4hTovTbTN0fu3EaXF6PmvaLiFOi9Nt
M3R+7cRpcXo+a9ouIU6L020zdH7txGlxej5r2i4hTovTbTN0fu3EaXF6PmvaLiFOi9NtM3R+
7cRpcXo+a9ouIU6L020zdH7txGlxej5r2i4hTovTbTN0fu3EaXF6PmvaLiFOi9NtM3R+7cRp
cXo+a9ouIU6L020zdH7txGlxej5r2i4hTovTbTN0fu3EaXF6PmvaLiFOi9NtM3R+7cRpcXo+
a9ouIU6L020zdH7txGlxej5r2i4hTovTbTN0fu3EaXF6PmvaLiFOi9NtM3R+7cRpcXo+a9ou
IU6L020zdH7txGlxej5r2i4hTovTbTN0fu3EaXF6PmvaLiFOi9NtM3R+7cRpcXo+a9ouIU6L
020zdH7txGlxej5r2i4hTovTbTN0fu3EaXF6PmvaLiFOi9NtM3R+7cRpcXo+a9ouIU6L020z
dH7txGlxej5r2i4hTovTbTN0fu3EaXF6PmvaLiFOi9NtM3R+7cRpcXo+a9ouIU6L020zdH7t
xGlxej5r2i4hTovTbTN0fu3EaXF6PmvaLiFOi9NtM3R+7cRpcXo+a9ouIU6L020zdH7txGlx
ej5r2i4hTovTbTN0fu3EaXF6PmvaLiFOi9NtM3R+7cRpcXo+a9ouIU6L020zdH7txGlxej5r
2i4hTovTbTN0fu3EaXF6PmvaLiFOi9NtM3R+7cRpcXo+a9ouIU6L020zdH7txGlxej5r2i4h
TovTbTN0fu3EaXF6PmvaLiFOi9NtM3R+7cRpcXo+a9ouIU6L020zdH7txGlxej5r2i4hTovT
bTN0fu3EaXF6PmvaLiFOi9NtM3R+7cRpcXo+a9ouIU6L020zdH7txGlxej5r2i4hTovTbTN0
fu3EaXF6PmvaLiFOi9NtM3R+7cRpcXo+a9ouIU6L020zdH7txGlxej5r2i4hTovTbTN0fu3E
aXF6PmvaLiFOi9NtM3R+7cRpcXo+a9ouIU6L020zdH7txGlxej5r2i4hTovTbTN0fu3EaXF6
PmvaLiFOi9NtM3R+7cRpcXo+a9ouIU6L020zdH7txGlxej5r2i4hTovTbTN0fu3EaXF6Pmva
LiFOi9NtM3R+7cRpcXo+a9ouIU6L020zdH7txGlxej5r2i4hTovTbTN0fu3EaXF6PmvaLiFO
i9NtM3Qvtbvssvd+5hsWD77wrCeee9Y51zren3it4w3MD/xraWl6dpeznnnW2U8/9+wLnnLW
OY876/wT73b+48+44AIAiHrgXU984IMecOK9HnTiaQ/dechD8PSepwI2xvg+48lDzn/6WSee
d/5ZF5x17mPPesyFZ11wIcBTz7jw6U/BozXlJY7wl/+2bKVSLFXxyd8555yzzzrz/DOe/tgn
XHD2OV96wjlnPOW8s651fLQsfBGNf0wXAx6mwuWFqz9hjmElNLPqUwhhfjw9jJcYYBGWYIwr
r2NLbRhqGWsZbMsLMtwy3rKAZQnHSzuWcCzhWMKxhGMJxxKOJRxLOJbwLOFZwpfqsIRnCc8S
niU8S3iW8CzRs0TPEj1L9OUdsETPEj1L9CzRs0T5qgJLBJYILBFYIrBEYInAEoElAksEvkbh
ysASA0sMLDGwxMASA0sMLDGwxMASka8RWSKyRGSJyBLly4ksEVkiskRkicLCxBKJJRJLJJZI
fI3EEoklEksklsh8jcwSmSUyS2SWyCyRWSKzRGaJ8k1PPGQZa1jIGpayhsWsYTlrWNAalrSG
Ra3hq9n69ZeytpQdGTBSYOSALWVHFow0KDywhQi2MMEWKtjCBVvIYAsbbKGDLXywhRC2MMIW
StjCCVtIYX2pc6GFLbywhRi2MMMWatjCDVvIYQs7bKGHLfywfXm/hSG2UMQWjthCEltYYgtN
bOGJLUSxhSm2UMUWrthCFlvYYgtdbOGLHW8uhTG2UMYWzthCGltYYwttbOGNLcSxhTm2UMcW
7thCHlvYYwt97PjjLgSyhUG2UMgWDtVbWWGRLTSyhUe2EMkWJtlCJVu4ZAuZbGGTLXSyhU+2
EMoWRtlCKVs4ZQupbGGVLbSyhVeu3NmcITdc4ZUrvHKFV67wyhVeucIrV3jlCq9c4ZUr9xVX
eOUKr1zhlSu8coVXrvDKFV658f4y3mDqHYacdOM9ZrzJjHeZ8TYz3mfGG03hlSu8coVXrvDK
FV65witXeOUKr1zhlSu8coVXrvDKFV65witXeOUKr1zhlSu8coVXrvDKFV65witXeOUKr1zh
lSu8coVXrvDKFV65witXeOUKr1zhlSu8coVXrvDKFV65witXeOUKr1zhlSu8coVXrvDKFV65
witXeOUKr1zhlSu8coVXrtycXOGVK7xyhVeu8MoVXrnCK1d45QqvXOGVK7xyhVeu8MoVXrnC
K1d45QqvXOGVK7xyhVe+8MoXXvnCK1945QuvfOGVL7zyhVe+8MoXXvnCK1945QuvfOGVL7zy
hVe+8MoXXvnCK1945QuvfOGVL/crX3jlC6984ZUvvPKFV77wyo8KNkrYqGFVxHi/8qOMjTo2
CtmoZKOUFV75witfeOULr3zhlS+88oVXvvDKF175wquxAeILr3zhlS+88oVXvvDKF175witf
eOULr3zhFYWk/HZZTxjvjkXZ8Fg0B49FA0pgUYAiAOU+XG6lRTnKzb/oRpENllALAJ8gPyu1
APAhqAWw7y0A19XWFB4h9YOB6vuxccB/iv0wZBuBlx8roGFIFq2x1MexOQQo5oyWVkA7aGwn
AcpDzLgb5zyVw02zj0MPlQtj08x1uG/lHPyAtsXYYgQUjU8xDh73ovG20fUGehRjNnlserqu
9ynHgKKDGduhgGJGLQJqYcbmpesCxDg66IvJY8sJEHyIJ1oZY8vJdQPUFc2owGqUmxOghPYE
buXGjJpuXRd7j3dtEt7R2PhzXTI5QtVRdhjbVoCS6dFYxbVrM8l1OQR8mrgb4/LlPuc7g/cb
Y0SLdZQs6zuwPECjI9o9tV3aoWFjggk5pvoWfQfFymh7oulR25seH02GKvYWtRibYb4LaDji
gzARMlrusR7vMfvoYzR4Y+Uz9XhDqc8DCpqxTYVKpOhzgu6Z3I9N+bHFyx/h5c9QMpowQAzx
iuM3i1qg/vjCUs5jAwQXMzEkqH/ElzG2P/EZ4s30+ICirY1vfGkDvh4DHQp5bKG7ziZQAp9a
j7ZGeVnbgX34rg3efj9mF7YbQC4kH6CbGb9aC07gQ8e7Dvh0ypu0HRqNIeCNQ/bH5qzpco4G
H/4Qw/hJIPcFOfAdGRJozGM6UD2kIaKdXJuypuvReELuAdKnMSsw+Gng5dHixcc9NudNh28D
zcOU7TBmSbnDB4/Xxlc9gNQlBcMLouKoa4Yil7eYuyGYIfVoH5iUirhnfI1xQLMQnw2i+UHk
zuMt47OPEUJcmnIZPzzT40sjy8HrEoU8I+aEn2foQ/lR5Q6cBWvwXeBfymeTuozPF7mO9/hs
SiMwdahAQqOOdA6lBZPAEn5liORb5IeT8MkbtFmNj/hoS6ss4UeFH35ATfBtliZR6vDJoG2J
iyWkK3zbgPDzx1eB5gZ+H/ylJfz8UUUQP/f4NsbLowK4j+C3AA6WJknCt5hxOyhEBYFLQZAK
18j4xkysEH6bBneuPiTcmvhJJPzQ0G5JuE3h51IajbFDfdAiw08KtC9tTUD8OeHLzrjHlGZy
xO8YtwN8ESDieOcAhPeDm1wEDcAKXB6QwZddPquM+ALh9obfBtqL+CJLE5GtH1m7nwFu7RI/
iZ/ET+K3CvErma/ET+K3FqIv8VPmh+RO4ifxW0/xYx6GNO9KMj8mlnvK/JhFKvPb0AxW4ifx
k/ip21Pdnur2XItsbZXdyBI/iZ/ET+K3IvFbn27PcZhOQ34bmtTtRiOlfdI+aZ+0b+u0T/Nd
2p2HshvhWkWMxE/iJ/GT+En8Dt/rqSG/Dc4MJX4SP4nfVovfuMhgNSsdDr7Xc3fzXUYN00oH
ZXvLGaPET+In8dtq8RtXxa1G/MqWMg2udNjzZM+xoJb5beRcGImfxE/iJ/FbUbenxE9r3Ncn
u5T4SfwkfhI/id/hx/yU+WnMT7ubaXezopHa3axs06ndzdZrdzN1ey6Pden5mJ0q81Pmp8xP
md/aZn77POFFsz2V+SnzU+anzE/7Wmtfa+1rvT5jeleW4SrzU+anzE+Z39pmfuM5D1e2taeW
OlyZEGzjv0v8JH4SP4nfhoufxvy2Udyu7D1L/CR+Ej+Jn8RPsz03ci3f1xJAiZ/ET+In8VuR
+B38Di/q9tycMbivJVT78W8SP4mfxG+rxY9dgjrIXQe5b5+ISvwkfhK/rRa/PW9v1hfVDDHY
PkTTD87Zg9/hZZ+XOhxmkTtzTRxva5zzcQjO5RTG45Hi0IdBO7ysj4hK/CR+Ej+J34q6PSV+
Ej+JXx5i9sbkbNh2gsR6G3s0jVw/BM/WGqHe5hz8YFM0bDsRisanGNF++kpUbxy6JGI22fgx
qPcpx4CigzFsfaJcH7OLOVjvjK1QcH6IzvHaQ61DgO8CYvqhvt7ggsQPn6DvUvQ5eetM7g1H
bsaPsXyWl//xnXZ40Q4vvfExrdcOL6tc6qDMbz/G347GNSEcjswojzZhEatNwceqDS7Efhiy
jVrkrkXuRSMlfhK/psTv4Ls9+Yrq9jwaYrXq15T4KfNT5qduzxV1e2q2p7o91e2pbk8m0zkE
5NG+79G5W/oSfWfQzRtjtC65XPJr31lngwPqDMKYhfvOof8xmJBjqj27vvMmZotZBd7Zvhbs
TXa5760dci5dyb4LdkDeHkx02ZSM3neDyz56pGzJ2RoV+9TnAQUNujnHV1S3pyufvekGM4Q0
RIuNrHLp8TVd7wZ8I+hux+emzK+pzI9fR+q0w8uqs6JtuJ4yP2V+yvyU+a0o8zv4CS+7Ez+2
a2K3fJI723xA2JREQydrpcP6JGyr0mVpn7RP2ift2zrtSxK/rdvQ5VDRlPhJ/CR+Ej+Jn3Y3
2zoxlPhJ/CR+Ej+Jn8RP4qeVDpgW4jESYIzzdQ1I7P2glQ5FI7XSQfNdvsZ8F0321GTP9Rk7
VOanzE+ZnzK/FWV+By9+B7/Mj60fLfM7dPxsHX2Jn8RP4ifxW5H4rc9kT014WZ8Mbb+EVeIn
8ZP4Sfw2XPxWubuZNnjZLzE66OtK/CR+Ej+Jn8RPE1404UUTXjThpexFc/lu1pc/077W2uDF
9V9jwou6PTXhZX26U5X5KfNT5qfMb0WZ38FPeNnrBi8a81sfkdqv7lCJn8RP4ifxW5H4HXzm
t7vZnlfc3Wzv4qfZnvslRgd9XYmfxE/iJ/FbW/HbXea3ygkvEr+DFqn9ej2Jn8RP4ifxk/hp
wosmvGjCiya8aMKLTjTCMUGxz7E3LlofQ2THYepwpvVaTnhZZeanpQ77lYkd9HWV+SnzU+an
zG9FmZ8mvGi25/pMpJH4SfwkfhK/FYnfwU942d2Y3yonvCjzO+gMbb9eT+In8ZP4Sfw2XPxW
2e2pCS/7JUYHfV2Jn8RP4ifxk/hpwosmvGjCiya8aMKLJrxs1oSXVXZ7KvM76Axtv15PmZ8y
P2V+yvyU+SnzU+anzE+ZnzI/ZX57y/w021OzPTXbMw8xe2NyNuxxQH7pbezj0Lt+CJ7zpQj1
NufgB5uiyRWKxqcYB++/EoWVRkOOMZts/BjU+5RjQNHBmLLpsuv6mF3MwXpnbIWC80N0jtce
ah0CfBcQ0w/19QYXlPkp81Pmp8xPmZ8yP2V+yvyU+Snz21vm1+pSB8323K9xs3W+rsb8lPkp
81Pmt+GZ3yonvGid3zoL3nLdJX4SP4mfxG/DxW+VmZ/Eb1lA1vm5xE/iJ/GT+K1I/DThRRNe
NOFFE144pSeHkIL3fY9pPWUgzXcGE3xijNYll8usG99ZZ4MD6gzCOKfHd87CMSHHVOf0+M6b
mG0/OO9sXwv2Jrvc99YOOZdJRL4LdvCY+WOiy4bNXVxrcNlHH6PBYGaNin3q84CCxo1TjXyX
os/J42VzbzTmpzG/vY35tSp+q8z8tM5vnbO95bor81Pmp8xPmd+KMr9WJ7yscsxP4rcsIOv8
XOIn8ZP4SfzWVvzYl5E6k7LBPPU+JOs80zxAWC4VU+ojOkqyxG+dRWq/6i7xk/hJ/CR+KxK/
Vrs9Vyl+mvCyX2J00NeV+En8JH4SvxWJ3zZ0e0r8Dlqk9uv1JH4SP4mfxG/DxW+VE14kfvsl
Rgd9XYmfxE/iJ/GT+Gl7M21vpu3NtL2ZljpoqcPeljqo21Pr/LTOT+v8tM7PRuwyHstqQ9dh
J/LYm95Ga8fFjNiNfMC+48ZzPaOve5bbhL3OsTqyd9GXDcptly03MTdY5tgb3lut7Qbsmm5N
6LEkcdyz3Ha9tylhdWPAKkj2SyHKmRQCFjh6E1K5lulyjgaLLIcYxhWPpovY9RxrMQ13Ri9r
LE03GCBDtBF1qeV6N2DlJTZUx/pIznS3pnN8eZs9llWG0lgwHVZdOlQj28GWPdhzhwWWeG0s
6RywWzsXZ2a8ICqOumbfj28xd0MwQ+q9G0xKnm8xY7lmHBxWhwaDaFYidx5v2YQhRo/asRK5
c9H0WJzJ7duxYXuBLN5yTs6n0IeyhDN32MYdq0PxXeBfymeTuozP1/aYD4nPZhgnR6ICyeGT
HuIQHC+futjzK0Mk3yI/nIRP3rgeBSM+2szvLHUBH2YfUBN8m7ZV8VO350F3Ka7D66nbU92e
6vaU+KnbU92e6vZUt6e6PdXtqcxvb5mfljqo21Pdnur2VLenuj3V7YkO6tI5iv7uHj3QHl2k
Q+0v5a5/Bvv65R6d0GOvKvpdPXquB3TJxjD2vWK/PRzvWfbhw/585VroS8c1MjqqTazQ/EXu
rFZEvzS6ydHFnXFk6FCncaaQA7qf0f0+HgQakRU7vI8c0fmNvvBSMBl0cZce4oz4AuG00oCD
SHE9kyxbAevQ87fNdVSvp3o91eupXs8N7/XUGvdtFrkjvXeJn8RP4ifx2zrxU+K39YmptE/a
J+2T9m249mmu55GSn23GJX4SP4mfxE/ipyG/rcsEJX4SP4mfxG9txY+zT678TAdlftuc4R3p
vUv8JH4SP4nfisRPCx002XN9JrlK/CR+Ej+Jn8RP3Z7q9tQSdy1x1xJ3LXHfrCXuq+z25FJD
rPzTMr+1F0tlfsr8lPkp81tR5qedPdXtqW5P7e+i/V20v8vW7e/S6pjfKjM/bfBypAkk64Yr
81Pmp8xPmd+GZ37a4GXdhOkg6ivxk/hJ/CR+Ej9NeFn7Mby5ginxk/hJ/CR+Gy5+6vacKwzb
EC/xk/hJ/CR+Ej9lfsr8tNRBSx201EFLHTZrqcOex/zGlFEnGm2kMCrzU+anzE+Z39pmfrvb
3mzP4jcWlPhJ/Dh73w1Dstb51MeezSJCOObR4ghK2+e+r5CWOmipg5Y6bN1Sh1bX+Un8tmEM
b+57VOanzE+ZnzK/tc38xqPd55/jnnSe30Zmc3MEUOIn8ZP4SfwkfprwsnViKPGT+En8tlr8
2CWYViR+B7/Dy+7G/LTUYU5GtC2xEj+Jn8Rvq8WPwrC+4re7bs89i99YUBNeNjIrlPhJ/CR+
Er+1zfz2Wfw02xNNo03NBCV+Ej+Jn8Rv68RP8102VtN2q9XSPmmftE/atyLta3Wlw557PZX4
KfEbBkMaUCq1zI8fQzI5up7COcT6yaRkeutcP2SbeBNAVA4hBe/7Pvih7JriO+MHG2O0LrnM
xqf1nXU2OKDOIGyEnIVjQo7JmLJy0nfexGz7wXmH5ZRjVG+yw8pKi1pkjvvjWsEOPuZgosuG
v3hAg8NqMx+jwc41NSr2qc8DChpn6rVS9Dl5vGzujTZ40QYv67LBy+7mu4walhNWI/f4SYH2
u1zpoCE/3ER2m0mtW5wyP2V+RSIlfq40PEyHdl6Q+K2L+GnIb3PFab/FVOIn8ZP4qdtT3Z5a
5rexGd6RRFTiJ/GT+En8ViR+B7/MT5mfMr8jiduV4RI/iZ/ET+K3tuKnMT+J35WJ3JH+XeIn
8ZP4SfxWJH6a7ek9ZqWZZJkDH+mmK7yNz0biJ/GT+En8ViR+69PtqWV+W6/N0j5pn7RP2rd1
2rfLlQ7jEgltbraRQinxk/hJ/CR+Ej9N9txIgftaPcwSP4mfxE/ityLxO/ghP813aWP47GuJ
TKv/JvGT+En8JH5rK367W+mw5w1e1O25wfN2JH4SP4mfxG/DxU9be7aafR3Nekn8JH4Sv60W
PyY3qzrN7+C7PZX5qdtzrwIq8ZP4Sfy2WvyYFUn8Bk140YQXY3EMQSw7/eMEhxD7AYcURB3q
MCTsA+9Nz3YyWgw61CGPx3z4DidZ4CQJn3IGXfjp4OSKGJLDOl9j+1iOlnBdxAkVPU69iNaO
J1e4DidUuGQ8D6/wfvxYbbI54yiM3kVfDrOwHdgXcjY406I35awM2w0Dzrcwocf5E0P5PmzX
e5ykgaMsAo68KCdX2A4b94eA0yy8Calcy3Q5R4MTNYYYxuMtTBfzgF2sJX5r2+25uwkve+72
HAtqqcNGCqMyP2V+yvwkfmsrfrvr9tyz+GnCC1qle+1WbL2cxE/iJ/GT+En81O25sSJ3JBGW
+En8JH4Svw0XvzGB28NZtsr8lPlpzE9jfkUjcR58GLwNODpeY369zX7wcRzpNJ3JzmHoMdvB
Go5h5i7jHzFelNyQYhlHzxhkxGAlxiez78dhzdwNwQyp9w7bISfPYc3cBQyzuz5gPBTRHLDM
nccwJz77GD1O2mVnX+5cNH1OPmLo1Dn27OXOYpgzJ+dT6IPhyH3uME49OI/xV/xLGQ9NXcaY
qu2N9xgPHVhw0ye8qNvzSNnPNuPK/JT5KfNT5re2md8+T3hR5oem0aYKpMRP4ifxk/itSPxa
PdRB3Z6bKmBfz/uS+En8JH4SvxWJ38Evcj/4zI9dzhFrndDHHYfgXE5hPB4pDj2GBHSc39pk
ihI/iZ/ET+In8dv1bE+J39eTbbVUVuIn8ZP4SfzWVvwOfp2fxK8lAft66iLxk/htpfiVqZBW
W7ys/XTPg+/35Cuq3/PrUZ1Wykr9pH5bqX68hUn8Vr3WodUZL1rr0IrgtFQPiZ/ET+Knfk/1
e+560E+ZX0sC9vXUReIn8ZP4Sfw2XPy01uHrEYlNLSvxk/hJ/CR+ayt+GvPb3FXo+y26Ej+J
n8RP4re24re76Z7K/PZbSNbx+hI/iZ/ET+K3IvE7+Akvu8v8JH7rKE77XWeJn8RP4ifxW5H4
HfwWL8r81O25V5GU+En8JH5bLX7MilZ1rMPBZ357Fb9xS7Lsne2HaPOw68meWuS+V61prZy0
T9on7dtq7duGI4323Os5rg/EsVRDzDm6wcWklQ6tidhe6yPxk/hJ/CR+G97rqTXuexWITS4n
8ZP4SfwkfisSv1Z7Pa8ofnvu9VTityl6KO2T9kn7pH1bp31J4rc2Jw/tl9hK/CR+Ej+J34aL
356H/MaCGvLbSKGU+En8JH4SvxWJ3zYsdNBkz/3KxA76uhI/iZ/ET+K34eJ3xSG/vXd7SvwO
WqT26/UkfhI/iZ/Eb0Xitz7zXSR+Whov8ZP4SfwkfisSv1a7PVeZ+Wm2535lYgd9XYmfxE/i
J/GT+O16gxeJ30GL1H69nsRP4ifxk/itrfhRilJnUjbGpj4k6zzTPEDeh5hSH22fs2Z77peA
rPN1JX4SP4mfxG9txW93O3uusttTE17WWfCW6y7xk/hJ/CR+Ej91e27kWr5lsTv0ucRP4ifx
k/htuPitsttTmd+hIrKuvsRP4ifxk/htuPitsttTE17WVewOrbfET+In8dtq8WNWtH2n+e19
nZ/E71ARWVdf4ifxk/httfiNkyNT75OLIQ9xCG6cRRL7HHvjovUxxFEih8G4vjc+phCyL6oZ
YrB9iKYfnLMHv8hdsz21WH2v4ivxk/hJ/LZa/FaZ+a3PIvc9H+qgIb+9ak1r5aR90j5p31Zr
3yoTv1a1b5XzXdTr2ZqI7bU+Ej+Jn8RP4rd1812U+G3dwoZDNVLaJ+2T9kn7tk77NN1FI4US
P4mfxE/ityLxO/jpLuPMnCvb3EwLHQ7NeuTjtuc6R2aUR5swl8um4CP7BAoU+2HINgJnrzmh
YUgW2+dhy7x+Khhztt5hylfu+xqFOWPZG5PzVM7b2Mehd/0QPDvNcSnf25yDH2yKpr6gj8an
GAfsyjdFYbbZkGPMJhtOLkM5zErLmJWWw2BMfb0+ZhdzQC2MrVBwfojO8dpDrXuA7wJi+qG+
3uCCxA8fqu9S9Dl560zuDW9h48dYPsvL//guRhMGb8MwfbO+662z+MJSzi6Ukr4zMSSXbMSX
EStJ8IVh4mBvo7W+fh2cHZiMDwbTButXaxMokUPoXfTlZW0H9uG7Nt6gOEeUrO0GkMuaALqZ
8au14IRNyUQXnO0LvWznDCYkRh+9Calcy3Q5RxNBL0xPLEGmiyBHSBK/FYlfq0N+Ej+J3RUz
3aJwo6ZAvSR+rhuSs947a8y4QS4+odh7SD5alx6yOX5YyeToegonZoZXKOHe7qDuGffhEcJt
HE0J3/eQ+EkXIPa4/1qXXC4K7DuIR3BAnUEYC/rOQYUoCjFVffcd7v7ZQi9Qtb4W7E12aG9Y
1CKXm7nvAnQIrQDIQDZFdnw3uAwFgGrhjdWo2Kc+DyhoIHbjK0r8XPnsTYd2XkhDtBFCXEWz
dwO+ETS68Lkx1bAGTUZor80eH/co+abDt+GgwdkOtrTTcocPHsKLr3pAi44fdIbaQrVBkOz7
Ud9zNwQzYJ2BG0xKnszJ+Brj4MCaYBDNSuTOQ+/R8IjRo3asRO4clhegxcImHhp1BbLQ+5zQ
Ng19KF9t7sBZsAYNEfxLaRikLqNxYbFewaNhMLDgqlb5tSp+/GpjlxNaxz1+UqC9uj2vKAbb
JpASP2V+RW4lfhK/r3+VX6vip8xv24RtN+9X4ifxk/ip23PDuz2V+e1GDLYtRuIn8ZP4Sfw2
XPyU+W2bsO3m/Ur8JH4SP4mfxE8HGm3duj+Jn8RP4ifxW1vx4xSufTzHfUwZMWkJE4wxxW1w
mAZVJs8kg9lNZRfUnALnMsUOk9kxE9pjVprBTGdAu8k+FHP0PieJn8RP4ifxW5H48ZafOsyD
dQO2u8bsSmjGCGGlE+Yce6yHGup+2JwEbTDNOfdYeMJBuYTpq1iIxJnPWG4TxhV8mI6MlU9l
WjKmK5corJ/BNTJWN5lRiq5c/FbZ7clKxE7id/REa1UNBomfxE/iJ/Fbkfhptqcyv/URRYmf
xE/iJ/HbcPHTbM9VZUubdB2Jn8RP4ifx23DxW2W3p8b8NkUAJX4SP4mfxE/ip9meWzdBR+In
8ZP4Sfw2XPyu2O05TtDM3CwQW9llbB881JQOkzcDtpnDHrPjpsCY3KLJnpuS7C2/D2mftE/a
J+3bcO1Tr+fyTV/Pxzk5Ej+Jn8RP4rci8Tv4lQ7j4gedaCRBmz/JVOIn8ZP4Sfwkfur21JCf
jvPTiUbl8KVymM8hf3Scn040cj2OQoo4KbEuVcdadtsHnK2Ewxmtlvlpmd/8DOxoZa3K/JT5
KfNT5rfhmd8K57tof5ejpVWrfl1pn7RP2iftW5H2HXzit7udPVc530Xit2oROlrXk/hJ/LZS
/Mbz6w3OVR9wbLvUb23VTxNe1qeb8Wip3JFeV+on9dtK9WPKYCV+JgxMi9Lait/Bp351NaAO
dVj7CTISP4mfxE+Z39qK3+4yvyuO+SUtcl978TpSRrdbXOIn8ZP4Sfw2XPxWOeinzG+34tJ6
nMRP4ifxk/hJ/LTOb+syQYmfxE/iJ/GT+En8JH5a5K5F7lrknrDXMQ4Jz2WRv+mwr7Gzrvep
1yL37VrkPvaXamPrjRRGZX7K/JT5KfNb28xvd7M9NeGl9fG3o1E/iZ/ET+In8Vtb8dvdbE9N
eDka4tL6a0r8JH4SP4nfisSv1VMdlPm1LkRHo34SP4mfxE/ityLxO/j9zXaX+Un8joa4tP6a
Ej+Jn8RP4rci8Tv4zG93Y37q9mxdiI5G/SR+Ej+Jn8RvbcVvd5mfxO9oiEvrrynxk/hJ/CR+
Ej+t89vI5QxfS4AlfhI/iZ/Eb0Xi1+qY3yozP+aasUva2HrtxVLiJ/GT+En8JH7K/NZezL5W
lne4f5P4SfwkfhK/FYlfqxNe9jzbc0wZtcPLRgqjxE/iJ/GT+K2t+GnCiw6zPVxWtxtM4ifx
k/hJ/FYkftsw5qcjjXYjLOsQI/GT+En8JH4rEr+D7/ZU5qfMb69CK/GT+En8JH5rK367W+S+
5zG/saDG/DTmdzylchiStQ6nu8Seo8GEYs7Wu2D73JczYADlIWZvTM6G9EGQt7GPQ+/6IXgS
llBvcw5+sCmaXKFofIpx8P4rUb1xQ44xm2z8GISjZXIMKDoYU1+vjxm1CKiFsRUKzg/ROV57
qHUI8F1ATD/U1xtckPhJ/CR+ayt+yvyU+Snzk/gdb30X7ODRCjDRZVPaJr4bXPbRx2hwUGFp
dvgu4ly6PPTWGjc2O3yXos/JW/i9YefV2IYoDYnL/6BkNGHwNgxTs8Z3vXV4UTRIsgulpO9M
DMklG9ESibWFhNZK7E1vo7W+tkX6AW0T44MJ2dd2jcUZemjVhN5FX17WdtmyoWO8QXEOKVnb
DWhZWRPQ1jJju8Z2vbcp4V0HZ/vyJm3nTAoBb9ybkMq1TJdzNBFtqxjGT8J0ES2jkCR+Wyd+
bP3GLnvwBWc3ZrSvB/IGC/hSyCGRznlsNQPCeY5o4Eec6ohDHscoLfNb+2SQeduUvwWbhkFn
2eosW2mfzrI9PqGFxOaKi9bHENleSWh1mO06y5ZvW+KHD2GvyVXL5SR+6vVUr6cSv61L/NLu
Mj8mBhI/iR8+AUqlhvz4MSSDTpCewjmURjGhhE49hzHNjA648cNC/10K3vc9BjanDkEMcaLj
zbrkchl39B16DYMD6gzCWNB3Dt2P7A2MqY5q+g7dfhk9NI79NLVgb7LDKKtFLXLtz1Svp3o9
c8KIfOhD6dDOHQa4wRr0QIeYS49w6jJ6lW1vvEeP8MD7e1qR+B38SgfyPnUmZYM+qz4kzEYY
3xDeXYgJMxPwc8ljApcT5gT0+Emhs1/it5nZ3JxMU5mfMj9lfsr81lb89jrfZXeJ32F6PfmC
yAU15Lf2PaHSPmmftE/at3Xat8vE7zDip/kuc5KrlmMlfhI/iZ/Eb8PFb8+9nhI/5LktC9jX
UzeJn8RP4ifxk/hppcPGityRBFLiJ/GT+En8ViR+nNSVOiy/dEPA4sxksTpuhLDDBRZceuyD
MWQu6UzY4QJTcjDRK/dYc8kMK2GzDGxAwblfWGkaxsE8LDvFjhdlOSqWqZYoLB3FNTJ2tTCx
QprvcqQbvPAjZ64SP4mfxE/ityLxO/jJnnud76IxvyOLwrYIpsRP4ifxk/itSPxazfzG1Xp7
WOlwmDE/zfbcFHGU+En8JH4SvxWJX6uZnya8bIpgrfJ9SPwkfhI/id+Gi98qMz8tdVilAB3N
a0n8JH4SP4nfisRvG7o9JX5HU7BW+doSP4mfxE/it+Hip27PVYrGplxL4ifxk/hJ/DZc/FbZ
7akJLxI/HWWrfa2LbOo0v7Jluemwy7jDoYLZDracupxxWByONeyxhfmA85m54C3j+EAcQ4iN
z7PvxwMLczcEM6Teu8EknCJXooKNg8Nu6MEgmkcR5s7jAEPsQh2jD2ngDThjWZzpcQQjD2zG
Ec0FsjjAUPtal62ul/e1lvhtimCt8n0o81Pmp8xPmd/aZn77fKjDYZY6aMxvlQJ0NK8l8ZP4
SfwkfisSv4Nf6rA78Vtl5ifxO5qCtcrXlvhJ/CR+Er+1FT/t8KKdWvYqiBI/iZ/ET+In8dPG
1trYGschB18G54suRpwCnTH6Phj2fhPSQe46yN0GHB0/MsJ3mvCiCS8BU28G5+zBd3vuLvPT
Uoe9ZkebXE6ZnzI/ZX7K/JT5KfNT5qfMLznrvcO8cuc5To7mAU5jQb6LY1M82rcjlHDSipY6
FNlU5qfMT5nf8bGLQx8G73Fok0mWnNjkrGkT3psyP2V+yvyU+a0o8+Mtf6PO89NShw0WcYmf
xE/iJ/Fbkfi1OuanpQ6bkKmt+j1I/CR+Ej+Jn8RPY35b100r8ZP4SfwkfhsufprtueqsaROu
J/GT+En8JH4bLn7q9twEsVr1e5D4SfwkfhI/iZ+6PdXtqaUOWupQpu7zLAF7yB/fxYiTBbwW
uXcu9Lm32Q84uEFLHY7eUgft7aklFXvNCJX5KfNT5qfMb0WZn5Y6aJ3f+oixxE/iJ/GT+K1I
/A5+qcPuMj9NeNlrdrTJ5SR+Ej+Jn8RvbcXv4Pf25CvGLhmcXByH4FxOgecUa4eXtRszlPhJ
/CR+Er8NF79VzvaU+G1KNijxk/hJ/CR+Ej/N9ly7zO3rFWGJn8RP4ifxW5H4acKLJrxowkse
Is5AMNOpb67zNvbY9tz1Q/AcpIbqekwVz8EPNkXDXnNC0fgUI/ZG/0pUb9yQY8wmGz8G9T7l
GFB0MKbMxXddH7OLOVjvzDg933XB+SE6x2sP9SiGAN8FxPRDfb3BBYmfxG+rxY8/jrQi8Tv4
CS+7G/NbZbcn714a8/t6s64Wyivzk/hJ/LZa/CgMEj80sIcqa5jAEhIa2PivNJuhdL1DYx6H
mA0uJo35tSBcq6iDxE/iJ/GT+Cnz27X4KfNbhfC0cA2Jn8RP4ifx23DxW+U6P2V+LQjXKuog
8ZP4SfwkfmsrfszDUmdSNtiYsQ/JOj/24xrMG4gp9dH26L4s43Q5YVJAn4wxDgVGyDucvB5t
PkK35zhYqG7PjZwJKvGT+En8JH5rK367m/CyZ/EbC0r8JH6cj+mGIVk0r9Ck6tksIoSxYDSp
AppYfZ196TTbk59MDiEF7/sec1rL7se+M5jdGmO0Lrlcppz6zjobHFBnEMaP1HfOwjEhRzRT
y0fqO29iRiPVsalaC/YmO3zk1g74AsaCwWKn5RxMdNmUr8d3g8s+euxIjR27a1TsU58HFEQT
uF4rRZ+Tx8vm3pSqHrKnda2FNrbm3dYabWwdMidfpy5E/PCnja0PfqnDPmd+hxE/vqJme66i
2/FoX0OZnzI/ZX7K/DY88xt7L/fQ7XkY8dOY39EWrVW9vsRP4ifxk/htuPiNGrYa8VPmtyrx
OdrXkfhJ/CR+Er8NF78rZn67m++ixA99vEdbo/br9aV90j5pn7RvRdp38EN+u5vvckXt2+Vk
z8OInxK//RKjg76uxE/iJ/GT+K1I/LS7mbb2XJ9MUeIn8ZP4Sfwkfrve4EXzXQ46Q9uv15P4
SfwkfhK/DRc/zXfZLwFZ5+tK/CR+Ej+Jn8Rv15mfxvzWWfCW6y7xk/hJ/CR+Gy5+e57wMhb8
qg1eJH7LArLOzyV+Ej+Jn8Rv68RvzysdpH3rrHfLdZf2SfukfdK+rdM+rXRYn0mZy4K1yucS
P4mfxE/iJ/HTkN/GrmU/kmBK/CR+Ej+Jn8RP4ifxw5lYAacCcON6nNYQYj8M2cZhMJwsTEhn
OvBjSCZH11M4h1g/mZRMb53r8XklrvVFlM506CNnDOCjiDigoscHFK0dD65wHQ6ocMl4nl3h
eT4AomyyOeNT61305RQJ24F9IWeDIy16Uz5W2w0DjrcwAUeImKF8+LbrPT50nGQRcOIFB2Ws
7XBiWwg4zMKbkMq1TJdzNDhQY8AxBCXIdDEPA87dMH3MrlzKdKB6SDjgLaIutVzvBpyy0eMg
E8x84NV1pkM47JkO27DGXcv8jpRJrRuOG46rtyecSJQgchI/Zz1ODcJ5l+VQTN64ew/Jx+mX
3vST0kn8xuaQ76D4OEXJp5zRVqIy4NSmGJJLNhor8YNcJjekWBqUGWoL1YZQZ9+P+p67IZgh
9d4NJiVP+chdQHvT4RisYBBNBc6dh96bMMToIc28AWecJGZ6nEIV0YZw5VecOwu9zwnnjYU+
lLOqcgfO4hgsfBf4l9IwSF1G48L2OOwVDYOBP/+04Zkff7Wx07bWGudbFmiJn7o9i17pND9l
fg45NjoygqO2JrT5mKxDJn0MpXsjIec2rodqRiTVhzvNbxsyP832XBaQdX4u8ZP4SfzU7bnh
md+4Wm8589NKh60b4jtUp6V90j5pn7Rvw7Vvz72eo2h+1RJ3DfkdKiLr6kv8JH4SP4nf2oof
+yBTh+F4g8kKfUh2HKgH5H2IKfUY28QMKg354RNYV5Har3pL/CR+Ej+J34rET6f56UCj9RFZ
iZ/ET+In8VuR+B38fBdlfusjNvuVwe31uhI/iZ/ET+K34eK35zG/seBXjflpsudexaa1chI/
iZ/ET+K34eK3yjE/TXhpTcT2Wh+Jn8RP4ifxk/jtenczid9exaa1chI/id9Wil/Z/QS7lGl7
M+3w0mMvuzzsWv3U79maiu21PlI/qd9Wqh9vYRK/bdnebJX9nhK/vYpNa+UkfhI/iZ/6Pde2
33Pcie3KFvrtecbLYVa5S/xaE7G91kfiJ/GT+En8Nlz8lPntVSA2uZzET+In8ZP4Sfw05rd1
W8BI/CR+Ej+Jn8RP4ifx03l+Sef5cTJIOcf1kD++ixEnwHkbBpwvy4EUHN6n8/zKKYamM9k5
nKmb7WAND+fNXcZhQDrPj7tv4hTjHucK+2Bx2DM/nNT5HkcOBjfkHkcLk0sJBxQGj/OIB5w1
GMM4mudwcCYIZ/Bo0gjhkEhcI+P4YRMrtG9jflrlji9mU7s+lfkp81Pmp8xPmZ8yv40VuSOJ
t8RP4ifxk/htuPjtebanMj9lfjjBmTSgVA5Dsjg4BIeF9JxDRSjmbNFdgcND+tJPBggnQmdv
zNQ55jqPfo849K4fgi9rrAD1FqeN+MGmOK45BhSNTxH9HP4rUThLGgtQY0a3B7tL8Hq9Txln
TucwGFNfr0cfSMwBtTBjf53rgvNDdI7XHmrdA3yHjhWDrpfxUoMLEj+Jn8RvReLX6rEOEr8j
ZT/bjCvzk/hJ/CR+KxK/gz/WYXfr/K641EEnuW9dL+ehOi/tk/ZJ+6R9a6t97ETax8NstcYd
n++horEpvsRP4ifxk/itrfjtLvHbc6+nxE/ipyG/IWE2tcdg4ThWmDAB2/UUziFOUDKY9I8x
zWwTe3/QrsghpOA5pRvDj4R8ZzDEGWO0Lrlcxh19Z53l7O7oDMLGKGfhmJBjqqOavvMmZkwT
d95haHWM6jG3HqOsmCeOMdcRCnbwGPs00WVTRmR9NzhMuPdYooAlHDUq9qnPAwpyAvlYMEWf
k8fLZswyJ3TIIofiaqUD1i3wwzGdCxjgttnj4w5a6RAifhnO2VaH/K7Y65nU7bmxGd1uM1Nl
fsr8iihL/FxpeJgOU7tCwj7/MdlcJN90vRvQHME8KzQaJH698TGFUFfrhYiJbpP4rc+Q397F
jwSIXTJY0xmH4FxOYRRSTOfDEliPFqpJpRmw25uw4o5O16rET+In8VO359p2e+7zmB8bRFA6
tH4woz2iDYQmkcQPn8AmCLbET+In8ZP4rUj8Dr7bc3fiN2pYTlgK1WMkAb39e8/8JH6bIHx8
DxI/iZ/ET+K3tuK3uwkvGvPbFMFa5fuQ+En8JH4SvxWJ3zaM+SnzW6UAHc1rSfwkfhI/id+K
xO/guz2V+W3G+NvREEGJn8RP4ifxW1vx2+cxP63z25DJLYcTV4mfxE/iJ/Fbkfip21NLHdYn
E5X4SfwkfhK/tRW/3WV+e57wosxPmZ92eNEOL0UjdZatFrlv+SJ3TXg5XBfiOmLK/JT5KfNT
5qfM7/Bn2SrzU+anzE+ZnzI/bW+G+4Drv0bmtw2zPbW92TpmeYerszI/ZX7K/JT5rW3mt7ul
Dtrh5XA3/23HJH4SP4mfxG/DxW/PE160t6e6PdXtqW5PdXuq2/PKuj1bXeqgzG/bs7zDvX9l
fsr8lPkp89vwzE/id7ib/7ZjEj+Jn8RP4rci8Wt1wsuexU+zPdXtqW5PdXuq21Pdnuva7akx
v23P8g73/pX5KfNT5qfMb0WZn8b8tL2ZtjfLOPnYG5OzYY8DJNbb2Mehd/0QPPdIINTbnIMf
bIomVygan2IcvP9KVG/ckGPMJhs/BvU+5RhQdDCmr1DMLuaAsyqNrVBwfojO8dpDrUOA7wJi
+qG+3uCCxE/iJ/HbcPFT5ne4zGfbMWV+Ej+Jn8Rvw8VPY37bLnSHe/8SP4mfxE/ityLxa3XC
izK/w938tx2T+En8JH4SvxWJn8b8NOanMT+N+XFUM4eQgvd9j5FNNoqt7wzGOGOM1iWXy8Cj
76yzwQF1BmFjlLNwTMgx1WFN33kTs+0H553ta8HeZJf73toh5zKO6rtgB4/BTxNdNmzu4hUH
l330OI4hOVujYp/6PKCgceNoq+9S9Dl5vGzuTalqGTo95I/vdKqDTnX4Gnt7tip+q8z8tLfn
pmSMyvyU+SnzU+a3tpkfm3OpMykbY1MfknWeSgcIk+ZiSn1EWzHvecxvLJh6hwl8ObrBxSTx
k/j1sS+pheswzzJjnmUAy/o61dIp81PmZyOm3sZKEkzPjb3pbbR2TG9dhzTWJeOZ4fo6kdcm
TABGvty76AuVbJctZ/YaJL69YWJhbTfgTmRNAN3MOJHXdr23KSHfDciLS3prO2dSCEh5vQmp
XMt0uH8ZpN1DDGMObLqIqcDIzk2P6cIl6zbdYIAM0UbUpZbDvQ+5OGYZI2NW5vc1Mr9Wx/xW
KX6kV+yScc7HITiXU2BPTOwwmT1gnjq6Z0yy/CQ2RSQ29X0o81Pmp8xP4rfhmd8quz0lfpsi
hhI/iZ/ET+In8Tv8YbaH6faU+En81O3pegrnEEt3mevQ7dZbh1X8GT1w7J/ThBd1e0Z0uWJu
04CdG9g3ltHPiv5aECT7fuzZzd0QzJB679BbljyZkzFvKQ4O06SCQTT7XnPn0dNrwhCjR6cs
+14zxhtMj1lK3MoBmzcUyKKnNyfnU+hDmcuUO2zpgGlS6ILGv5Qu4dRldCtb9F56dAkPLJjW
Vvz4SVz5mJ8yv00RrFW+D2V+yvyU+Snz23DxW+WYnya8rFKAjua1JH4SP4mfxE/ip27PrZug
I/GT+En8JH4rEr/1me05TtDMXDWLmb0Z2wcPdTAPkzcDup8x63jcFBgzO5dXOmjI72gma6t8
bWmftE/aJ+1bkfa1usZ9lb2eEr9VCtDRvJbET+In8ZP4ra34UYo030VLCvciohI/iZ/ET+K3
tuKnyZ4Svr0IH8tI/CR+Ej+J34aLn7o99yoQm1xO4ifxk/hJ/NZW/NTtqcxvrwIt8ZP4Sfwk
fmsrfvvc7Tkujtdsz41cBSHxk/hJ/CR+ayt+u8v81O251+xok8tJ/CR+Ej+J34rEb32W+SWt
89vIbG6OWEv8JH4SP4nfisSv1XV+2tpzjihsS6zET+In8ZP4Sfx2vcOLtvbcFHGU+En8JH4S
v7UVv92N+Snz2xTBWuX7kPhJ/CR+Ej+J364zP8qtDnJfpQgdrWtJ/CR+Wyl+5aw7a3C83jCE
JPWT+kn9tm4GjNRP6reV6scGvMRvWw6z1VqHo5Vetfy6Ej+Jn8RPmd/aZn57XeWupQ5bl+gd
qsPSPmmftG+rtY9JUdo67dv7Oj/N9jxURNbVl/hJ/CR+Wy1+nAm56eK3yl5Pid+6it2h9Zb4
SfwkfhK/Dc/8Vil+mu15qIisqy/xk/hJ/CR+Gy5+Wue3rgK1n/WW+En8JH4SP4mfVjps3QQY
iZ/ET+K31eKnCS9DtHnYtfhpzG8/s7GDvLbET+In8dtq8dvOCS9a6bB1id6huirtk/ZJ+6R9
W9frKe2T9rnOseFXNNCmYTA2BR/JjALFfhiyjcDZN0JoGJK1zqc+9lPBmLP1Ltg+932NykPM
3picp3Lexj4OveuH4MvWGq7zvc05+MGmOG41BSgan2IcvP9KVG8cOiRiNtn48eK9TzkGFB2M
qa/Xx+xiDqiFsRUKzg/ROV57qHUP8F1ATD/UNzi4IO2T9kn7VqR9rZ7mp+kuhyY98qvCTUon
8YO6D8lZ7501xvmq7rH3kHyTIOd91dFkcnQ9hXOIE5RMbx3UPdvEU81wrRywaaT3fQ+J533B
+s5A7GOM1iWXiwL7zjobHFBnEDZGOQvHhBxT1XffeROz7QeHqvW1YG+yQ3vDoha5NCh8F+yA
pksw0WVTau+7wWUffYwGb6xGxT71eUBB48Zmh+9S9Dl5vGzuTalqaUMc8sd3uEwYvA14xbFZ
4zu8abwoGiTZhelNxpBcshEtkTh9hngzPT6gaO34Jl2HN+OS8XyfvrZrbEJ7CJ9a76Ivr207
NL3Q0DF4+70pH6vtBrSsrAloa5mxXWO73uNDx7sO+HTKm7SdMykEvHHs35XKtUyXczT48IcY
xk9CG3vi2+QXtOmr/PgeY5cTWsc9flKgvZa4X0uZnzI/SEdgAlrvvxI/iV9ImAERIcRVNHs3
oDmCHgc0GjjbATuCOmqvzaBNHCXfdGiKOGhwtoMtnRS5Q6sDwot2zoDuDLZYMrbRhmpDqLPv
R33P3RDMkHrvBpOSp75ntGHi4NBkCgbRrETuPPQeUhWjR+1Yidy5aHq0WNi/gR6NAlnofU7o
mAl9KO2a3KHBhiYTGiL4l9IwSF1G48L2xvtt2dhT4qdM74piX/o28bMpj8r8lPkp80MPv8SP
yWDsmaxDJqnv7JJIyLmN66GaEUl1ZmsxdQFpdB8gw8jj7cGf4840P3VI5AwGbPqQMCIzprKQ
9hATRmfQUZJZ+z1lfqNqogGDzgb09QwOTaJyrWTQ0olDcC6nwHZN7DCqg14Rj+4Zg14PQBKc
tj8DiZ/G/Ep3rLo9XelyNp3EzzGxlPihA770quPoPonfJgq5xE/iJ/HThJcVTXg5+Mxv1Okr
y/z23O2pzG+DM1iJn8RP4ifx2zrxG3sqM6ePzVvhrl7PTUkCpX3SPmmftG/rtG/vkz0lfhI/
LfPTSocim1rpUNZ3aLLnUZnvss+9nuNEGQ35beTcHWV+yvyU+SnzU+a36409lfkp81Pmp8xP
mZ+W+R3llQ7K/NpeTdCyUCrzU+anzE+Z34oyP3YApw6r/90AUcSGKlgdN0LY3BB77XgsCRzq
+kDue2Sws1Husd3OuIrQRew9yM2OsMlQGGUNOw5hs8OyExF2KCrXwq5BuEbGhoYmVmjfJnuq
21OTPbW1p3Y3Kxqp3c14A9YGL82scd9d5jdq2Gp2N1O3Z8vZ3Jy6KfNT5qfMT5nfijK/jVvm
p8xPmZ8yP2V+yvy0tWd7u5sp89OY35xsbzlWmZ8yP2V+yvw2PPPbc7fnYTZ4odxiwzNt7bn2
yx8kfhI/iZ/Eb8PFb8+7m6nbU92e6vZUt6e6PdXt2V63J6ef7OOhDhI/iZ/ET+In8ZP4tSd+
uxvzU+a3PNal5+M4qbo91e2pbk91e65tt+fuMr9Vip/G/DZFPCV+Ej+Jn8RvL+LHA+bX5Cxb
id+mCNYq34fET+K3leJnuPMIFqtHnFcaktRvL+rXxEnuu+v33PN0Tw36adBPg34a9CsiqS1e
eLfVFi9rtsXLKlM/bfGyyvTraF5LqZ9Sv61M/XgLU+bnTRgoDGnDM789i99YUGcarf2ivsOJ
rMRP4ifxU7enxE9nGm2kwB1O9CZM4ifxk/hJ/DZc/DTmN93w9Xj5fnASP4mfxE/it+Hit+du
T0140YQXTXjRhJeikZrwogkvvfFxzSa8KPNTxnd5xjd9Fsr8lPkp81Pmp8xPY34a8zM2BV/O
Xy66GPthyDYq81Pmp8xP+5ut6/5myvymbEePl2eAyvyU+SnzU+a3oswvlmUTfe7dEGLA0elD
aUenrrex99H7YPshj6vjfd8HE9yQ+2At1Sl1LgbvANnexDAuX3cGKZm3Bo8mjZDtI66RY3Ym
VsikbNBs70Oyzo9rNwxeLKbUR9vnrDE/id7lojd9FhI/iZ/ET+K3IvFbn6PcucNP7LJ3UONo
86BeT/V6qtczOevxkzBmbEKidYA266BeT/V6qtezvV7Pfd7YWmvcNdlTQ34SP4mfxO/KxK/V
Xs89D/lJ/CR+Ej+Jn8RP4reu4qchv2mYS4+XD/1pyE9Dfhry05Dfhg/57TnzGwt+1daenHQT
u2Sc83EIzuUUxvHDOPRh8B5jiCZZ5sASmrY/A4mfxE/iJ/FbW/Hb5zG/w4ifDnXYFFGX+En8
JH4SvxWJ38GP+e1O/FaZ+Un8JH597NmTTvWMOVssz8F6mp6nOxPKWN/jjcnZkHdAPNb5oF/A
9UPwpA+h3mIBjh9siuPRooCi8SliXY//SlRvsBIoxoxlPlwehHK9TxlriHIYjKmv12PNT8wB
tTC2QsH5ITrHaw+1DgG+w0Iig6VG46UGFyR++FB9l6LPyVuspsISK3445WM85I/vtLuZdjf7
GrubHbz4jSv/tMxvUwTpIN8HhSqcuMB/F3/iKnxYXHxn/r3s0P++fBn/7RO0ay79O2P53zGw
5SLjdS7+xGWlXAm5wp9r1DLTP3zbrfmMrz8ar0mb/PJ0V38esMDrXv3BiwsXZy2euDgXf88h
Qrv2+YszFo9bPAboGYun4F8eszCLsIiLvOjxFxHHTxGH4NMV+HjszsKjHJ5d7wJc40xc5XCl
Orzu41ALxNGu/0BEPRXI0xdPBmoPee1u8aTFeYuzp+hDH2+wg6udg3/n6/HVnr547OIJiwuA
nLP4j8uegL98R+fh3/FaV528C6brHHvR4qLFifSuUh+v/gyUOB+f0FNxrRJ37X7hEBPxWZyI
+hn87/LHMF2plcdjL8Cn+JVvdmW1OqZc6dqL4w7DtWMOgy1D07/fcBnE88/yV3XJx773+qd8
9T8UfLEwL6345xh3VP+7LV79ejNq8BbE7sBeD7tqKXfKKS8uj+PdAr/eT1wIv/4Gdv1YLlH/
sOyV/XedKws4wr9f9Wr8h+l7e9hS1L3L88vvR8v3oW4prjy9yaEA/GPw3/iRwDn24sWJV+G7
P/5C/OrO/b/UvXeUVNW7tQsoSBIRRREEEWlAcg5dtavIOaNIEhok5xyaIEFyzlFyUkGCgGJX
dSFiVkDMGXNOP0Uxct9n1Vznq3PHvXfcf84Y38c4T8/5znr32muvHehuOb/9f7v3G1pH2OAP
z0X/56ocuXLknpmzUPKabGhxoI9Su3L+1xn7/3v9/M/0Xe/mNmp0jhwnzY20RX24RJvgzQkV
gut6TY89+ly74Kpi+8Irq06NXRdtGuT9Kz2YPXhW7LZ3iwU5Hi4YfDZ8RWz7tm/Co6fdE3rv
k42xVos/CXeueSpc/5VNsXtbbgv3rd8pvLvijli+cpPDL8+aGDq6eVesTt254TI/fR6anHdX
7Off2gdzqrVOb1YnM7bkRPtgSs4bYtWGZsaWftAuyO6yPbbh1ql+X3H29YHN7e0JFeJf9Jzu
5xNnPtpvLGW/MfarfWWxL80hizl0u2+0nbqLZfO/tSv2ZSSU9eq419Nzv5z0ORqcj9VJ3xh7
N/xY7HKzdvExC8fHGjS8JX7rLdfG87RfEetTpUJ83JnW8XqrJzKHuK2Jm8OLn9WPF72lWfyn
m6bGJvZdFR5wqF28ZK3xsceG1A1KLWser//zlFjvKhWCfrZtU9u26uBLoSJj2sdrrhkXW1En
X9bRTe3jl8eMi63669PY1s+eit2ye1Pszc3bYx0id8cKFt4Ru/7rubGBPb/Lev7vnbFPDkyO
Hf9sRtbG9e5YYrPWXpXGsSgPkas/RL/GCTMOx8s5q9hznd9XmH3pGAOOcdPfK2OrD7cL0mqO
98fozrvNP97lTOugo81/2tq68Q4Tmwd/XZUZezj/L1nfjmkfzFo9LlZiyHWhfpvaB+Gx42Jd
+h8LF2/cLti8ZDzrFky0bWvbts++UT9YXqZZMPO6qTG73uJ2vcV1vcXteotxvdn1ELfrIcz1
wDnhGvviqS2x96zfroHgS7sG7PqJ2/XzJNePXTNxu2bCXDN//dQ2Pv3ovnCPIsNi/z7ZJv7G
sb3hw126xHLObR2v+viecO61odjAP9rG924+cwf5A0+1cZ78xq9bx8c2/zBGfs+xVvHg1/dj
5Pf/29LGKRcnP/ByCxsnLU7+7agm8Sl76rp8SfPG8ZXL67icjM/oJ+Mz+hmDscgZg7HI2Sf7
Jmef7Jt8VJGrdjFXcjxzVX84pT/s+238IGX8wI9v8wlS5hP4+VgWpMw/8PO3MYKU4w388do+
g5T1Cfz62ByD2PjVu5mnzTHo1uDYbuapfrf+Nkf63fpr/IB+myPjB/RrPi63OTIfl2v+Lifj
M/p1vC5nDMZKWR+Xs0/2TW5rWJa5st/8b91Rlrmq382VXOvvx+d8+fE5Xy7X+XW5zq/LWWPm
yjissZ//J5uax5edLBvYPmPvHmgcv+XTGs63rNHeXXtcqxdKto3v2/BRDN+lemu7hsvH8a03
No33zarnPEpNzuf04dmO7fFcJ4yrPOxz6w98v40T+HFMAz++fR74/dp2gZ+PjefOL2Mqd/eX
+gNyjeO8xnde+3XexmM+znP/Ma7m6cbF67hcruN1nvkyLj1tG6THl28KuzX8+pFq8dMvN3He
1jj+y6bmzr8za1vshz6tnK88qVN6kYWtnb+04eHw+FAyn2/nJKz+tz6qETz2aGPX8+HycHC2
abrz+c83Cc7trub8P9a7XOfxcrhlkH7s2zDntPC0VsG8Ouud/2BB6+Chqr2eJP+qb6vg7cHb
uNZixxu0DCrN/c756stbBNPezBcnr1i3RfDeyRuc/0/eFsHBo8Wcr/6f5sHv1Us4/8c7zYPP
3i3p/Nc2B46TbU9Oaxxcrl/T+SUN04M3Voed7/plteD04SbOc919bNcf/RNu+zr8ZouWzj84
bmV40bJWzqcXvj7rTns+0lM0OBzrXD6Z2/rEm2jbQbEa8UKnG7uep4eE40tHpDt/+Ykm8UJv
VnP+++R17vx3PVrGFyz+zB3vP3tbxT+fs9D5KVNbx/N8MzvEvhb81TI++Z+sMP7rP+bFxhaa
/1++39EFrv/d8PzwwI/m/5f3PXzzwveB/BwM+KsEnp8HqFG+rQM830AC/hp5lO/Q2C6fwWeA
zy+PFpBH+bka8NfKo4XkrzP14+D5jpcaZX+A57swPMp38nCD4XvwNwo8n1OjbINHiwo841Kj
7BuYq+/B36Qa5ecfwBeTR28R+OIGn7NtCYHneKnRWwXfXvueUubZDvC3GeyrtOHng79dNVpG
HvXHjr9DNVpWpCmjD19ONVpeHq0g8PzqghqtKI9WEvjK8mgVgednCfqqGX5MfHXVaA151F+T
+Jqq0VqCa9f3cI36MfFcp9SoXwd8XtUo10lto47hzxfen1N8XdVoaYGvJ4+y7oBnrQHPWgPe
rzmetQY8aw141hfwrC/g2R8eZX0BX18eZX2ZbwODzyDd4DM0JE+N52cwPMpPWoCPyKP8iA74
hvJoI4FvLI82Efim8mgzgW8uj7YQ+JbyaCuBby2PthH4tvJoO4FvL492EPiO8mgnge8sj3YR
+Lvk0bsFvqs8eo/Ad5NHuwt8D3m0p8D3kkfvFfje8mgfgc+QR/sKfD959D6B7y+PDhD4gfLo
IIEfLI8OEfih8ugwgR8uj44Q+JHy6CiBHy2PjhH4sfLoOINrlWuXaxTw4+VRrlHAc13yOdc8
NeC5D/DoBIGvLY9OFPhJ8ijXLuC5Xvn8FtVk+OKq0ckCX0wenSLwmfIo1zTguY75/CbVZHhy
wE8VeJ7/1GgpeZTrHvAl5FGue8BPk0enC3xJefRWg1687yObIfCF5NH7BZ6/v6nRmQI/Sx7t
KvDdDD4vYFADPr88Olvg88mjOeXROQLPH2r+PCDwc+XR3gKfYfAnl0ENeP5+waPzBL6mPDpf
4BfIo9xjgOe+4nP+/qIGPDngFwp8dXmUvxf5DB0s8JXk0aECv0geXSzwVeTRqga9eN9HtkTg
K8ujSwW+vjzKfQv4sQb37TJjjMBz76PL5anxI6Qr5Knxw6Qr5anxQ6Sr5Knxq1Wj/jmGX6Ma
HSDwa+VR/5zEr1ON9hX49fJoH4HfII9ulEfvFfhN8mhPgd8sj26RR7sL/IPy6FZ59B6B3yaP
bhc7lNGH36ka3SV2K6MHf7d0jzw1vot0rzw1vpN0nzw1fr9qtIPAPySPthP4h+XRR+TRNgJ/
QB5tJfAH5dEWAv+oPNpM4A/Jo00E/rA8ekQebSTwR+XRqMA/Jo8GAn9MHuXeAPxYY7Qx0lgq
8EuUDZenxi+WDpXn/ud5sdDIMOYa8wyeM/2M+QJPjmbI87zrZTwg8HOMbsYsY7ZB1sMgBzw5
Sh+eZ/ddxkyBv99AO8tT42dIO8pT46dL28u3NW1tTDWaGpOMyUZLo7kxReDJUfrwEWO8McFo
bDQ0Jgo8OUof/phx3OBcAH6FPDpO4JcJ/HKDbTm/bAP4E/Lo4wLPNU2Ncq3Te9TgM8BzbeHR
wwbX46Py1HiuaTx6QB714+C5T6hRvz/uOz8fPM8RapTnC/crzw0+A/xWeZS+vcYug17A75RH
eb7Qw7OCzwC/2+Cz7YbfFs8+2DfPPT83/BOqUb+2+FWq0ZUGvTw/+QzwPGfx6AZ5dI3Ar5dH
14m1yuhbbTAG4P3+OO/M5zUj9c/pZ1pwOeXIvnFq4pcDNSM5VlbKGlxkWqLpqIqRFydUioWH
TkvcluMq1zPr8+mJsgfOBxeWVsp67OEZiT6Vngxer1kpVuT7GYlvJqRFnlxRKWvNzmmJKVPT
XD/+1zUVI+d35Agzzi1HbXz7w/j/fFYvMnLJI6Hdb0xNFP8jV2Tt8kpZjP9M/HxAD+Ov7JQV
7F9SKcT4FQ9td/kfde5P3PCfuc4fGnd/gt7kH/6Lpf8zM5FVcmls5dpa8ejj9ye+3Vgqa/3m
7XG2LXpf3wa18/8W75Y2I/H52R+z7ilULPvh8tMTX+b5N/RY67Rs5ny2TIUGg5+pmM2cC75a
Kjx5WM1s5jzz65tDz6YH2SXWT038Vej2rEdPJXv+ab03q+qRpB+RWT3rnemNs891nZpo0KxM
1q6nWmSzth9vuTHr86vaZX97PjNxZkrJrGP/XHJz2FC2Q4O8h5Jza7N7TvjpPnXcnG+4/pFw
uV8rO//26t7hQqfqBxzLrMefCj90ZkrAsff58khoedvtQcpxBRyXjiXCsbz50uHQ4kcrRjiW
m/aXC/Wf0TjC3B46uSPUvkoQ4ViyiqWFukxMc/0b8px7YpKdP7bVcblttSbOf93m2ljtzJoR
1uT1L/rFXr096UfvbhB66fIlN4eJf+/OyuiRnNveV8bHmg6a7eb8xKtfZ514IuKO5dgzLbJ/
OrOmgVuffTWz+2SNCTFmcKRm9qgeS9Lx52cVyX5yQ63wS92nJ9YVL5Z9z7CzIc7XyP5Z8QPf
XZPOtdGk2fb4gF5PhFiHN1Zsj58d2sz53Y9ujw8ve+4kuXqyUnqcX90tK95tTT53jd1zW+ns
G/auzkp7Z1qiyNKbs79aOSjGvtodrpl96YUX3Xwy3qqX/WPfD7O4bn/K0y572b566ZzThkbV
tKuDwwNbR6rPz0ycLVYwmLKvQ+TLPZmJEaVmh1N8zPlBmYnPGuSOd27ROfLHmaGJG9fvyi7Z
eHyk2ftVE6M3VE00PTc3MumV3dmPLhuaIN9z9ob4E30yE/SfL7k9tmJHZoJxWpRaEl62O+lL
/ZwrKDEk2TPlyZ2R1t8mt10/r2q06A/JMS9sHxrNO3C329ey/pnR3/oUcHO4dVdm9IZS69zc
bt6bGV19YKabc5uhmdG79ucI2O/d7wyN5iuzK8J8Pr1SNRofXzXKPFf9uyvy3dGhUfIj+68N
mt+XGaV/1/Id4bt2ZEaZ56gDi2Kndyd9vZvzxV8dkOxZsXBX9l3PJbf9uF/VxKHrq7kxOywZ
mvj93d1uX6uPjEs8/9XKSGbhL4Ir3TMTnz63N/zKF3dF/l04MVF9+eTw+4cWRp4uMjXx8+C/
QzzPLhTLTFy+NCS2q2yPSO7KExOhDbNj/ZouidRfNzXRpe2V2C+b0yO/LMlMVO+bM87cLvw1
PPF16Fj229uvjSw6VyFR5qnKidv2PBT56ZMqiXdnV0l0un1FZN68fdmXXh+W+HruPZEySwrH
z7w4NXHs7jqRHBcvxWquSK7/4T/WxM6fnJwYvm9MpN3vq2L3XjfJnceGlWaHnvgl2X9k5ZzQ
2YPJ/m/qLwlvKTo5seW6aZHnP/44/MWaZL45I0/QeVHSh79fHblu7gg35jM/fx/+7edpiVKf
FY8Unvxg5MGv+iamh05EbhiRFi34c8Q9dy9+UTFaoUOlRM6S+yKN3hseff2L5HFdd2hqNF9G
gfg/l+tF3jg8MVpj+SOx8IAFkRXB+OilkutiF0tsjBwqMjW682COGGv4zS2Z0UcmdA2zhs0r
T4zOs+uBNTy2dmq0n10PrGHnpZnRruZZw0bFRkSL730swhp++HWFaP99laOsYfFbq0ZntKoS
ZQ1fargv8vyTw6KMOeTbwsHSF6dGWcOTnX4Pv7U8eW30b7w+POnk5ChreKLpxvDgQpPc9XBL
3xlZ2b8k++utmZr17sFk/8mVi2JvF50cZQ2vGX0x1mBtMj+9L3f8+KKkv/vF1dnTF41wY444
/3Xs+/9Mi7KGt933YHaDA/2i+SYfjYTblEssXR9EqxWqHomfqZioNqZSlDXcnj08MX3acXdc
p+ZHEnlX3hRtlm9n5N3MWokTP9aKts//W3Ds22sSpX5sEa3bd3/k9v77si9+Ozr61YnDwY/N
J2X/2WpM9OnRwyPTvv47lnPFlOjsf/tGFtebHrs6z3Q3h0FjIrGJ0cwo19XNzy0KVygwNcr6
39hkV/j3l6ZFe1YvHbmpdv7g4OtTon+f7hVZ8vKyyMp2I92xVOi+L7L17lFR1nzK1Juiz2+I
uLmtvKV29N2Oybn1fLVFNOvoNe5cbMs7Jjro5n2R1n0eCTpNHxP9+bbxEeb2zaHMaDc7j42v
aRcp3jYz+u3Fb9399Vz96dFNdt5fXFc00rFhZvTcykph5jmz4NTomgMz3XVyNpcdhz03WE89
K9zzpNrDmdE/7dnCmOvnZ0Yvm+c6GTjL9nXzTc7bd95R/zd2r952LVnOc2PRkyOiOdesyuYa
OPvRyOiQ/PuyGf+rtZHo3bNvTmTW2xrpsb1WtMWLtRKs/1tf540+OLeFu+Z/37I3MvXf0Yl6
hU4EV56eHJlRY0yCY8zzTL6gyCOZCeYzL9d74YHjks/Jr3esDN/VYXoi68cikcXD08Lz5k1J
PLq5f6RM3pWxWi9NTXC/jD20OvbC+uT3NXV+yhuv+OeUBNfwwxlLs1+YM9Ldm4+e2pc9uNeo
RJ4/8kdGvVA0caFsNMF1UunXWol+E5Pz7NKgRWL7pbwJrpN+741OTB+0L5t5bksfk6hdd3I2
8+w/NjPRZM1HMdbhoZnTEzcdtuvbzm/s9OREnWjuGGuyrPy0xPPT5oS5Vtc+OyVx7tjB8M8Z
fdz3Vsn1nBnNaSaXcZVxtZHbyCOuMc0r8pnmNwoYBY1rjULGdUZhcb1pEXGDKdxoFDVuMm42
ihm3GMWNEsatRkmjlHGbKG16u1HGuMPwYzI+lDXSjHJGeaOCcadR0ahkVBZVTKsa1YzqRg2j
plHLqG3UMRivrlHPqG80MNKNkBEWfBPJonERNjQaGY2NJgY/kzUzmosWpi1FK1NoLdqYQlvR
zhTaiw6m0FF0MoXOoosp3CXuNoWu4h5T6Ca6m0IP0dMUeol7TaG36GMKGaKvKfQT95n2NwYY
Aw1/fIPMDzaGGEONYYY/RnS4McIYaYwyOF5/rOhoY4wx1hhnjDcmGBPFJFPWYLIxxcg0phrT
jOnGDCN1HViP+42ZxixjtjHHeMCYa8wz/Jqg840FxkJjkcH6+LVBFxtLjKXGMmO5scJYKVaZ
ZhirjTXGWmOdsd7YYGw0WDvYZGw2thgPGluNDGObsd3YYew0dhm7Dfa/x9hr7DP2Gw8ZDxuP
GJzfA8ZB41HjkHHYOGIcNR4Tx0yPGyfE46ZPGCeNJ40sI2bEjWyD9U4Yp4ynjNPG08YZ4xmD
8/as8ZzxvPGC8aLxkvGy0cYYZrxinDXOGeeNV40WRkvDX1dcY5BhcC2mXqN4jhFSr2085xz8
/cC9Acy9o9HO4FoDfGuDeQH+wv/B1M1pz8Bcdo0PnZh+7cKsIEfBDQ1W3LgyyDhWKfTGi2eC
50d2C9+x42Cwv/Nj4X9u6BW8PTIr/Em39cHkw/+Go+NnBbdeKhxcyNE7ONa7YFCl57DAliLH
mqc6BTn2T60/9v07gxzLlzYo+unf4XrL6kfY/syR9hHq7WMaRcp9NifM+Cj7v7ygWLhMrvYR
9MlWbSOjLm0Jsb87c38QZn/vtykeTC9TLYI2y6oY8fut9E4NN4/5taLBTx8XCSrbvwHMPNQj
+DB8t9Ps314OH22zJjjwzL4GZW47Fkz8Z3Z40eqs4G7b5zebXgjYz84fng7KFigWmvFs7uCV
QwMbcPzkhzefCZUqkTNUuEKJMP2Pt65u45Svv3zVPe5Y607dHpxu+154xZ7lQa2OtwT9Li8I
fr6+RnB51byg7iORYM38uW4+1GUW9nafDy4zPHi0bbEI8+s5LX+E+kzaNZFOv89y+dFfdwSf
TPgn+PvZ9cFvr34dnHv3YJDzr7yRN8qdDap2fT3gvCy795Og28GXg8IV3gvemvdi0G7HDZHa
c88GsyaXjFTedDa48GyNyJ3fvxKwzpy/As2bRejvPrJV5PqPXghYX8Y5sqhehPPJunI+P7pY
KcJ57Pv5+YDzsH7FuWDsTb+F2S/rwXxYv5zFzgVf3DPOzZPjP1EzZ/L82nGwDhwX61D4UIEI
63C6dkGbV/vg4OLNAdcB68Xxsn4c583vnHXjcX44XvbP9fh4gVeccp6Y75LLZ4NnxrYJSsw7
Fwzquzz4s3K1yCt5Noa+KlY9suuOk6GXGzaLtDyzJjT2j2qRUvu+Cv37TrVIu6IFw6+WKeFq
lPqx4/8GfL4u35WAuuS3n7j658GfunrnL++6+j9T33P1u8tfd/W+Mm+4+rdmp522OHva5S+/
+aTTy92edHmdgttc3fmJra5ecrm9q1H21+tIIsz+v8rxVJg6b6HbXb3/77Kuzth9OsTnDae/
FOLzU+fquzrjzjauLjchuf+J/yT3/1fuLDd++QXJ/Q8IJfc/+8vk/r/r2sF9jjLerSNPJfcX
T+5/5vwyrq4wsZzbf8f1zyT3d+vZ5P6PR5L1dZ1cvXNLS7eOQz5t6db1wJdNnZ7e39TlGbnq
uXrU23WTfenJ9R9iyv4//Sy5/s/WT65/2+KfuvmV3pBc/1fLvOfqMo8k1//lk8n1f6tTcv0f
mp/c/4WXkvtv2LlpxP4dVzhrcwunDTuXjYQe3hTifHNd/N6teKTUv5tCN0bzuOvlfN9/A/JH
8n0ScL20HPGJq28Y+K7TT597Oyi/fWHolhdfcDXXHzXPCa63z594zem5319zn7/Z82mnPFe2
1NoZ2n5Xlqu7DtjmlOdPpMzeEOef/fL8GDtif4jnyfJb9rvnzpcl94XO980O83nGbSWd8txh
PJ5DOTpvDnW87cmQ+9yeT8wn42yaq3MvTu6/zp3PuHmO+DLLHdf5Ocl5tFyenMdzieVu3ntv
HB+wPlwPjPdAtbYB6/PT8t/DHN+KUgm3/8tTS4RZn4sbSrl6dHbM7W/0ezvd/jv3bevWl+cJ
8+H5cqjHxlBGtTtCTm2ejL+qfCvXx3OI41lXrpmrO1eu55TnFevD9UE/zzHWh+ca68Pzj/U5
vTh53iZvSZ4vnoOMx3OQ9Wm8Nnn+eF4xnyvlXnfHt6FIcv+HP27l5rmkdWt3nYy9+52A66bE
1g+dXir6mdNJra9xn5cueGvyelpS3Wn9Qcnr7Njh5HX2Ra/kODNtroxzcds/Tp/vX5F/Sxh+
/t+jTus+eZUb9+RznZP7m7fc6f6Xdjo9tfaA0/mLjjj99upjTmNNjzudu/GE0y75n3Qaeu6U
00cvPeM04+wet98Vxy87rV/0TrffCi8fc3pX0zyu777C3Zz+umy10zveO+n09u7J8eYdSY7X
6vrkuvzSPbkuz3zxqevLUeYfp8N+zufWo3/oNqd5dtV0etNfLwX3t1sXLAovDDYWWRjkeOnF
4JdHTgbs5/zmF4NDrz0ffBM5Fdi/vw2Wbnkm+KdzIihU84XghvjLQebfvd12Y4L8wYpuBYK2
e/MHzHdUkTnpzP/XejvS/2j/crD29XzBmAMvBWf3PBFm/BfGlA9f6fkCf0+FmP+bi3eEOJ7y
A4MQ+y27/ko6xzugy6PprMdr77yQnqPZ2+mrHjscPrXysfRnXvgnzHrRNzPfH+nlRg8Lzwy+
T6+2eGGY9RzQpWpo+5HcIfaT4+mcofqXG4czxuUIPbC1XZh1v1hlRWjmJy1ChYp+GjrV4t/0
/A/eE7bve9L73NnGHQfrcPhIm+D21S8Hd/ZaHrBGOXYdSh9TYmnAPN6tvzNgfNaJebBOF7+u
GVpWKhGcGr86dGzMmSDHX1+F7t/9fNC/3y/hnt/a9vbHvnVzP3Pbt2/OX2UK5FfLo7kFPo/A
XyOP5jXYLp/BZ4DPL48WMAoa1xqFjOsMssKqrzctYpDfYPhx8DcabFvUuMlgn2Q3y6PFxC3K
6MEXF3h6qFG2waMlBJ5xqVH2DczJ9+BvVY2WFPhS8uhtAl/a4HO2vV3gy8ijd4iyyuhLM9gO
8OUM9lfe8PPBV1CN3imP+mPHV1SNVhKVldGHr2JUNaoZ1eXRGgJfUx6tJY/WFvg68mhdga+n
vL6pHxPfQDWaLo+GBD4sj3IBQ0QZfVHDj4lvqBrlmADfyOB4uWa5RhobTYymAt9M4JvLoy0E
vqU82krgWws8P+MBvq3BuvMzIGsNeNYc8O0N1ph+1reDQd5RHu1ksMbMobPqLqZ3Gcz3boPP
oKtBzz1GN6O7wPeQR3sKfC959F6B7y2P9hH4DHm0r8D3k0fvE/j+8ugAY6AxyBgsjw4R+KHy
6DCBHy6PjhD4kfLoKIEfLY+OEfix8ug4gR8vj04wJhqTjMny6BSBz5RHpwr8NHl0usDPkEfv
F/iZ8ugsgZ8tj84R+Afk0bnGPGO+sUAeXSjwi+TRxQK/RB5dKvDL5NHlAr9CHl0p8Kvk0dUC
v0YeXWusM9YbG+TRjQbX6iajm8Bvlkd7CDzXJZ9vMagB/6A8ulXgt8mj2wV+hzyaIfBcr3y+
06DeZew29qjea7rP2K/sIXn0YYF/RB4dLPBDDT4/YFADnhzwBwX+UXn0kDw6XOAPy6MjBf6I
PHpU4B+TR48Z9OJ9H9lxgT8hjz5uPGGcNJ6UR7MEPiaPThb4TIPP4wY14LPl0YTAn5JHn5JH
Twv80/LoGYF/Rh6dKfDcP3z+rEH9nPG88YLqF01fMl5W9oo8elbgz8mj3GOAX2Tw+XnVZHhy
wL8q8Bfk0dfk0SUC/7o8ukzg35BH3xT4t+TRtw168b6P7B2Bf1cefc943/jA6C6Prhf4DcZG
40ODe3qt8ZGxWnpRnhq/UvqxPDV+ufQTeWr8Uumn8tT4z1SjiwX+c3l0ocB/IY/OE/gvjbnG
V8Ycgf9aHp0l8N/Io9/Ko/cL/Hfy6HSB/14e/UEenSrwP8qjP8mjUwT+Z3n0P+IXZfThf1WN
XhK/KaMHP1H6u/wE08vGOOkf8tT4MdI/5anxf6lGRwn83/LoCIH/Rx79Vx4dJvBX5NEhAs8P
GtToQBPA5zQGmM1lep8p4K9Sjfa1DPBXq0Zzy6N97HPA51GN3msZ4K9Rjfa0DPB5VaPdLQM8
98gaY5XxnsC/o2yFPDX+TSn3N577n+fFqwbPrGeMlwyeM/ONswL/svGAQR89M40ZxhmBP21k
GjEjYZBNM8gBT47Sh59sTDKyBP4JY7wx1nhc4I8rGy1PjT8qHSk/3HSocdDoZ+ww9hmDjUHG
wwK/3+hv0EdPL2OzsdXIMHob2wWeHKUPn8/OQ36jgMAXlEevFXj7H8Fw4K8z2LawwTaAv14e
LSLwN8ijNxr0FjX4DPA3yaM3G8WMW+Sp8cVVoyXkUT8O/lbVqN9fSfN+PvhSqtHbjNLG7Qaf
Ab6MPErfHUZZg17Ap8mj5Qx6yht8BvgKBp/dafht8eyDfVc0/NzwlVSjfm3xlVWjVQx6qxp8
Bvhq8mh1ebSGwNeUR2uJ2sroq2P4MfF+f5x35sMfibtX7G76r3+r8L8+S/67kFyuO/m9ie+7
StsnP5sZRX0Wcv3J8a42z2fXKKPHZ3jGo85t+M/I8D4Lm/d9ecz5fjJ6fBbQpvHYH59dR2QZ
PT7Dk1HnNagbGr7PZ1FlrFM+g/4nlTEHn9HPttT5DeqTBhl9PuNzMuoCBjXPFt/nMz4noy5o
+H7f57NraVMfnv4TRJbR4zM8GXUhg/qI4ft8VjolY93ov0UZx+Ez+tmWurBBXcwgo89nfu1Z
NzLfTx/19cpvNiWjz2coGVrEQIsavs9nKBl6g4HeaPg+n6FkKJ979X0+a2if+fHIwO+XOfj6
JvP0+XlR++NI7amgPo6Xcejxa8V6kFH7debckFEXN9gHGeNT32aQ0eOzEsr8HKhvVeb3SZaW
0sc+6dmhzM+LrKQyPy/qUil9zI2ssTL6mBs9W5T5+ZNtUsZxMA+OobTBcTBnn92hjOuJrLRx
u0EfGXOjPmSQ0eOzMsr8/KkPKKOP+ZIdTMmYG/vcp4y5+KysMmrmS71HGX0+262M9SttsMZN
DX+OSpsjK2eQlbavHAN1c8P3+ay8MmrmS91CGefSZ/664lojo77TYDxqjou6pUFGn88qKqPm
uKhbKaPPZ5WUUXMM1K2V0eezysr8cVK3SenjWMmqKKPmuKjbKmM8n1VVRs1xUVdTRp/PIsro
41jpaafMrwdZdWX0cKzUHZTR57Mayqg5VuqayujzWR1l9HFc9HRSRo/Painzx05dO6WP4yd7
Qxl9HCs9bymjx2evK2MfHBfzOKeM+fmsrjJqjpX6FWX0+ayeMmqOlfplZfT5rL6yq5RRN0jJ
6CULK/PrRs8LytiWdSJLV0bN8VOfUUafz0LKcimjPq0styn7ZZ+BsjzKqP21QcY1Qx01uBfy
2lcy6oYGGWvOejYy1hhkPMN81jglo5e+jcq49+mjp4kyatadurMy+nzWVFlpZdTNlNHDuaBu
r6y0qc+aK+MZQUbdQlkZZdQtld2hjNrf59zTbEvd2uB4uX/JqNsYZOXsKxl1W4OM+42M2t9v
3Ftk1H7OZBwLdQeDbblnyKg7GmTUXD/UXQzf5zN/b3F/kFG/Y9DHOnNNscarDD+ez1amZFxn
jL9UGWP57C5l1Fxn1Kl9PrtbfdRce9TLlTGez7oq89cn9T0pfVyjZPycwpzp4xqlZ4VB5q9j
sm7K/HVM3V0ZfVzLZPzsxLb0NTToiSjz1ztZD4O+hva1kUHd0yCjz2f8vOb7uL7pCSujx2e9
zNNHzTVPfa9BRp/P+BnQ93HN07OByPro8VlvZf6+oO6jjD7uDTJ+DmVb+rgP6ElXRo/PMszT
5+8V6r5EltHH/ZJh8DOc7+N+oae+Mn9PkfUz6PP3FPV9yujjviLjZ2Tfx31Fz3aDzN97ZP2V
+XuPeoAy+rj/yPj5nW3p4/6jh3+rSObvUbKBRJb5e5R6kDL6uE/J+HnQ93Gf0rOfyLb19zLZ
YGX+XqYeoow+7mcyfp/AtvRxP9PDz59k/p4nG0pkGT3cz9TDDN/nM3735Pu4x+nh510yenw2
nMgyau5x6hGG7/PZ1dqWPu5xevh5mT56fDaSyDJq7nHqUYbv81kubUsf9zM9/NxOHz0+G01k
mX8OUI9RRh/3uOvRtvRxP9Nz3GBb/xwgG6vMPweoxymjj3uc7A9l9HGP08PvGBjPPwfIxhNZ
5p8D1BOU0cd9T/abMvq4x+nhdwtsS4/PJhJZ5p8D1JOU0cd9T/aLMvq4n+nh9ypsS4/PJhNZ
5p8D1FOU0cd9T/azMvoyDHpOGWxLT4ZBlmmQZdjXvgb1VMP3+ewHZRmm3M/08Lsg+ujx2TQi
y/xzgHq6Mvq4x8m+U0Yf9zM9/F6Jbf1zgGwGkWX+OUB9vzL6uMfJvlFGH/czPc8r888BspnK
/HOAepYy+rjHZxpfGeyXPu5nevgdGJl/DpDNJrKMHu5n6jmG7/PZF8ro4x6n57wy/xwge0CZ
fw5Qz03p474n+1QZfdzj9PD7OvZLj8/mEVnmnwPU85XRx31P9rEy+rjH6eF3emxLj88WEFnm
nwPUC5XRx31P9pEy+rif6eH3g2xLj88WEVlGzf1MvdjwfT77QBl93M/0vKfMPwfIlijzzwHq
RtovfdzjZO8b7KOufQ0ZS41lhs+4x6lXElkfPT5briysjHqFsogy6pD220AZY60yGK+OfWU8
6tWGz3iOUK8hsj56fObHq62MnrUGfWQ8R6jXGWRs57NAc6GPZws9Gw366PHZemWNlVFvSMno
JfPf+zQ1z7b01NM+blHG+JsM9lHcvtJHvdnwGc8q6i1E1kePz/x4xZTR86BBH9kUg3qrQcZ2
PmugudDHM42eHQZ99Phsm7KWyqi3p2T0kvnvfVqbZ9vtxk6D8W6yr2SMn5rRS73L8H1TVe9W
Ro/P/PcvtymjZ4/6Simj3puStVW9Txk149Hjxythnpye/QZzIWtvUD9k+Gya6oPK6PHZw8qo
eTZTP6KMPp/573NKWkYvPX48MvrIDhjs91b7Skb9qOGzGaoPKaPHZ/yOn75Cyug5TKTsftVH
lLGdz/hvBfRdq4yeo0TKZpqjfswgY7uZBhn/zcH3zTJHzwki65tpX312jMiyrsqojxMpm2mO
zH+P1M0829LDf6+gr4B9JWP8xw2y/PaVjPoJw2ezVZ9URo/P/Hj5lNHzpPrYFX3UWSkZfxdR
x5TR4zP+ew375SsZPXEKZQ+ozlZGj8/47zy+b645ep4ism3p8VlCWW9l1KdSMnrJ/PdIGebZ
9pTBf79ivFz2lYzxTxtktewrGfXThs/mqT6jjB6f+fFqKqPnGfWR8Xcl9bPK2M5n/Dcz9kEf
fy/S84JBRo/PnlPWXxn18ykZvWT+e6SB5tmWnhcNxqthX8kYPzWjl/olw/ctVP2yMnp8VlZz
rq6MnlfUV00Z9dmUbLDqc8qoGY8eP14l8+T0nDeYC9lQg/pVw2eLVL+hjB6fXVBGvdigfk0Z
fT7z3w9VsYxeevx4ZPSRvW6w36r2lYz6TcNnS1S/pYwen5XRWlVWRs/b6iNbqvodZWzns9La
tr4yet5VH9lo1e8po2Zbevz3UvSNNejhv+sy53H2dZnxvtFY2ZiU7APz9I1SRv0hkWVst9yg
bqJt6fPZR+bpG6GM+qJBRs8K46Lht6XPZx+bp2+YMupPiCyjZ6VBPUL7pc9nn5qnb4gy6s+I
LKNnlUF9n7alz2efm6ePerVBPTylz2dfWE7fIPtKRv2lQUa9xqAepm3p89lX5ukboIz6ayLL
6FlrUA/VtvT57Bvz9N2njPpbIsvoWWdQ+23p89l35unrq4z6eyLL6FlvUA/Rfunz2Q/m6euj
jPpHIsvo2WBQD9a29PnsJ/P0UW80qAem9PnsZ8vpu9e+klH/xyCj3mRQD9C29PnsF/P09VRG
/SuRZfRsNqj7a1v6fHbJPH3UWwzqPil9PvvNcvq621cy6t8NMuoHDeq7tC19Prtsnj7qrQb1
PSl9PvvDcvrusa9k1H8aZNTbDOqu2pY+n/1lnj7q7QZ175Q+n/1tOX3UOwzqe1P6fPaP5fRR
7zSoe6T0+exfy+mj3mVQd0/p89kVy+mj3m1Q90rp81kOZXerjzqnMnr2GNR+W/p85n+31EUZ
9VXalp69BnVPZfT57GplnZRR51ZGzz6DultKn8/yKKPeb1DfndLnM/+7uQ7qo+bfhLEu9Dxk
UHdWRp/P/O8J2ymjTv67lJlReh42qFtqW/p8VkAZ9SMGdaeUPp/53222UR81/xaK+dFzwKDu
qIw+n/nfs7ZSRn2d+ug5aFC3V0afz/zvfFsoo75effQ8alC3U0afz/zvn5spo+bfPzFneg4Z
1G2V0ecz/7vwJsqoi6qPnsMGtd+WPp/dpD7qIwZ1G2X0+cz//r6RMmr+jRfzo+eoQd1aWaOU
zP+3hKgyav4NGNuy3WMGdStl9PnM/3eNQBn1reqj55hB3VQZfT7z/42lvjJq/z3DWGXU7h9A
2VxGWrbU4HsN/70K2RKD2v9+aLgyav/9ENlig/oOg2PLsK/zjDSrKyjrZ/V8g+9r/ffKZPRR
+75eVj9g3GlZRW1LNsegrqysm9WzjUpW+9/v9lAfPVXUR0Yfte+7y+qZBj+T+Z/zyO43qP3v
xzsro/Y/S5LNMKj97+U7KqP2P6+STTeo/c/JTa2ebPD7jnSDtWpuX6cY/N7B/y6DjD5q3xex
eoLB74Yi2rah1RONsNX+9z5k9FH7Pq6L4wbn218vXAc+a6jxViijHqGMPnKyRsrGKaNurGyZ
MuomyrhO2Qf7bJaSnbCM2l/39PisufqoHzeoWyijz2d9lfFMpJeeTikZfWT+ecozloy6s/qO
Ws22zMPfv9zTZNT+eXBYGXUHbcuziZxni3+u8awjo/bPSZ6dZNR+WzL2Qd3R4Drg+UxG7Y+D
v1OYM/Ptor4HrSan9t+DkNFHdpf6tiij9t8PbbOMv+P4u623+sgYj8x/X7JVGbXfxy7L9hr8
/en//iVjPLLuBsexUxl1D2U7lFHfq4xt+Tudsfz3AtvVR4+fH9/XcWwcQ4a2JXvCoO6vjB6f
+WuD64WMup/6VimjHp6S0Ut2n7KVVpNR+3thk7ZlnwPUt1EZ9UBlG5RRD1K2xjJy6sEpGfMj
G5aSrbeMniEp2TrLqIcqW20127KdP46cV6788cuVKx/VfYu3qn57Zdu3Jn8af11J/EvUYNmn
9ZftmsxX93+Lvqyw7K/En1eW/3ll6Z9X7v/Xmpr/cyWlvP/SlY/YnD+/9HFy5Ucn2/Z+3Wl3
i9U7h2Te2GJ16ZI5Ft2Vr3Pp1ms+qZDjxnwXdrp/bmKzc382LNja8LFNpRpRLEhG9vV/5mWC
/zX8/6v5X/u9NaWHVXUrm5L9d5vHypcb89jPPTNnIfdSxhwNLePBzJ+8SXFf//d6teK6aclf
VRywuV//WcN4zTcfDC/v8WD93H1nxQzn32obsbxkQG4at9r5k2mh+JMt73S+9MZaccN5y+L2
mfMLrm8c7/Dip7tSxozJh9kHvsWXj99BX3L8B8PMA6/5uB7NQT1uDs5rX85rDs5rbup/MObH
5DgYi/E5Do5H+zL/oNsXx8T25BwT4+I5JvaHt/kGDYNKe/Csk1+ryh8fL8tn5Ixn+3Ue9Wur
/arHzcd5je+89uu85qN+tz7Op76yLfU1VRf+bRwvsHxbeHX50lmrqzWN2/80wh34r+o0jp/M
fj2G75XR0Hpui+OfLRSKnzxf1XmUmpzP6cOzHdvj7X+WYRfjKg/73PqD/+o/XzXw45gGfnz7
PPD7te0CPx8bL6iRt/IexlTu5q/+gFzjOG/jMb7z2m8yz36d+Thvr5wsy7iaJ/P3/RxXMk8e
r/PMl3Hp33hDED/5WPXgny07s3LdFInX31MjWP/xS1mWxe0zl1sWt89c/mmL2+Mfj2vs8o5l
y8R3TW/i8rn534rNaN/U5UOrvx17oUczl9s5Kbu1XXOXN84YUHZ3rxa+P5zSH/b9Nn6QMn7g
x2eOKfMJ/HzIUuYf+PkzBmNxXIxhc3X7ZZ821zA5+7S5hjle5hgbf8MecuZor+7bQ67+WEp/
jFzjx1PGj5NrPi5njqwduebvcubIWpPreF3OHG2uLmeOtm+XM0ebq8t5paDN1eW2trtsrr6f
9ff9rL8fn/Plx4/78XV+Xa7z6/pt/lwPLmeOfv6MwbnX8cY598yffXLutT5xzj05c+S1guTM
kXuTfLW9mvXTFjvc+v9SrrmNs9Ot/121W8RjOXaFa5S7lHW8Uct4hQ92hQfWuS52KLOVGwef
+rq61NfY9RnXIl532rsxelJfdVdhZTMb5444eerr8FJfk/dG8Ybx+gtquZ7UV+mR8Rnbpr5u
j/EYlzz1lXzsn3mQp762j3PEMZCnvtov9ZV/tm3Yb5v6WkDbV+D3lfrqwNRXCto8Az/P1NcO
Whb440p9NaGNF/g1SX19YeprDVNfd5j6GsTU1yOmvjbR5h749R8wv2kQy3FHnPN446DmQceu
78TcOU155WLqqxhtbYLlpy/tZn1SX9eY+hpHje+uh9RXPepYArZNfR1k6msitQ6uJ/VVklo3
l6e+blJr7vLUV1LqHLk89bWVezc3LcsxMIfUV1umvvJS14brSX0tpq4ll6e+OlPXnstTX6/J
eWbe7Cv11aXDi0XjT6yrGbDOpnGrnec8cD7IOQ+cDzzP4YeGtfR52OfWH/h+xvPjoH58nV+3
rc6vu2cZr3HG57sZX/1xzYdxnNf4ztt82K/zPNNse58zT9/P/J3XcTnPeNSMz+cp11vcX2+M
x/OHnv+v11n6V1imvtqSb1/5PjiXwF8lj14t8LkFnu+O+XONwTaA57tiPJpP4PPLowUMegsa
fAb4a+XRQgJ/ncAXFvjrDfqKGH4cvN/HDeb9HPA3qkaLGmQ3GdSAv1keLWbQd4vhx8EXV436
Y8eXUI3yswa9JQ0+A3wpefQ2gS8tj94uyiij7w7Dj4P3++BcMIeyRprhzyO+nGrU/8GXV4Fy
HgDPOQB8BXmUtQb8nfIo6w/4ivKoP0f4SqpRfx7xlVWj/lzjq6hGOZeAryqPcn4Bz7UE+Gry
KOcW8NXlUc4x4GvIo5xvwNeUR7kGAF9LHvXXDL62apTrBfB15FGuBcBzHQC+rjzKdQD4evJo
aYGvL4/66wTfQDXKdQP4dHnUX2/4kGqU6wnwYXmUawzwXM+AD+RRrj/AR+RRng+Aj8qj/hmC
b6ga9c8ZfCPVaGOBbyKP8qtVwDeTR5sLfAt5tKXAt5JHWwt8G3m0rcC3k0fbC3wHebSjwHeS
RzsLfBd59C6Bv1se7Srw98ij3QS+uzzaQ+B7yqO9BP5eebS3wPeRRzMEvq882k/g75NH+wv8
AHl0oMAPkkcHC/wQeXSowA+TR4cL/Ah5dKTAj5JHRwv8GHl0rMCPk0fHC/wEeXSiwKfJo5ME
frI8OkXgM+XRqQa9eN9HNk3gp8ujMwT+fnl0pjw6S+Bny6NzBP4BeXSuwM+TR+cL/AJ5dKHA
L5JHF8ujSwR+qTy6TOCXy6Mr5NGVAr9KHl0t8Gvk0bUCv04eXS82KKMPv1E1uklsVkYPfotq
9EGB3yqP9hL4HgbbbTPoA/x2eXSHwO+UR3fJo7sFfo88ulfg98mj++XRhwT+YXn0EYE/II8e
FPhH5dFDAn9YHj0i8Efl0cfk0WMCf1wePSHwj8ujTwj8SXn0SYHPkkfLGrmMq+Wp8fSnGROM
cgI/Th4tL/Dc59RoBYHnuUCN3inwI+TRigI/TB6tJPA8p6jRygI/SB6tIvAD5NGqAn+fPFpN
4HnOUqPVBb6PPFpD4O+VR2sKfE95tJbAd5dHawv8PfJoHYG/Wx6tK/Bd5NF6At9JHq0v8B3k
0QYC304eTRf4NvJoSOBbyaNhgW8hjwYC30wejQh8E3k0KvCN5NGGBtdgzPDXLT6uGvXXOT5b
NervC3xCNervI/wp1egRgX9KHj0k8Kfl0YMC/7Q8+ojAn5FHHxL4Z+RR//zBP6sa3S3wz8mj
OwR+qzzKc3G1sdZ4XuAflEd7C3wvY6XBNi8IPNtSoxkCz7bLDLZ5UeDppUb7CXyGscRgm5cE
nl5qtL/As+1Cg21eFnh6qdGBAs+28w22eUXg6aVGBws828412OaswNNLjQ4VeLadY7DNOYGn
lxodLvBsO8tgm/MCTy81OlLg2XaGwTavCjy91OhogWfbaQbbXBB4eqnRsQLPtlMMtnlN4Oml
RscLPNvGjKuNxqKpMnI89xjaXJ4any1tKU+N5x5DW8tT409J28pT45+StpenxnOPoR3lqfFP
SzvLU+PPSO+Sp8Zzj6Fd5anxzxo9jK0G9xVZN4Mc8OQoffiJxiTDry2e9SYnY22zjONGWYF/
XR5NE/hMgX9DHp0q8NMF/n6BnyePPmCw35PGcYF/XP4xU/YB+KPy6JsCf1gefdQ4YDwsT43f
rxrdJ4/6cfB7VKO7xE5l9OHfUo36ueE5Nj7fblADfps8ulTgN8ujm+TR5QK/UR7dINYrow+/
TjW6QuBXCfwag30vNvzc8ItUo8wf8AvkUX+eZpv35xE/0+AZ9v/8Z2b0v71uMvlaSfe6xi9T
Xj05YX9mYnD37u71jj9+OzURGTYrxqv3omUyE71+zhnntW5fpryS8ts7Rye++WF2druCoyLb
M0YmNubcmz3imYqRypObJfKUK5xo+/r6yPzcNRODfq2R4FWA9z9SODHppmYuX7FgX3adW0cm
6H+48tzsK++OSjBO6iss9/TJHR9TOtO9TnHUpO2xyV8mX4+o10S6V1t26T4i3GVf8jWIj51Z
HF76TbLn049/D7dJS26b+srL6KNzIk9fN9rt62J0T6Tp7OQc7i1bONp3SnJuJf+sEb1wJTnn
hkWbRcsfTB5L0Vojo63z7HPHOP7SqOj9Ix5wx576isxKJTOj/7HX2LFWhb+eGr3FXnvHGup1
mW5tH9yfGT1or03kVXfXfDc1ut5en0fP12Uyo53sFXtsm/pKzQ/LjI6uLzMnwvrsHDYy2vn0
ngjrtj6zWfR4mcJR1rnFuJrR7vNqRFnnc48Wjua7sZnLL8/ZG/ms1cgo/QX/eCBS4ZNRUcZJ
fQXnwf15glO3JV8vWKTujnD3L5OvUNRrQ92rOTdPGBqbsS/5qsRr8yyO7fsm2fNMh0ux79OS
26a+svOLj+dkH8g72u3r8aZ7s3+4S3O4vXDilanJuRVZUiOxbkRNN+cLRZolJh5OHsvVubsm
0m/+I7Liu1mR1Nd9pr4GNPVVoamvEE19zWjq60dTX0ua+urS1Feapr72NPV1qKmvSU19lWrq
K1ZTX8Oa+nrW1Ne26l5z10CjVZmJg52/d9dA99jkRKtLs8O8tq/O9mmJ7YPz239DTIu8sWhq
4vsqD4bXRYJIvZ4TE60K3B+L/Lko0iMrM7Hs6vMxXlOY+lrAzff2Tnzw06bsIRefj7z7Q4fE
PV8USlwaUiVS4/e0xE0V0hKl85yLvPF28USfP5rZK0sbR27ftzX7yXH9Erza8lL1ZdlvLxvp
7ovmfQrHTz+QvKd2P3dt/I9rpyYyyzaLFL1qe2xrkeSrSMOXVsV21rDXCr4+JHJNdp3woleT
r0G87ddp4RP2ylVet/rlw1+FfzyefJ1i6msWB5zbGHltee8E81w/sFD0x387uNc+l9ySFq39
eVrilpdfiRy+vmm0/tBb3asY+756X3RB+W3Zsa8e/m+vfUx9HaQ9AaP+2adXVbrXSn5mrwbN
Zfcgr6B9IpQZXWWvpOT+6lpzavRVe1Ulx9Xz8YnR+XYP8qrTasft/rVXW7K2F5pnRrvY/chr
ZFNfhVngr3ujF37YGLnc9aXIx0c6Ruv8fa27v3oXLRc9PywtyvzHnSsRPXRtsyjjb7x6W2TG
zn7RRnWPRPo1Xx7pOmCkuy+KF7s+6PZA8p6aUb1g8Fi1qVHOy2s99obrxyZFF26fGXng0SXh
EunJ+2tB0YzYKethzIdrL4o1DiZFf5jzQKTp9b/E7L2uUa6T1NeJZvTZlD3zy3ujzPPzF69N
LDzcMcr18PextESvl5PzXJbWLBE5UsKNmX9b/0TdPQsjNWNPRFb9PSrxfoMH3DOnbfqwRNUp
+yK8ltSvsa13IqcV/zuSy+Z1lYFeLXKb5jGuMfIa+Yz8RgGjoHGtUci4zihsXG8UMW4wbjSK
GjcZNxvFjFuM4kYJ41ajpFHKuM0obdxulDHuMPgeLs0oZ5Q3Khh3GhWNSkZlo4pR1ahmVDdq
GDWNWkZto45R16hn1DcaGOlGSIRNIRD0AycMuDmAfUBD0cgUGgvmCE1EU1PguKCZaG4KLQTr
Ai1FK1NgLaG1aGMKfM8OnAtoJ/z5am+1h6yD0dHoZHQ2uhh+27vM3210Ne4x+F67u9HD6Gn0
Mu41eht9jAyjr+Hn3M/8fUZ/Y4Ax0BhkDDaGGEMFnjUoLfVr4nWY5cONEcZIY5Qx2hhjsKZj
jXHGeGOCMdGYZEw2phiZxlRjmsH36zOM+w3O40xjljHbmGM8YMw15hnzDdaKdQK/ln59/Fr7
tffnwp8bf65a2rbg18WfW84z+HPvj7epZeCvFY4R/LXEdQUNRVVTiAp/bXJ84K9dfy1zbXvv
P/O9fls/lh+7oW0Dft9+Ln5ufq5+7v6YvHKcqfg18OrXxqtfM69+Lb36Nfbq196rPyde/bny
mtfmk4o/t17/J9Yo9Zzir05hgfn/U+H/lWN2LvsZ/8QzweuPLwmWbJlrr7OaG0wcfiZ4v+ox
R/1BZ4Kn3z4dbPv8ZPB6oYQD/8Brp4Nz7Z8NNs5q7bbjdVbrDLToktbB9TmvCRUM/x6ekKt4
iPHxjPteomaYsUu0bRJinOWnJ4QYt/bMx0Ps5+xHV4eZC9u9bb30XfylSYjtZlrGOKfy5Q6z
XXXbhu0yhk4Msd3F/deEmA/z4DiYx4pWz7pje9rmwPaMzXjMgfE5PrZnLozHXBif42NfbLej
cCNurxyD+lZzmt4tGllXLi185rVKkYsnfw+d2FLJ1bU+vtnVKJ+3r3C1012r/gzoW/POxYC8
7z8fuXp1yfdc/UL3t1295Y83XD04esHVzIX+fY/GXM0cqa8rcNzVHAP1KxM2Jfvt2Kg5bvaH
UnMcaOnup8LkHDd1ww8ruZrjpb745gchPmcdXH1ykqvX5UvOY8hDyXm8mju5/613Jve/fHRy
/+uOJvfPOWAcdy5s3BvLJ/dfoWly/1+tTe6/47Hk/s/buWN/OeYk99+xcnL/pYsk97/hmaZu
HT9Z1cSt7z/VG7v6+NNRV2+5O3k+Jkys6epim5LnY82HyfOBMv6htOT5GLA0eT66vp48H3dc
Tp6PxXclz0PvX5PnoWJ68jzUfT65/1lrk/vfUiu5/5sLke8J9Wvd1PY7KVTjxHk77kmh3LVf
tXXfE+p931tOn//mTZf/WOIjV7958ENXb/jzD1fXPPKHq5Pz3BNKzntS6P1ETTf+ss84rkmh
szUauvr9wQ1dPblAcv9Pt0juP8fq5na+JoUaXupq529PqOHos04vfvGsyw9fKGvrvCf0Vd/b
7bxPCv16Oe7qXq/FXJ08X3vceePzXldtdvM73Xazm9/Vnxx3damOJ1y9dlPc1ZVuyHb1qfQW
bj+lzyT3eyr9OVfzOlD2+/bi5H6/uzbb1Xd9ldxv8jrd465X9rspb3K/9ipEN26TL5P77XV3
cr+vb0vud2ix5H5HZSXXvUmD5Lo/ODi57tf8lFz3qrcn1/3Gx5Lr/uaV5LqPPpFc9+T9uieU
vH8nhc7nr+zWeW/5ym6dP2hEnRZ6rLfL09Wf/uwfJdzzYPjRPE533eHGTX9662/89ZzD7ifW
J/25wR+4+sSbbzl991+urz3p1y674OrWx8+5Onmf7UlvPfVpl39RJtvpihqPu88f3va4q89+
5tYnPbPLSldr/dJHb+zi6oxXcjot/eCTrHN6/V8e4duGHPUfLu7q0Q1udvVP/7zOX5c5Sr/O
/bYn/dRNs119sWR5V3e7mvt+Tzqv5aRvVa/kfDpXTs5n2KbkfHgO8XmRd486bbTpiNPtxQ85
vbnSw06Xf5Scd/3sEzZuWujOddRpoX8ztrvPx/IqQfuj6zB90H/aufqMvdqQvMKC5PFUiD7k
6pYzk8cz87rk8WTseDM5/9Ozksc1sZw7jsun3X2SfviqFu48zbinqdPf3nT3U3quQsnn+6Uq
tTjv6flrVXGf635Mb3O4mKt3/nCV0/6lkud5wX3J87rz1eR5PvRt8vwmn+O2bruS57fg4eT5
/SFvcv+39kju/+A891wJlap13q1DzbFvOo1FP3T60iD2k+aeB2jjfMwvLfTVNuadFir0QHL7
7dXr2nGmhWbem3Ba7OeSdp7TQqcOZjnVczj01OJsN17GkWTfzLeT2+UtUcr1PXE62a+/N0KD
NifPz8Snk+crx8rk9mMmJefZq35y3n82Tc4334jkfPX3X6jOhmeD7TWzA67becufdzxkvnDO
+UGHPPODLYkXgjqN1tj3EC8GX37aw+U9quUJ4sVeDHiF9eXRLwT7xh8Os+0Iu2YZZ/b+qenc
F8PtFZdVMk4HTVY8Hcy5OR7kqvRc8EPa0iD/ry8EDZq1cK+TLvZdHrefaeO/CfO6aK57xhrd
5Bk3t4zMPqFhA04HDS+9mc4YM21s5pfjlSLp52rYNdlpQYMK1y121+BLhVsEjFdnQx77fFWD
rRsuhekbNnt/mPvrYpXC6TPvjabn7TErnKPrXekv1usZZn/Md+aF3unx9BbhHIcHptcNB+Ec
PwxL/8b+DmR/HBf34Zefvuvuv4UXeocy7LWcYzueDnEf2/YNuM/fvepgA54LoedmhuaVfi6w
Vwi7a9y+hXM/19u3ce53D1epRv33qfjcAp/H4M81BtsDnu+r8Wg+gc8vjxYw6C1o8Bngr5VH
Cwk8vz8AvP+eH8/vE+jjdwp+HLzfB79n8HPA8zsHarSoQcbvH6gBz88geJTfSdDH7yX8OHh+
R0GN+mPHl1CN3mrQW9LgM8CXkkf9z3z40qrR20UZZfTdYfhx8H4fnAvmUNZIM/zPZPjyqtEK
An+nPFpR4CsJfGV5tIrA8zMhNVpN4KvLo/yeBfA1jVpGbcP/nImvqxqtJ/D8HoYabSDw6fIo
Fy3geYgDnpsMj/KQBTw/z+LRhgLfSB5tLPBNDH5G4+dXP2c8P8NSoy0EvqU82krgW8uj/mdR
fFuBbyePthf4DvJoR4HvJI92Fvguxl3G3UZXgb9HHu0m8N3l0R4C31Me7SXw9wp8b3m0j8Bn
yKP+2sD3VY32E/j7jP7GAGOgwA+SRwcbQ4yhxjB5dLjAj5BHRwr8KHl0tMCPkUfHCvw4eXS8
wE+QRycK/CR5dLIxxcg0psqj0wR+ujw6Q+Dvl0dnCvwseXS2wM+RRx8Q+Lny6DyBny+PLjAW
GsxzkTy6WOCXyKNLBX6ZPLpc4FfIoysFfpU8ulrg18ijawV+nTy63thgbDQ2yaObBX6LPPqg
wG+VR7cJ/HZ5dIfA75RHdwl8mjy6W+D3yKN7BX6fPLrfoBfv+8geEviH5dFHBP6APHpQHn1U
4A/Jo4eNI8ZR4zF59JjAH5dHTwj84/LoEwJ/Uh59Uh7NEviYPBoX+Gx5NCGPnhL4p+TR08bT
xhnjGXn0WYF/Th59XrygjD78i6rRl8TLyujBv6IaPSvw5+TReQLP/cV25w36AP+qPHpB4F+T
R1+XR98Q+Dfl0bcE/m159B159JTAvyuPvme8b3xgfCiPfiTwF+XRjwX+E3n0U4H/TB79XB79
QuC/lEe/Eviv5dFvBP5befQ7gzl/b/wgj5Y1yhkD5anx9KYZO43yAr9dHr1T4LfKo5UFfos8
WlXgN8mj1QV+ozxa06htrDPWyKN1BZ7nGjVaX+BXyKPpAr9MHg0Efok8GhX4RfJoI4HPlEeb
GM2M+cZcebS5wM+RR1sK/Cx5tLXA3y+PthP46fJoB4Hn7zlqtJPAMz9qtItxtzHJmCCP3iPw
4+TR7gI/Rh7tKfCj5NHeAj9CHs0Q+GHyaF+BHyqP3mdwDf5ocB1+Z/xk/CyPfiPw/5FH/X2B
/0U1+oXA/yqPfirwl+TRjwX+N3n0I4H/XR5lnu8Zl40/5NFTAv+nPPqWwP8lj74h8H/LoxcE
/pw8+orxtPGs8Y/An5VHFwj8POOUcdr4V+CvyKOLBX6hETdOGf6HLjzbUqNLBZ5tswy2yWmf
A55ePLrcBPBs+4TBNrmsBjy9eHSl1YBnuxMG21xlNeDpxaOrrQY82x0z2OZqqwFPLx5dazXg
2e6IwTa5rQY8vXh0vdWAZ7tHjcNGHqsBf408utlqwG8wfcRgm7xWA57t8OiDVgOe7R4y2Caf
1YCnF49usxrwbLfXYJv8VgOeXjy6w2rAs92PxkBjsDHEGG5wvwH+Z+lIeWo89xg6Wp4azz2G
jpWnxnOPoePlqfGXpBPlqfG/SSfLU+O536YY04zLAs89hs6Qp8Zzj6Ez5anxfxkPGOcM7quZ
xmyDHPDkKH34XcZuw68tnvUmJ2NdC5gWNK4V+ELy6HUCX1jgr5dHiwj8DQJ/o8DzPzFIjfI/
I8h+bzbYH+D5nwjE32KwD8AXl0f5n/gDPP/Tfni0pFHKuE2eGl9aNXq7POrHwZdRjd4hyiqj
D5+mGvVzw3NsfF7OoAZ8eXm0gsDfKY9WlEcrCXxlebSKqKqMPnw11Sj/c3yAryHw/O8wse9a
hp8b/qSdd2qU+QO+tjzqz1Md8/484usa/JG43/fZ1RilzuU+8Z/NjFL6rIL7LNl3lXn605TR
47Nkf/JVr1db7j9jH3iffaxt2S63gfIZfajPMogs4/M8Bp/1Msjo8VlvZcg1Bp9VpLA+5uoz
+smo8xrU+Q3f5zM+J6POZ/h+3+ez4rSpj3Hov57IMnp8hiejLmBQpxu+z2dFlLG/ggb9lZQx
ts/oZ1vqaw3qKgYZfT7jczLqQobv930+K0yb+q4z5/vJ6PFZHdrUxzb+MzJ6fFaLNvWxHnxW
jcgyenxWQxnjcOx8Vk8Zx+Ezv6asBxl1A4PxOPYbDPKwQcb6+gwlQ2800KKG7/MZSobyOdrc
8H0+K6aMcW4yyCPK2MZnKNuiNxtoQ8Pvw2coGcrYaGPD9/msqTL2d4tB3lIZx+szlG1Rrk+0
pEFGn8/8tcv9gYcSBn3eU5dVRh813KrMe+puyuijhjRlfg7Mo5Uy9kENpZR5T91GGX3UcJsy
76lLK6OPGu5QRl9p0e7/Yu9NAKU76jLvDkkgBJAE4g4alCUIHGs551QVsuRCWGVJ2ERASYCY
AAFCFgjIEtmJbCIiOyEssigiLuMO7o6i467fjN98zOg46LjgiDuS73nq1CHNm/dNbl363re6
+3mT/+2u//3X6eru555f/etUnSq+uQ79tym++TnLDy0+xrFM+7rim5+zfFbxMY5l2sOXfGwD
7ZHFx/bNvvkz5edHH8vfAuNnfyx+zp/dY4qPv+dneXvYC4+hczqfzr470FV8jGXc/6ALvuWY
Pyu+G+CRMax3WvHxgT6W78gC6s4xLP+v4uMD69H3DSwgjucr+li+E4w+nmvoY/nOMPpY5vFZ
/t+wOW723aX4eP6hj+Wu+OZ2sfyXxcc4toO++fzCcwN9LBsYX2NuK8v/p/gYx/bSZ4uP5x/6
WHbFN78nlv+m+BjH90WfL76bFx/LffHN753lvys+xvH90zcUH89/9LE8Fh/LfP8s/33xMW72
heLjeY8+lmPxsczPhOV/KD7Gzb5UfCcWH8t3Lb6bFB/L31R8rMfPk+V/LD7Gzb67Fd8ti4/l
uxcfY/gZs/zPxce42XeP4uP5kT6W71l8LPO7YPlfi49xs+/04vvy4mN5p/jm75Dlfy8+xvE7
o+9excfzKH0s37v4WOb3yPJ/FB/jZt8ZxcfzPX0s36f4WOZ3y/LVxce42Xff4vvS4mP5fsXH
GGqA5WOOoXPaFnz23Z8u+Hg+pY/lB8Do47mTPpYfCKOPZeqHZeacc9zs+2a6EMfzJH0sPwhG
H8vUFMvHl7qMm30PxnPGnYqf9LH8EBh9LFN7LN+o1D11yfdQPGfcbYqP5TPpgo/1qEeWmTfO
cbPvLLoQx/MtfSw/DEYfy9Qty8xR5rjZ93C6EMdzNn0sPwJG36x3lplPzXHUPH2PpAtxX4+f
9LH8KBh9LFPzLN+81GXc7PsWPGfcVxcfy4+mC75b4SfjWP5WGH0s8++FZfbv57jZ9xi6EHcs
ftLH8mNh9LHMvyGWmc/NcbPvcXQh7ob4SR/L3wajj2X+rbHMHGKOm33fThfijsdP+lh+PIw+
lk+Hscx8cI47Hc/oOxtG33H4eTrsbNg5MPpOx88dGMtzXcbNvifgOeNYvheM5SfC5uPNvnOO
mXyMuzeMMcxXGceY2fckuuBjmX+7LJ8Lm+Nm3xNKXcbx75kxzKcYx5jZ9x10wccy/55ZPg82
x82+J5W6jOPfOGOYfzOOMbPvfLrgY5l/4yw/GTbHzb7vKHUZx797xjDPZxxjZt9T6IKPZZ4L
WH4qbI6bfeeXuozjuYAxzJcZx5jZdwFd8LHM8wPLT4PNcbPvKaUu43h+YAzHCBjHmNn3dLrg
Y5nnDJafAZvjZt8FpS7jeM5gzInFx5jZdyGesy7LPI+w/EwYfYybfU8vdRnH8whjOLbFOMbM
vovogo9lnltYvhg2x82+C0tdxvHcwhiOrTGOMbPvErrgY5nnFpYvhc1xs++iUpdxPN8w5rji
Y8zsexaesy7LPAex/GwYfYybfZeUuozjOYgxNyg+xsy+y/CcdVnmeYnl58DoY9zse3apyzie
q3JM8TFm9j0Xz1mXZZ6rWP5OGH2Mm33PKXUZx/MXYz4HYxxjZt/zio9lnr9Yfn7xMW72/WLx
MY7nNMZ8tvgYM/teUHws85zG8guLj3Gzj2MrbAvjeE5jzL/B6GPM7LucLvhYPpvPYN8Fm+PO
5jMYt0SY487BM8b8C12oezZ+zr4X0QUfy0+Asfxi2Bw3++52zORj3BNhjPknulCXMbPvJcXH
8pNgLL+0+Bg3+04vx2PcuSXmMyWOMbPvZcXHMs99LL+8+Bg3+84ox2PceSXm/5Y4xsy+VxQf
yzz3sfzK4mPc7Lt/OR7jnlxiPl3iGDP7rig+lnnuY/m7i49xs+9B5XiMe2qJ+dsSx5jZ96ri
Y5nnPpZfXXyMm31nluMx7mkl5q9LHGNm32uKj+Wnw1h+bfExbvY9ohyPcc8oMX9V4hgz+15X
fCxfCGP5e4qPcbOP2xpQG4x7Jowxn4LRx5jZ9/riY/kiGMvfW3yMm32PK8dj3MUl5i9KHGNm
3xuKj+VLYCx/X/ExbvadXY7HuEtLzJ+XOMbMvjcWH8vPgrH8/cXHuNn3vHK828HHWMb8GYzv
lz7G0fcm2Ox7dim/ufgYM/ueu3S8y+BnzNtLHGNm31uKj+XnwFh+a/ExbvZ9Zzke455bYubj
MWb2vQ3P2T6WvxPG8otKXcbNvnfg+fw+GMtjXV7iGPM8GGPeCWMc684+blFBH+OeD2PMi4uP
MbPvSjxnHMsvgF0JexeMPsbNvm8tdRn3QhhjXlJ8jJl9V+E567J8OYzlDy3Fzb53w884lr8L
xvJ7YPTxeLPvkaXu5fC9CMaY+XiMmX3vxXPWZfnFMJbfB6OPcbPvrHI8xr0ExpgPFh9jZt8P
4DnrsvxSGMvvh9HHuNn34FKXcS+DMeZlxceY2fcBPGddll8OY/mDMPoYN/seUOoy7hUwxnyg
+Bgz+z6E56zL8ithLP8gjD7Gzb77lLqMuwLGmPcXH2Nm3w/hOeuy/N0wlt+3FDf7Pgw/41h+
FYzlH4bRx+PNvp1Sl3GvhjHmvcXHmNn3ETxnXZZfA2P5R2D0MW723b3UZdxrYYx5e/ExZvZ9
FM9Zl+XXwVi+ailu9v0o/Ixj+XtgLP8YjD4eb/alUpdxr4cx5t3Fx5jZ9+N4zrosfy+M5Z+A
0ce42cfrOHPcG/CMMe8pPsbMvv+E54xj+ftgLP8kjD7GzT5b6jLujTDGzMdjzOz7KTxnXZa/
H8byu0pdxs2+n8ZzxrH8JhjLVy7Fzb6fgZ9xLL8ZxvI7l+Jm38/CzziW3wJj+R1LcbPv5+Bn
HMtvhbH8tqW42ffz8DOO5bfBWP4lGH18H7PvY8XH8tthLH8cNsfNPl6no49x74B9HMbrefQx
Zvb9Al3wPa74WP5FuoqPsfTNfczH4DnrMuZZ5Xhs8zthbO9bi4+vO/t+Gc95PJavhLH85qW4
2fcr8DOO5XfBWP5VGH083uyb38eV8F0FY8ybyvEYM/t+Dc9Zl+V3w1h+w1Lc7Pt1+BnH8ntg
LP9nGH083uzjNdI57r14xpjvLT7GzL7fwHPGsfw+GMu/CaOPcbOP12LnuB/AM8a8vvgYM/s+
geeMY/n9MJZftxQ3+34Lfsax/AEYy78No4/Hm328HjzHfRDPGPPa4mPM7PsveM44lj8EY/l3
YPQxbvadVuoy7gdhjHlN8TFm9v0unrMuyz8EY/n3YPQxbvbdvtRl3IdhjJmPx5jZ9/t4zros
/zCM5T+A0ce42XfbcjzGfQTGmFcXH2Nm3x/iOeuy/CMwlv8IRh/jZt/XlbqM+yiMMa8qPsbM
vj/Gc9Zl+UdhLF+xFDf7/gR+xrH8YzCW/x8YfTze7Du11GXcj8MY88riY8zs+694zros/wSM
5f8Go49xs49zG+a4/4RnjHlF8TFm9v0pnjOO5Z+Esfz/wuhj3Oy7VanLuJ+CMWY+HmNm33/H
c9Zl+adhLP9/MPoYN/s4H2OO+xk8Y8zLi48xs++TeM642+InfZ+EPb/E0cdY+v4njHHH4Sf9
/wO27GMcy5wzwrjb4+elsD+D/Tls9l1cyv+r+O6AR/pY/osl3zNL+X8X32l4pI/lTy35nlHK
f1l8d8QjfSz/1ZLvaaX8f4rvG/BIH8t/veR7ain/TfHdCY/0sfy3S74nl/LfFd+d8Ugfy59e
8p1Xyn9ffHfBI30s/98l37ml/A/F1+GRPpY/s+R7Yin/Y/F9Ix7pY/mflnznlPI/F5/BI30s
/8uS7/Gl/K/FZ/FIH8v/tuT7tlL+9+JzeKSP5c8u+R5byv9RfB6P9LH8uSXft5by1cXX45G+
XC4aou9b+HuU52snQ/GxPI9z0fdIGMvHlrpj8bF83JLv4fCzfHzxBZTpY/mGS76z4GN5vtYR
UaaP5RNKHH0PhbE8X9dIxcfyPI5J34NhLM/XMO5afCzfFMa/D/q+GcbyfL3im4qP5S8pcfQ9
AMbyfG3ibsXH8kkljr77wVierzncvfhYnsep6bsPjOX5+sI9io/lU2BsH333hrE8X0u4Z/Gx
PI/L07cDY3l57P9n4eP54RwYj8dzxuz7yuJj+edgLD9xKW72zec1nuvoY5lzwng8ln8exvK5
xce42TefY3nepY/lW5c4lj8GY/m84mPc7JvP92QAfSx/bYlj+eMwlp9cfIybfTN7fqT4WL5N
iWPML8BYfmrxMW72zbz84eJj+etLHGN+Ecby04qPcbNvZvcPFR/LtytxjPklGMvPKD7Gzb7b
F9+Hio/lOxQfY34ZxvIzl+Jm32nF94ESx/Idi48xvwJj+eKluNk396/eV+JYvlOJY8yvwli+
tPgYN/vmPuF7io/lu5Q4xvwajOXLio9xs68rvncVH8vfWHzvKD6W5347fYylb+5Tfx/Kvw5j
/jXnEN+75Bvhp07fXnyM8cX37fDRz/KcL9DH49EXSxyP959hzBnn433Pku+uJY71GMeYUHxn
o0w/y/Px6GMcfXcrcTzeb8CY587He82S7x4ljvUYx5hvKr4noEw/y/Px6GMcfaeXOB7vN2F3
R3k+3quWfPcqcazHOMbcs/iehDL9LM/Ho49x9J1R4ni8T8B2UJ6P98ol331LHOsxjjH3Lr7v
QJl+lufj0cc4+u5f4ni834LdB+X5eC9f8j2wxLEe4xhzv+I7H2X6WZ6PRx/j6HtQiePxfhv2
AJTn4710yfeQEsd6jGPMNxffU1Cmn+X5ePQxjr4zSxyP919gD0Z5Pt6Ll3wPK3GsxzjGPLT4
LkCZfpbn49HHOPoeUeJ4vN+BnYXyfLzvWvI9qsSxHuMY8/DiezrK9LM8H48+xtH36BL3XSj/
LuyRKM/He8GS7zEljvUYx5hvKb4LUaaf5fl49DGOvseVOB7v92DfivJ8vOct+b69xLEe4xjz
2OK7CGX6WZ6PRx/j6Du7xPF4vw/7NpTn4z1nyfedJY71GMeYxxffJSjTz/J8PPoYR9/zSty9
UCZvyeMnFN8ZxcfyE5d8ZCvLTyq++6JMH8vnLvl+Hj6Wv6P47o8yfSyft+QjM1k+v/geiDJ9
LM8Mpe/jMJafUuIeVHwsP3XJ9wvws3xB8T0EZfpYntlIH7nH8tNL3JnFx/IzlnxkHMsXFt/D
UKaP5Zl59P0yjOWLStwjio/li5d8ZBfLlxTfo1Cmj+WZZfT9KozlZ5e4x6BMRj0L5ecU36NL
HGMuW/IxjuU57tko8zt/LnyzXp615Jt18OPw/Qzs+Yh7eTnebVGmn74XFB/LfwBj+ZVLcbPv
hcV3uxLH8uXF99ziY/m7io/1/hDG8vcvxc2+FxXfd5Y4ll9cfM8vPpZfUnwvLD6WX1p8Lys+
lj+wFEc/fS9b8r0EPpY/WHx8vz8F42fyiuL7UZTZbr7/K4rvo8XH8ncv+f4IfpZfVXysN/ve
WHwfKT7GvLr4Plx8LH9P8X0QPvpfg/Jri+/9xcfy64rvB4qP5bkufXxdll9f4t5bfCx/b/G9
u/hYfkPxXVV8LH/fku+P4Wf5TcXH48+++b3x/dLH8vz98rulj+UfKHWvLD4e683F987iY/kt
xfdq+Ohn+a1LPh6Pvvcu+d4KH2PetuR7C3wsv734Xst6MJbfseR7M3wsv3PJ9yb4WL5yyff9
8LH8riXfG+Fj+ariex3K9LH87uJ7ffGx/J7i+274+D74Ht5XfFcUH8vzZ0UfP0OW31/iXlF8
LC9r/EXwU8sfKnHHHPeXizOP+72zrvz1Y6484feu+uxrr/7nq/k/dlD/HLdMx///fvU7rzrt
imv9/5nPXf33eQd1/Hzhf3zsKtSY/uHJrX/lrFv92lm3ut8z+f+v8P9Tfu01f3batFn7h99/
xQdPu+KD+Jn/v+r9V3zdfc46hf+/9Amnvei4B5z2mlMf+aJTFiff9oEn/+UJD7vpKWjx/O+C
q95z+i/+5m12WOY7nP5dsxP67Dn84/7F3frwL3gE7w3hn3ZgnwL2r11HaEBxT697EkonXP6s
37BZEcxF/vEPbnmPD7z99vfg8+MXJ15+LOOv5vqYT//TQ37uKW/7aXYQFn/38gvutvz8ynv+
4V0P9SP+7nMMnz/hLQ+5O2N4nPk5y9Nr4CWwtmb5NdCSn/vBf/hadioW/3Duj/zs+ffdyc//
7uV//TMffctD5uffND9HzN3mGNS9+1x3uR081jXv6fh83E+94/V3m1/jM3/9d/n5d6e7/+zy
8/fd7y657WzH/PwLj3UDFhfzsfj88HE3WuDYd5vj+Hx+Hbb/SP7lmPm4rDs/5+vN/06cn+TH
kzJw8ff8Bd4Tlkov/ce3nE5bcuHLt+z4LX7rEw+6+wf/frp72aHl848hDy+/52Rn57/LIiOG
7uLftHLrmkAea3E6/oddDrsS9nHYJ2ELHP8k2KkwAzsddiaMr3sh7HLYK2Cvg70JdiXs/bCP
wH4S9nHYr8N+B/YnsE/CPgX7NOxfYJx0ehzsBNhNYSfBToF9BexWsFNht4WdBrszzMB6WITd
DXY67AzY/WEPgp0JewTs0bDHwc6GPQl2PuwC2IWwS2CXwZ4Huxz2IthLYC+DvQJ2BexVsNfA
Xgd7PewNsDfC3gR7C+xtsHfAroRdBXsP7H2w98M+CPtB2IdhH4F9FPZjsJ+A/STsp2E/C/t5
2Mdhvwj7Zdivwn4d9huwT8B+G/Y7sN+D/QHsj2B/AvuvsD+F/XfYJ2H/E/bnsL+AfQr2V7C/
hv0t7NOw/wv7DOyfYP8C+zfYZ2Gfg3Eg8RjYDWDHwo6DHQ+7IexGsBNgN4adCLsJ7Kawm8G+
BHZz2Emwk2G3gN0SdgrsS2FfBvty2FfAvhL2VbCvht0KdmvY18C+FnYq7Dawr4N9Pey2sNvB
bg+7A+w02B1h3wC7E+zOsLvAOtg3wgzMwhzMw3rYABthARZhCXZX2DfB7ga7O+weME5SPh22
A7sX7N6wM2D3gd0Xdj/Y/WEPgD0Q9s2wB8EeDHsI7KGwM2FnwR4GezjsEbBHwh4F+xbYo2Hf
CnsM7LGwx8G+DfbtsMfDzoadA3sC7ImwJ8HOhX0H7DzY+bAnw54CeyrsAtjTYE+HPQN2IeyZ
sItgF8MugV0Kexbs2bDLYM+BPRf2nbDnwZ4PewHshbDL7724HLb4LjzCFi/CI2zxYjzCFi/B
I2zxUjzCFi/DI2zxcjzCFq/AI2zxSjzCFlfgEbb4bjzCFq/CI2zxajzCFq/BI2zxWjzCFq/D
I2zxPXiELV6PR9jie/EIW7wBj7DF9+ERtngjHmGL78cjbPEmPMIWb8YjbPEWPMIWb8UjbPE2
PMIWb8cjbPEOPMIW78QjbHElHmGLd+ERtrgKj7DFu/EIW7wHj7DFe/EIW7wPj7DFD+ARtng/
HmGLD+ARtvggHmGLD+ERtvhBPMIWP4RH2OLDeIQtfhiPsMVH8Ahb/AgeYYuP4hG2+FE8wvI/
nZ91fr4BtHAs7DjY8bAbwm4EOwF2Y9iJsJvAbgq7GexLYDeHnQQ7GXYL2C1hp8C+FPZlsC+H
fQXsK2FfBftq2K1gt4Z9DexrYafCbgP7OtjXw24Lux3s9rA7wE6D3RH2DbA7we4Muwusg30j
zMAszME8rIedsfPeG52x88avOWPnT884Y+dlzz1j54MfO2PnCafcZ+d3LrvPzq3+5j47Fz/z
vjs3veH9dm7zofvt/NPZ99/5ozs8YOcWiwfuHP9XD9w5+S++eeddn3nQzp2+7CE7d/nmh+58
4xvO3PmVvz9r57VPevhO/JtH7Fz2qkftfPm9H73zVyc/ZueP//WxO3/079+GfsbZX2B3fcTj
dtKbHrXzpvGsnb+4w4N2Lj/3fjuX/eW9dp734Xvs/NIP33Xns58ad05/lN854TPfuHPrj915
5w0/dsedX/7d2+/c45Tb7vz6c26z8+jF1+7c/H232umf/FU79v5fsfPanS/b+aeHn7Jz+xfc
Yudffv6kncd+6c13zrr8Zjuf/txNdh73uhN3PuFvvPPiT91o5/d/6IY7X/Hi43d+5rzjduxj
j935zONusPPqC47ZueKVi51jz7v69Nv9wX+c/ivf+tnT7/bP/3b6337oX09/8LP/5fTpHKCf
bX8C0rQ03bZC61snTUvT9appu4Y0LU23rdD61knT0nS9atquIU1L020rtL510rQ0Xa+atmtI
09J02wqtb500LU3Xq6btGtK0NN22QutbJ01L0/WqabuGNC1Nt63Q+tZJ09J0vWrariFNS9Nt
K7S+ddK0NF2vmrZrSNPSdNsKrW+dNC1N16um7RrStDTdtkLrWydNS9P1qmm7hjQtTbet0PrW
SdPSdL1q2q4hTUvTbSu0vnXStDRdr5q2a0jT0nTbCq1vnTQtTderpu0a0rQ03bZC61snTUvT
9appu4Y0LU23rdD61knT0nS9atquIU1L020rtL510rQ0Xa+atmtI09J02wqtb500LU3Xq6bt
GtK0NN22QutbJ01L0/WqabuGNC1Nt63Q+tZJ09J0vWrariFNS9NtK7S+ddK0NF2vmrZrSNPS
dNsKrW+dNC1N16um7RrStDTdtkLrWydNS9P1qmm7hjQtTbet0PrWSdPSdL1q2q4hTUvTbSu0
vnXStDRdr5q2a0jT0nTbCq1vnTQtTderpu0a0rQ03bZC61snTUvT9appu4Y0LU23rdD61knT
0nS9atquIU1L020rtL510rQ0Xa+atmtI09J02wqtb500LU3Xq6btGtK0NN22QutbJ01L0/Wq
abuGNC1Nt63Q+tZJ09J0vWrariFNS9NtK7S+ddK0NF2vmrZrSNPSdNsKrW+dNC1N16um7RrS
tDTdtkLrWydNS9P1qmm7hjQtTbet0PrWSdPSdL1q2q4hTUvTbSu0vnXStDRdr5q2a0jT0nTb
Cq1vnTQtTderpu0a0rQ03bZC61snTUvT9appu4Y0LU23rdD61knT0nS9atquIU1L020rtL51
0rQ0Xa+atmtI09J02wqtb500LU3Xq6btGtK0NN22QutbJ01L0/WqabuGNC1Nt63Q+tZJ09J0
vWrariFNS9NtK7S+ddK0NF2vmrZrSNPSdNsKrW+dNC1N16um7RrStDTdtkLrWydNS9P1qmm7
hjQtTbet0PrWSdPSdL1q2q4hTUvTbSu0vnXStDRdr5q2a0jT0nTbCq1vnTQtTderpu0a0rQ0
3bZC61snTUvT9appu4Y0LU23rdD61knT0nS9atquIU1L020rtL510rQ0Xa+atmtI09J02wqt
b500LU3Xq6btGtK0NN22QutbJ01L0/WqabuGNC1Nt63Q+tZJ09J0vWrariFNS9NtK7S+ddK0
NF2vmrZrSNPSdNsKrW+dNC1N16um7RrStDTdtkLrWydNS9P1qmm7hjQtTbet0PrWSdPSdL1q
2q4hTUvTbSu0vnXStDRdr5q2a0jT0nTbCq1vnTQtTderpu0a0rQ03bZC61snTUvT9appu4Y0
LU23rdD61knT0nS9atquIU1L020rtL510rQ0Xa+atmtI09J02wqtb500LU3Xq6btGtK0NN22
QutbJ01L0/WqabuGNC1Nt63Q+tZJ09J0vWrariFNS9NtK7S+ddK0NF2vmrZrSNPSdNsKrW+d
NC1N16um7RrStDTdtkLrWydNS9P1qmm7hjQtTbet0PrWSdPSdL1q2q4hTUvTbSu0vnXStDRd
r5q2a0jT0nTbCq1vnTQtTderpu0a0rQ03bZC61snTUvT9appu4Y0LU23rdD61knT0nS9atqu
IU1L020rtL510rQ0Xa+atmtI09J02wqtb500LU3Xq6btGtK0NN22QutbJ01L0/WqabuGNC1N
t63Q+tZJ09J0vWrariFNS9NtK7S+ddK0NF2vmrZrSNPSdNsKrW+dNC1N16um7RrStDTdtkLr
WydNS9P1qmm7hjQtTbet0PrWSdPSdL1q2q4hTUvTbSu0vnXStDRdr5q2a0jT0nTbCq1vnTQt
Tderpu0a0rQ03bZC61snTUvT9appu4Y0LU23rdD61knT0nS9atquIU1L020rtL510rQ0Xa+a
tmtI09J02wqtb500LU3Xq6btGtK0NN22QutbJ01L0/WqabuGNC1Nt63Q+tZJ09J0vWrariFN
S9NtK7S+ddK0NF2vmrZrSNPSdNsKrW+dNC1N16um7RrStDTdtkLrWydNS9P1qmm7hjQtTbet
0PrWSdPSdL1q2q4hTUvTbSu0vnXStDRdr5q2a0jT0nTbCq1vnTQtTderpu0a0rQ03bZC61sn
TUvT9appu4Y0LU23rdD61knT0nS9atquIU1L020rtL510rQ0Xa+atmtI09J02wqtb500LU3X
q6btGtK0NN22QutbJ01L0/WqabuGNC1Nt63Q+tZJ09J0vWrariFNS9NtK7S+ddK0NF2vmrZr
SNPSdNsKrW+dNC1N16um7RrStDTdtkLrWydNS9P1qmm7hjQtTbet0PrWSdPSdL1q2q4hTUvT
bSu0vnXStDRdr5q2a0jT0nTbCq1vnTQtTderpu0a0rQ03bZC61snTUvT9appu4Y0LU23rdD6
1knT0nS9atquIU1L020rtL510rQ0Xa+atmtI09J02wqtb500LU3Xq6btGtK0NN22QutbJ01L
0/WqabuGNC1Nt63Q+tZJ09J0vWrariFNS9NtK7S+ddK0NF2vmrZrSNPSdNsKrW+dNC1N16um
7RrStDTdtkLrWydNS9P1qmm7hjQtTbet0PrWSdPSdL1q2q4hTUvTbSu0vnXStDRdr5q2a0jT
0nTbCq1vnTQtTderpu0a0rQ03bZC61snTUvT9appu4Y0LU23rdD61knT0nS9atquIU1L020r
tL510rQ0Xa+atmtI09J02wqtb500LU3Xq6btGtK0NN22QutbJ01L0/WqabuGNC1Nt63Q+tZJ
09J0vWrariFNS9NtK7S+ddK0NF2vmrZrSNPSdNsKrW+dNC1N16um7RrStDTdtkLrWydNS9P1
qmm7hjQtTbet0PrWSdPSdL1q2q4hTUvTbSu0vnXStDRdr5q2a0jT0nTbCq1vnTQtTderpu0a
0rQ03bZC61snTUvT9appu4Y0LU23rdD61knT0nS9atquIU1L020rtL510rQ0Xa+atmtI09J0
2wqtb500LU3Xq6btGtK0NN22QutbJ01L0/WqabuGNC1Nt63Q+tZJ09J0vWrariFNS9NtK7S+
ddK0NF2vmrZrSNPSdNsKrW+dNC1N16um7RrStDTdtkLrWydNS9P1qmm7hjQtTbet0PrWSdPS
dL1q2q4hTUvTbSu0vnXStDRdr5q2a0jT0nTbCq1vnTQtTderpu0a0rQ03bZC61snTUvT9app
u4Y0LU23rdD61knT0nS9atquIU1L020rtL510rQ0Xa+atmtI09J02wqtb500LU3Xq6btGtK0
NN22QutbJ01L0/WqabuGNC1Nt63Q+tZJ09J0vWrariFNS9NtK7S+ddK0NF2vmrZrSNPSdNsK
rW+dNC1N16um7RrStDTdtkLrWydNS9P1qmm7hjQtTbet0PrWSdPSdL1q2q4hTUvTbSu0vnXS
tDRdr5q2a0jT0nTbCq1vnTQtTderpu0a0rQ03bZC61snTUvT9appu4Y0LU23rdD61knT0nS9
atquIU1L020rtL510rQ0Xa+atmtI09J02wqtb500LU3Xq6btGtK0NN22QutbJ01L0/WqabuG
NC1Nt63Q+tZJ09J0vWrariFNS9NtK7S+ddK0NF2vmrZrSNPSdNsKrW+dNC1N16um7RrStDTd
tkLrWydNS9P1qmm7hjQtTbet0PrWSdPSdL1q2q4hTUvTbSu0vnXStDRdr5q2a0jT0nTbCq1v
nTQtTderpu0a0rQ03bZC61snTUvT9appu4Y0LU23rdD61knT0nS9atquIU1L020rtL510rQ0
Xa+atmtI09J02wqtb500LU3Xq6btGtK0NN22QutbJ01L0/WqabuGNC1Nt63Q+tZJ09J0vWra
riFNS9NtK7S+ddK0NF2vmrZrSNPSdNsKrW+dNC1N16um7RrStDTdtkLrWydNS9P1qmm7hjQt
Tbet0PrWSdPSdL1q2q4hTUvTbSu0vnXStDRdr5q2a0jT0nTbCt1L666++qpP3njx8EvOffLT
z73gZif6U292ooH5kT8tLc7P7nXus88979Knn3fx08694EnnXnTqfS76jnMuvhgORJ1571PP
fNhDT33Aw04965E7j3gEnt7/DLiNMb5PePKIiy4999QLLzr34nOf/sRzH3/JuRdfAucZ51xy
6dPwaE1+iSP85O+WLTeKtYp/Lu9ccMF55z7honMufeL5F593wWfPv+Ccp1147s1ODJaVL6Px
h+nCwIdr15+P5/jrHJnYcj7lr+jmp9PDeIQRFmARxrj8MjY3hqGWsZbBltGW4ZbxlhUsazge
2uVjs4ZjDccajjUcazjWcKzhWMOzhmcNn5vDGp41PGt41vCs4VnDs0bPGj1r9KzR53fAGj1r
9KzRs0bPGvmbGlhjYI2BNQbWGFhjYI2BNQbWGFhj4GtkqYysMbLGyBoja4ysMbLGyBoja4ys
EfgagTUCawTWCKyRv5vAGoE1AmsE1sgijKwRWSOyRmSNyNeIrBFZI7JGZI3E10iskVgjsUZi
jcQaiTUSayTWyN/0LEPWsYaVrGEta1jNGtazhhWtYU1rWNUavpotX3+ua3PdSQGTBCYNTCKY
VDDJIOvAZiHYrATrct2sBZvFYLMabJaDzXqwWRA2K8JmSdisCZtFYX1uc5aFzbqwWRg2K8Nm
adisDZvFYbM6bJaHzfqwfX6/WSE2S8RmjdgsEptVYrNMbNaJzUKxWSk2S8VmrdgsFpvVYrNc
bNaLnc4tWTE2S8ZmzdgsGptVY7NsbNaNzcKxWTk2S8dm7dgsHpvVY7N8bNaPzQKyWUE2S8hm
DZUzWVaRzTKyWUc2C8lmJdksJZu1ZLOYbFaTzXKyWU82C8pmRdksKZs1ZbOobFaVzbKyWVcu
n9icoTZc1pXLunJZVy7rymVduawrl3Xlsq5c1pXL5xWXdeWyrlzWlcu6cllXLuvKZV256fwy
nWDKGYa6ctM5ZjrJTGeZ6TQznWemE03Wlcu6cllXLuvKZV25rCuXdeWyrlzWlcu6cllXLuvK
ZV25rCuXdeWyrlzWlcu6cllXLuvKZV25rCuXdeWyrlzWlcu6cllXLuvKZV25rCuXdeWyrlzW
lcu6cllXLuvKZV25rCuXdeWyrlzWlcu6cllXLuvKZV25rCuXdeWyrlzWlcu6cllXLp+cXNaV
y7pyWVcu68plXbmsK5d15bKuXNaVy7pyWVcu68plXbmsK5d15bKuXNaVy7pyWVc+68pnXfms
K5915bOufNaVz7ryWVc+68pnXfmsK5915bOufNaVz7ryWVc+68pnXfmsK5915bOufNaVz+cr
n3Xls6581pXPuvJZVz7ryk8EmxA2MaxAjOcrP2Fs4tgEsolkE8qyrnzWlc+68llXPuvKZ135
rCufdeWzrnzW1dT/8FlXPuvKZ135rCufdeWzrnzWlc+68llXPuuKIMl/u2wnjGfHTDY8Zubg
MTMgB2YC5JN4Pg/nU2kmRwZH5kbGBmuoB4BPkJ+VegD4ENQD2PcegOtKbwqPQP1oQH0/dQ74
q9CPY0L3YZx6eXCNY7QWcOvD1B2CK6SEntaAftDUT4IrjSHhbJzSXA8nzT6MPSg3TF0z1+G8
ldLgR/Qtph4jXMH4GMLocS6aThtdb8CjEJJJU9fTdb2PKQyoOpqpHwpXSGjFgFaYqXvpugEw
Dg58MWnqOcGFMuCJXsbUc3LdCLqiGzWwGfnkBFdEfwKncmMmplvXhd7jXZuIdzR1/lwXTQqg
OuqOU98Krmh6dFZx7NJNcl0aBnyaOBvj8Pk85zuD9xtCQI91Qpb1HVQ+gNEB/Z7SL+3QsTGD
GVKI5S36DsRK6Hui61H6mx4fTQIVe4tWTN0w3w3oOOKDMAEYzedYj/eYfPAhGLyx/Jl6vKHY
pxEVzdSnQiNi8CmCeyb1U1d+6vHyj/CaZ6gZzDAChnjF6ZtFK9B+fGExpakDgoOZMETQP+DL
mPqf+AzxZnp8QMGWzje+tBFfjwGHhjT10F1nIySBT61HXyO/rO2gPnzXBm+/n7IL240QF5IP
yM1MX62FJvCh410P+HTym7QdOo3DgDcO7E/dWdOlFAw+/DEM0yeB1BfiwHdkKKApj+kg9SGO
Af3k0pU1XY/OE3IPiD5OWYHBnwZeHj1efNxTd950+DbQPYzJjlOWlDp88HhtfNUjRJ1TMLwg
Go62JhA5v8XUjYMZY4/+gYkxwz3hawwjuoX4bBDNDyJ1Hm8Zn30IAHHuyiX84ZkeXxpVDl3n
KOQZIUX8eQ79kP+oUgfNQjX4LvCb/NnELuHzRa7jPT6b3AmMHRoQ0amjnIfcg4lQCb8yRPIt
8sOJ+OQN+qzGB3y0uVcW8UeFP/wBLcG3mbtEscMng74lDhaRrvBtw4U/f3wV6G7g74N/aRF/
/mgihJ96fBvT4dEAnEfwtwAN5i5JxLeYcDrIQoWAc0WICsdI+MZMKC78bRqcufoh4tTETyLi
Dw39lojTFP5ccqcxdGgPemT4k4Lsc18TLv454ctOOMfkbnLA3zFOB/giIMTpzAEX3g9OcgEy
gCpweLgMvuz8WSXEZxdOb/jbQH8RX2TuIrL3I2v3M8CpXfAT/AQ/wW8V8MuZr+An+K0F9AU/
ZX5I7gQ/wW894cc8DGne9WR+TCz3lPkxi1Tmt6EZrOAn+Al+GvbUsKeGPdciW1vlMLLgJ/gJ
foLfiuC3PsOe02U6XfLb0KRuN4wU+8Q+sU/s2zr2ab5Lu/NQdgOuVcQIfoKf4Cf4CX6HH/XU
Jb8NzgwFP8FP8Ntq+E2LDFaz0uHgRz13N99lYphWOijbW84YBT/BT/DbavhNq+JWA798S5kG
VzrsebLnVFHL/DZyLozgJ/gJfoLfioY9BT+tcV+f7FLwE/wEP8FP8Dv8NT9lfrrmp7ub6e5m
mZG6u1m+TafubrZedzfTsOfytS49n7JTZX7K/JT5KfNb28xvnye8aLanMj9lfsr8lPnpvta6
r7Xua70+1/SuL8NV5qfMT5mfMr+1zfymfR6u79aeWupwfSDYxt8LfoKf4Cf4bTj8dM1vG+F2
fe9Z8BP8BD/BT/DTbM+NXMt3XQAU/AQ/wU/wWxH8Dv4OLxr23JxrcNcFqv34neAn+Al+Ww0/
DglqI3dt5L59EBX8BD/Bb6vht+fbm/WZmkMYbD8E04/O2YO/w8s+L3U4zCJ35prY3tY458M4
OJfiMG2PFMZ+GHWHl/WBqOAn+Al+gt+Khj0FP8FP8EtjSN6YlAz7TkCst6FH18j14+DZW6Or
tykNfrQxGPad6ArGxxDQf/p8VG8chiRCMsn4Kaj3MYUBVUdj2PtEvT4kF9JgvTO2uAbnx+Ac
jz2WNgwouwEx/Vheb3SD4IdP0Hcx+BS9dSb1hldupo8xf5bX/PCd7vCiO7z0xoe4Xnd4WeVS
B2V++3H97WgcE+BwVEZ+tBGLWG0cfChscEPoxzHZoEXuWuSeGSn4CX5Nwe/ghz35ihr2PBqw
WvVrCn7K/JT5adhzRcOemu2pYU8Ne2rYk8l0Ggbk0b7vMbibxxJ9ZzDMG0KwLrqU82vfWWcH
B68zCGMW7juH8cfBDCnEMrLrO29CsphV4J3tS8XeJJf63toxpTyU7LvBjsjbBxNcMjmj993o
kg8eKVt0tkSFPvZpREWDYc7pFTXs6fJnb7rRjEMcg8WNrFIe8TVd70Z8Ixhux+emzK+pzI9f
R+x0h5dVZ0XbcDxlfsr8lPkp81tR5nfwE152Bz/2a0K3vJM7+3zwsCuJjk7SSof1SdhWxWWx
T+wT+8S+rWNfFPy27oYuh0JT8BP8BD/BT/DT3c22DoaCn+An+Al+gp/gJ/hppQOmhXhcCTDG
+bIGJPR+1EqHzEitdNB8l+uY76LJnprsuT7XDpX5KfNT5qfMb0WZ38HD7+CX+bH3o2V+h14/
W8ey4Cf4CX6C34rgtz6TPTXhZX0ytP0Cq+An+Al+gt+Gw2+VdzfTDV72C0YHfVzBT/AT/AQ/
wU8TXjThRRNeNOEl34vmmrtZX/NM97XWDV5cfx0TXjTsqQkv6zOcqsxPmZ8yP2V+K8r8Dn7C
y15v8KJrfusDqf0aDhX8BD/BT/BbEfwOPvPb3WzPa9/dbO/w02zP/YLRQR9X8BP8BD/Bb23h
t7vMb5UTXgS/g4bUfr2e4Cf4CX6Cn+CnCS+a8KIJL5rwogkv2tEI2wSFPoXeuGB9GAIHDmOH
Pa3XcsLLKjM/LXXYr0zsoI+rzE+ZnzI/ZX4ryvw04UWzPddnIo3gJ/gJfoLfiuB38BNednfN
b5UTXpT5HXSGtl+vJ/gJfoKf4Lfh8FvlsKcmvOwXjA76uIKf4Cf4CX6Cnya8aMKLJrxowosm
vGjCy2ZNeFnlsKcyv4PO0Pbr9ZT5KfNT5qfMT5mfMj9lfsr8lPkp81Pmt7fMT7M9NdtTsz3T
GJI3JiXDEQfkl96GPoy968fBc74UXb1NafCjjcGk4grGxxBG7z8fhZVGYwohmWT8FNT7mMKA
qqMx+abLrutDciEN1jtji2twfgzO8dhjacOAshsQ04/l9UY3KPNT5qfMT5mfMj9lfsr8lPkp
81Pmt7fMr9WlDprtuV/Xzdb5uLrmp8xPmZ8yvw3P/FY54UXr/NYZeMttF/wEP8FP8Ntw+K0y
8xP8lgGyzs8FP8FP8BP8VgQ/TXjRhBdNeNGEF07pScMQB+/7HtN68oU03xlM8AkhWBddyrNu
fGedHRy8ziCMc3p85ywKZkghljk9vvMmJNuPzjvbl4q9SS71vbVjSnkSke8GO3rM/DHBJcPu
Lo41uuSDD8HgYmaJCn3s04iKxk1TjXwXg0/R42VTb3TNT9f89nbNr1X4rTLz0zq/dc72ltuu
zE+ZnzI/ZX4ryvxanfCyymt+gt8yQNb5ueAn+Al+gt/awo9jGbEzMRnMU++HaJ1nmgcXlkuF
GPuAgZIk+K0zpPar7YKf4Cf4CX4rgl+rw56rhJ8mvOwXjA76uIKf4Cf4CX4rgt82DHsKfgcN
qf16PcFP8BP8BL8Nh98qJ7wIfvsFo4M+ruAn+Al+gp/gp9ub6fZmur2Zbm+mpQ5a6rC3pQ4a
9tQ6P63z0zo/rfOzAXcZD3m1oetwJ/LQm94Ga6fFjLgb+Yj7jhvP9Yy+3LPcRtzrHKsjexd8
vkG57ZLlTcwNljn2hudWa7sRd023ZuixJHG6Z7ntem9jxOrGAasgOS6FKGfiMGCBozdDzMcy
XUrBYJHlGIZpxaPpAu56jrWYhndGz2ssTTcaeMZgA9pS6vVuxMpL3FAd6yM5092azvHlbfJY
VjnkzoLpsOrSoRnJjjbfgz11WGCJ18aSzhF3a+fizIQXRMPR1uT76S2mbhzMGHvvRhOj51tM
WK4ZRofVoYNBNBuROo+3bIYxBI/WsRGpc8H0WJzJ27fjhu3ZZfGWU3Q+Dv2Ql3CmDrdxx+pQ
fBf4Tf5sYpfw+doe8yHx2YzT5Eg0IDp80mMYB8fDxy70/MoQybfIDyfikzeuR8WAjzbxO4vd
gA+zH9ASfJu2Vfhp2POghxTX4fU07KlhTw17Cn4a9tSwp4Y9NeypYU8Neyrz21vmp6UOGvbU
sKeGPTXsqWFPDXtigDoPjmK8u8cItMcQ6VjGS3nXP4P7+qUeg9DTqCrGXT1GrkcMyYZhGnvF
/fawvWe+Dx/uz5ePhbF0HCNhoNqE4qpf5M5mBYxLY5gcQ9wJW4aOZRpnHNKA4WcMv08bgQZk
xQ7vIwUMfmMsPFeMBkPceYQ4IT67sFvpgI1IcTwTLXsB6zDyt81t1KinRj016qlRzw0f9dQa
922G3JHeu+An+Al+gt/WwU+J39YnpmKf2Cf2iX0bzj7N9TxS8rPNfsFP8BP8BD/BT5f8ti4T
FPwEP8FP8Ftb+HH2yfXv6aDMb5szvCO9d8FP8BP8BL8VwU8LHTTZc30muQp+gp/gJ/gJfhr2
1LCnlrhribuWuGuJ+2YtcV/lsCeXGmLln5b5rT0slfkp81Pmp8xvRZmf7uypYU8Ne+r+Lrq/
i+7vsnX3d2n1mt8qMz/d4OVIE0jWza/MT5mfMj9lfhue+ekGL+sGpoNor+An+Al+gp/gpwkv
a38NrxaYgp/gJ/gJfhsOPw171oJhG+IFP8FP8BP8BD9lfsr8tNRBSx201EFLHTZrqcOer/lN
KaN2NNpIMCrzU+anzE+Z39pmfru7vdme4TdVFPwEP87ed+MYrXU+9qFnt4gubPNosQWl7VPf
F5eWOmipg5Y6bN1Sh1bX+Ql+23ANr/Y9KvNT5qfMT5nf2mZ+09bu9fu4R+3nt5HZXA0ABT/B
T/AT/AQ/TXjZOhgKfoKf4LfV8OOQYFwR/A7+Di+7u+anpQ41GdG2xAp+gp/gt9XwIxjWF367
G/bcM/ymiprwspFZoeAn+Al+gt/aZn77DD/N9kTXaFMzQcFP8BP8BL+tg5/mu2ws03bLarFP
7BP7xL4Vsa/VlQ57HvVU4qfEbxwNZUBUapkfP4ZoUnA9wTmG8snEaHrrXD8mG3kSQFQahjh4
3/eDH/NdU3xn/GhDCNZFl9j5tL6zzg4OXmcQNrmcRcEMKURj8spJ33kTku1H5x2WU05RvUkO
KystWpF43R/HGuzoQxpMcMnwLx6u0WG1mQ/B4M41JSr0sU8jKhpnyrFi8Cl6vGzqjW7wohu8
rMsNXnY332ViWIpYjdzjTwqy3+VKB13yw0lkt5nUusUp81PmlxEp+Lnc8TAd+nmD4Lcu8NMl
v82F037DVPAT/AQ/DXtq2FPL/DY2wzsSRAU/wU/wE/xWBL+DX+anzE+Z35Hgdn1+wU/wE/wE
v7WFn675CX7XB7kj/V7wE/wEP8FvRfDTbE/vMSvNRMsc+EgnXfnb+GwEP8FP8BP8VgS/9Rn2
1DK/rWez2Cf2iX1i39axb5crHaYlErq52UaCUvAT/AQ/wU/w02TPjQTcdY0wC36Cn+An+K0I
fgd/yU/zXdq4fHZdkGn1d4Kf4Cf4CX5rC7/drXTY8w1eNOy5wfN2BD/BT/AT/DYcfrq1Z6vZ
19Fsl+An+Al+Ww0/Jjer2s3v4Ic9lflp2HOvABX8BD/Bb6vhx6xI8Bs14UUTXozFNgQh3+kf
OzgMoR+xSUHQpg5jxH3gvenZT0aPQZs6pGmbD99hJwvsJOFjSpALPx3sXBGG6LDO19g+5K0l
XBewQ0WPXS+CtdPOFa7DDhUuGs/NK7yfPlYbbUrYCqN3wefNLGwH9Q0pGexp0Zu8V4btxhH7
W5ihx/4TY/4+bNd77KSBrSwGbHmRd66wHW7cPwzYzcKbIeZjmS6lYLCjxhiGaXsL04U04i7W
gt/aDnvubsLLnoc9p4pa6rCRYFTmp8xPmZ/gt7bw292w557hpwkv6JXudVix9XqCn+An+Al+
gp+GPTcWckeCsOAn+Al+gt+Gw29K4Pawl60yP2V+uuana36ZkdgPfhi9HbB1vK759Tb50Yfp
SqfpTHIOlx6THa3hNczUJfwS14uiG2PI19ETLjLiYiWuTybfT5c1UzcOZoy9d7gdcvS8rJm6
AZfZXT/geiiiecEydR6XOfHZh+Cx0y4H+1LngulT9AGXTp3jyF7qLC5zpuh8HPrB8Mp96nCd
enQe11/xm3w9NHYJ11Rtb7zH9dCRFTd9wouGPY+U/WyzX5mfMj9lfsr81jbz2+cJL8r80DXa
VEAKfoKf4Cf4rQh+rW7qoGHPTQXYF/O+BD/BT/AT/FYEv4Nf5H7wmR+HnAPWOmGMO4yDcykO
0/ZIYexxSUDb+a1Npij4CX6Cn+An+O16tqfg98VkWy3VFfwEP8FP8Ftb+B38Oj/BryWAfTFt
EfwEv62EX54KaXWLl7Wf7nnw4558RY17fjHUaaWu6Cf6bSX9eAoT/Fa91qHVGS9a69AKcFpq
h+An+Al+GvfUuOeuL/op82sJYF9MWwQ/wU/wE/w2HH5a6/DFQGJT6wp+gp/gJ/itLfx0zW9z
V6HvN3QFP8FP8BP81hZ+u5vuqcxvv0GyjscX/AQ/wU/wWxH8Dn7Cy+4yP8FvHeG0320W/AQ/
wU/wWxH8Dv4WL8r8NOy5V0gKfoKf4LfV8GNWtKptHQ4+89sr/KZbkiXvbD8Gm8ZdT/bUIve9
sqa1emKf2Cf2bTX7tmFLoz2Pek7rA7Et1RhSCm50IWqlQ2sQ22t7BD/BT/AT/DZ81FNr3PcK
iE2uJ/gJfoKf4Lci+LU66nlt+O151FOJ36bwUOwT+8Q+sW/r2BcFv7XZeWi/YCv4CX6Cn+C3
4fDb8yW/qaIu+W0kKAU/wU/wE/xWBL9tWOigyZ77lYkd9HEFP8FP8BP8Nhx+177kt/dhT8Hv
oCG1X68n+Al+gp/gtyL4rc98F8FPS+MFP8FP8BP8VgS/Voc9V5n5abbnfmViB31cwU/wE/wE
P8Fv1zd4EfwOGlL79XqCn+An+Al+aws/oih2JiZjbOyHaJ1nmgeX90OIsQ+2T0mzPfcLIOt8
XMFP8BP8BL+1hd/u7uy5ymFPTXhZZ+Att13wE/wEP8FP8NOw50au5VuG3aHPBT/BT/AT/DYc
fqsc9lTmdyhE1rUs+Al+gp/gt+HwW+Wwpya8rCvsDm234Cf4CX5bDT9mRdu3m9/e1/kJfodC
ZF3Lgp/gJ/htNfymyZGx99GFIY1hHNw0iyT0KfTGBevDECZEjqNxfW98iMOQfKbmEAbbD8H0
o3P24Be5a7anFqvvFb6Cn+An+G01/FaZ+a3PIvc9b+qgS357ZU1r9cQ+sU/s22r2rTLxa5V9
q5zvolHP1iC21/YIfoKf4Cf4bd18FyV+W7ew4VBGin1in9gn9m0d+zTdRVcKBT/BT/AT/FYE
v4Of7jLNzLm+m5tpocOhWY/KOO25zlEZ+dFGzOWycfCBYwLZFfpxTDbAz1FzusYxWtw+D7fM
6+eKISXrHaZ8pb4vUZgzlrwxKc31vA19GHvXj4PnoDkO5Xub0uBHG4MpL+iD8TGEEXflm6Mw
22xMISSTDCeXoR5mpSXMSkvDaEx5vT4kF9KAVhhbXIPzY3COxx5L2weU3YCYfiyvN7pB8MOH
6rsYfIreOpN6w1PY9DHmz/KaH74LwQyjt8M4f7O+662z+MJiSm7INX1nwhBdtAFfRigiwReG
iYO9Ddb68nVwdmA0fjCYNli+WhshiTQMvQs+v6ztoD5818YbVOcVJWu7EeKyZoDczPTVWmjC
xmiCG5zts7xs5wwmJAYfvBliPpbpUgomQF6YnpiDTBcgjiEKfiuCX6uX/AQ/we7amW4m3MQU
0Evwc90YnfXeWWOmG+TiEwq9B/LRu/TA5vRhRZOC6wlOzAwvrohzuwPdE87DkwuncXQlfN8D
8TMXAHucf62LLmUC+w7wGBy8ziCMFX3nQCFCIcTCd9/h7J8seIGm9aVib5JDf8OiFSmfzH03
gEPoBQADyWTs+G50CQQAtfDGSlToY59GVDSA3fSKgp/Ln73p0M8b4hhsAIgLNHs34htBpwuf
G1MNa9BlBHtt8vi4J+SbDt+GA4OTHW3up6UOHzzAi696RI+OH3QCbUFtCCT5fuJ76sbBjFhn
4EYTo6dyEr7GMDqoZjCIZiNS58F7dDxC8GgdG5E6h+UF6LGwi4dOXXZZ8D5F9E2Hfshfbeqg
WagGHRH8JncMYpfQubBYr+DRMRhZcVWr/FqFH7/a0KWI3nGPPynIXsOe14bBtgFS8FPml3Er
+Al+X/wqv1bhp8xv28C2m/cr+Al+gp+GPTd82FOZ325gsG0xgp/gJ/gJfhsOP2V+2wa23bxf
wU/wE/wEP8FPGxpt3bo/wU/wE/wEv7WFH6dw7eM+7lPKiElLmGCMKW6jwzSoPHkmGsxuyndB
TXHgXKbQYTI7ZkJ7zEozmOkM126yD8Ucvc9J8BP8BD/Bb0Xw4yk/dpgH60bc7hqzK8GMyYWV
Tphz7LEeaiz3w+YkaINpzqnHwhNelIuYvoqFSJz5jOU2w7SCD9ORsfIpT0vGdOUchfUzOEbC
6iYzoej64bfKYU82InSC39GD1qo6DIKf4Cf4CX4rgp9meyrzWx8oCn6Cn+An+G04/DTbc1XZ
0iYdR/AT/AQ/wW/D4bfKYU9d89sUAAp+gp/gJ/gJfprtuXUTdAQ/wU/wE/w2HH7XHvacJmgm
3iwQt7JLuH3wWFI6TN4ccJs53GN2uikwJrdosuemJHvL70PsE/vEPrFvw9mnUc/lk76eT3Ny
BD/BT/AT/FYEv4Nf6TAtftCORgJa/SRTwU/wE/wEP8FPw5665Kft/LSjUd58KW/mc8gPbeen
HY1cj62QAnZKLEvVsZbd9gP2VsLmjFbL/LTMrz4DO1pZqzI/ZX7K/JT5bXjmt8L5Lrq/y9Fi
1apfV+wT+8Q+sW9F7Dv4xG93d/Zc5XwXwW/VEDpaxxP8BL+thN+0f73Bvuojtm0X/daWfprw
sj7DjEeLckd6XdFP9NtK+jFlsIKfGUamRXFt4XfwqV9ZDahNHdZ+gozgJ/gJfsr81hZ+u8v8
rn3NL2qR+9rD60gZ3W79gp/gJ/gJfhsOv1Ve9FPmt1u4tB4n+Al+gp/gJ/hpnd/WZYKCn+An
+Al+gp/gJ/hpkbsWuWuRe8S9jrFJeMqL/E2H+xo763ofey1y365F7tN4qW5svZFgVOanzE+Z
nzK/tc38djfbUxNeWr/+djTaJ/gJfoKf4Le28NvdbE9NeDkacGn9NQU/wU/wE/xWBL9Wd3VQ
5tc6iI5G+wQ/wU/wE/xWBL+Dv7/Z7jI/we9owKX11xT8BD/BT/BbEfwOPvPb3TU/DXu2DqKj
0T7BT/AT/AS/tYXf7jI/we9owKX11xT8BD/BT/AT/LTObyOXM1wXgAU/wU/wE/xWBL9Wr/mt
MvNjrhm6qBtbrz0sBT/BT/AT/AQ/ZX5rD7PryvIO9zvBT/AT/AS/FcGv1Qkve57tOaWMusPL
RoJR8BP8BD/Bb23hpwkv2sz2cFndbnyCn+An+Al+K4LfNlzz05ZGuwHLOsQIfoKf4Cf4rQh+
Bz/sqcxPmd9eQSv4CX6Cn+C3tvDb3SL3PV/zmyrqmp+u+Z1IVI5jtNZhd5fQ82owXSEl691g
+9TnPWDgSmNI3piUDOWDIG9DH8be9ePgKVi6epvS4Ecbg0nFFYyPIYzefz6qN25MISSTjJ+C
sLVMCgOqjsaU1+tDQisGtMLY4hqcH4NzPPZY2jCg7AbE9GN5vdENgp/gJ/itLfyU+SnzU+Yn
+J1ofTfY0aMXYIJLJvdNfDe65IMPwWCjwtzt8F3AvnRp7K01bup2+C4Gn6K3KPeGg1dTHyJ3
JK75gZrBDKO3wzh3a3zXW4cXRYckuSHX9J0JQ3TRBvREQukhobcSetPbYK0vfZF+RN/E+MEM
yZd+jcUeeujVDL0LPr+s7ZJlR8d4g+q8pGRtN6JnZc2AvpaZ+jW2672NEe96cLbPb9J2zsRh
wBv3Zoj5WKZLKZiAvlUYpk/CdAE9oyEKflsHP/Z+Q5c89IK9GxP61yN1gwV8cUhDpJzT1GuG
C/s5ooMfsKsjNnmcorTMb+2TQeZtc/422DiO2stWe9mKfdrL9sSIHhK7Ky5YH4bA/kpEr8Ns
1162fNuCHz6EvSZXLdcT/DTqqVFPJX5bl/jF3WV+TAwEP8EPnwBRqUt+/BiiwSBIT3COuVNM
V8SgnsM1zYQBuOnDwvhdHLzve1zYnAcEcYkTA2/WRZfydUffYdRwcPA6gzBW9J3D8CNHA0Ms
VzV9h2G/hBEax3GaUrE3yeEqq0UrUhnP1KinRj1TxBX5oR/ygHbqcIEbqsEI9BBSHhGOXcKo
su2N9xgRHnl+jyuC38GvdKDuY2diMhiz6oeI2QjTG8K7G0LEzAT8uaQpgUsRcwJ6/ElhsF/w
28xsribTVOanzE+ZnzK/tYXfXue77C7xO8yoJ18QuaAu+a39SKjYJ/aJfWLf1rFvl4nfYeCn
+S41yVXLsYKf4Cf4CX4bDr89j3oKfshzWwbYF9M2wU/wE/wEP8FPKx02FnJHAqTgJ/gJfoLf
iuDHSV2xw/JLNw5YnBktVsdNLtzhAgsuPe6DMSYu6Yy4wwWm5GCiV+qx5pIZVsTNMnADCs79
wkrTYbqYh2WnuONFXo6KZao5CktHcYyEu1qYUFya73KkE7z8R85cBT/BT/AT/FYEv4Of7LnX
+S665ndkKGwLMAU/wU/wE/xWBL9WM79ptd4eVjoc5pqfZntuChwFP8FP8BP8VgS/VjM/TXjZ
FGCt8n0IfoKf4Cf4bTj8Vpn5aanDKgF0NI8l+Al+gp/gtyL4bcOwp+B3NIG1ytcW/AQ/wU/w
23D4adhzldDYlGMJfoKf4Cf4bTj8VjnsqQkvgp+2stV9rTM2tZtfvmW56XCXcYdNBZMdbd51
OWGzOGxr2OMW5iP2Z+aCt4TtA7ENIW58nnw/bViYunEwY+y9G03ELnI5arBhdLgb+mAQza0I
U+exgSHuQh2CH+LIE3DCsjjTYwtGbtiMLZqzy2IDQ93XOt/qevm+1oLfpgBrle9DmZ8yP2V+
yvzWNvPb500dDrPUQdf8Vgmgo3kswU/wE/wEvxXB7+CXOuwOfqvM/AS/owmsVb624Cf4CX6C
39rCT3d40Z1a9gpEwU/wE/wEP8FPN7bWja2xHfLg88X5zMWAXaATrr6PhqPfdGkjd23kbgds
HT8pwnea8KIJLwOm3ozO2YMf9txd5qelDnvNjja5njI/ZX7K/JT5KfNT5qfMT5lfdNZ7h3nl
zvM6OboH2I0F+S62TfHo306uiJ1WtNQhY1OZnzI/ZX4nhi6M/TB6j02bTLTUxCZnTZvw3pT5
KfNT5qfMb0WZH0/5G7Wfn5Y6bDDEBT/BT/AT/FYEv1av+WmpwyZkaqt+D4Kf4Cf4CX6Cn675
bd0wreAn+Al+gt+Gw0+zPVedNW3C8QQ/wU/wE/w2HH4a9twEWK36PQh+gp/gJ/gJfhr21LCn
ljpoqUOeus+9BOwhP3wXAnYW8Frk3rmhT71NfsTGDVrqcPSWOujenlpSsdeMUJmfMj9lfsr8
VpT5aamD1vmtD4wFP8FP8BP8VgS/g1/qsLvMTxNe9podbXI9wU/wE/wEv7WF38Hf25OvGLpo
sHNxGAfnUhy4T7Hu8LJ21wwFP8FP8BP8Nhx+q5ztKfhtSjYo+Al+gp/gJ/hptufaZW5fLIQF
P8FP8BP8VgQ/TXjRhBdNeEljwB4IZt71zXXehh63PXf9OHhepAZ1PaaKp8GPNgbDUXO6gvEx
BNwb/fNRvXFjCiGZZPwU1PuYwoCqozF5Lr7r+pBcSIP1zkzT8103OD8G53jssWzFMKDsBsT0
Y3m90Q2Cn+C31fDjH0dcEfwOfsLL7q75rXLYk2cvXfP7YrOuFuor8xP8BL+thh/BIPihgz0W
rGECyxDRwca/3G0G6XqHzjw2MRtdiLrm1wK4VtEGwU/wE/wEP2V+u4afMr9VgKeFYwh+gp/g
J/htOPxWuc5PmV8L4FpFGwQ/wU/wE/zWFn7Mw2JnYjK4MWM/ROv8NI5rMG8gxNgH22P4Ml+n
SxGTAvpojHGoMLm8w87rwaYjDHtOFws17LmRM0EFP8FP8BP81hZ+u5vwsmf4TRUFP8GP8zHd
OEaL7hW6VD27RXThWjC6VAO6WH2Zfek025OfTBqGOHjf95jTmu9+7DuD2a0hBOuiS3nKqe+s
s4OD1xmE8SP1nbMomCEFdFPzR+o7b0JCJ9Wxq1oq9iY5fOTWjvgCpoqDxZ2W02CCSyZ/Pb4b
XfLB447UuGN3iQp97NOIiugCl2PF4FP0eNnUm9zUQ+5pXVqhG1vzbGuNbmw9JE6+jt0Q8Ic/
39j64Jc67HPmdxj48RU123MVw45H+xjK/JT5KfNT5rfhmd80ermHYc/DwE/X/I42tFb1+oKf
4Cf4CX4bDr+JYauBnzK/VcHnaB9H8BP8BD/Bb8Phd+3Mb3fzXZT4YYz3aDNqv15f7BP7xD6x
b0XsO/hLfrub73Jt9u1ysudh4KfEb79gdNDHFfwEP8FP8FsR/HR3M93ac30yRcFP8BP8BD/B
b9c3eNF8l4PO0Pbr9QQ/wU/wE/w2HH6a77JfAFnn4wp+gp/gJ/gJfrvO/HTNb52Bt9x2wU/w
E/wEvw2H354nvEwVv+AGL4LfMkDW+bngJ/gJfoLf1sFvzysdxL515t1y28U+sU/sE/u2jn1a
6bA+kzKXgbXK54Kf4Cf4CX6Cny75bexa9iMBU/AT/AQ/wU/wE/wEP+yJNWBXAN64Hrs1DKEf
x2TDOBpOFqZLezrwY4gmBdcTnGMon0yMprfO9fi8Itf6Ikp7OvSBMwbwUQRsUNHjAwrWThtX
uA4bVLhoPPeu8NwfAFE22pTwqfUu+LyLhO2gviElgy0tepM/VtuNI7a3MAO2EDFj/vBt13t8
6NjJYsCOF7woY22HHduGAZtZeDPEfCzTpRQMNtQYsQ1BDjJdSOOIfTdMH5LLhzIdpD5EbPAW
0JZSr3cjdtnosZEJZj7w6NrTYTjsng7bsMZdy/yOlEmtmx8nHFdOT9iRKAJygp+zHrsGYb/L
vCkmT9y9B/Kx+6U3/Uw6wW/qDvkOxMcuSj6mhL4SyYBdm8IQXbTBWMEPuIxujCF3KBNoC2oD
1Mn3E99TNw5mjL13o4nREx+pG9DfdNgGazCIJoFT58F7M4wheKCZJ+CEncRMj12oAvoQLv8V
p86C9yliv7GhH/JeVamDZrENFr4L/CZ3DGKX0LmwPTZ7Rcdg5J9/3PDMj3+1odNtrXWdbxnQ
gp+GPTOvtJufMj+HHBsDGYMjWyP6fEzWgUkfhjy8EZFzG9eDmgFJ9eF289uGzE+zPZcBss7P
BT/BT/DTsOeGZ37Tar3lzE8rHbbuEt+hnBb7xD6xT+zbcPbtedRzguYXLHHXJb9DIbKuZcFP
8BP8BL+1hR/HIGOHy/EGkxX6IdrpQj1c3g8hxh7XNjGDSpf88AmsK6T2q92Cn+An+Al+K4Kf
dvPThkbrA1nBT/AT/AS/FcHv4Oe7KPNbH9jsVwa31+MKfoKf4Cf4bTj89nzNb6r4Bdf8NNlz
r7BprZ7gJ/gJfoLfhsNvldf8NOGlNYjttT2Cn+An+Al+gt+u724m+O0VNq3VE/wEv62EX777
Ce5Sptub6Q4vPe5ll8Zd00/jnq1RbK/tEf1Ev62kH09hgt+23N5sleOegt9eYdNaPcFP8BP8
NO65tuOe053Yrm+h355nvBxmlbvg1xrE9toewU/wE/wEvw2HnzK/vQJik+sJfoKf4Cf4CX66
5rd1t4AR/AQ/wU/wE/wEP8FP+/lF7efHySB5H9dDfvguBOwA5+0wYn9ZXkjB5n3azy/vYmg6
k5zDnrrJjtZwc97UJWwGpP38ePdN7GLcY19hP1hs9swPJ3a+x5aDgxtTj62FqaWIDQoHj/2I
R+w1GIbpap7DxpkQnMGjiZMLm0TiGAnbD5tQXPt2zU+r3PHFbOrQpzI/ZX7K/JT5KfNT5rex
kDsSvAU/wU/wE/w2HH57nu2pzE+ZH3ZwpgyIynGMFhuHYLOQnnOo6AopWQxXYPOQPo+TwYUd
oZM3Zh4cc53HuEcYe9ePg89rrODqLXYb8aONYVpzDFcwPgaMc/jPR2EvaSxADQnDHhwuwev1
PibsOZ2G0Zjyej3GQEIa0Aozjde5bnB+DM7x2GNp+4Cyw8CKwdDLdKjRDYKf4Cf4rQh+rW7r
IPgdKfvZZr8yP8FP8BP8VgS/g9/WYXfr/K691EE7uW/dKOehnBf7xD6xT+xbW/ZxEGkfN7PV
Gnd8vodCY1PKgp/gJ/gJfmsLv90lfnse9RT8BD9d8hsjZlN7XCycrhVGTMB2PcE5htkVDSb9
45pmspGjP+hXpGGIg+eUblx+pMt3Bpc4QwjWRZfydUffWWc5uzs4g7ApylkUzJBCLFc1fedN
SJgm7rzDpdUpqsfcelxlxTxxXHOdXIMdPa59muCSyVdkfTc6TLj3WKKAJRwlKvSxTyMqcgL5
VDEGn6LHyybMMqfrkEUOuaiVDli3wA/HdG7ABW6bPD7uQSsdhoC/DOdsq5f8rj3qGTXsubEZ
3W4zU2V+yvwylAU/lzsepsPUriHiPv8h2pSRb7rejeiOYJ4VOg2CX298iMNQVusNARPdZvit
zyW/vcOPAghdNFjTGcbBuRSHCaSYzoclsB49VBNzN2C3J2HFHZ2hVcFP8BP8NOy5tsOe+3zN
jx0ikA69H8xoD+gDoUsk+OET2ARgC36Cn+An+K0Ifgc/7Lk7+E0MSxFLoXpcScBo/94zP8Fv
E8DH9yD4CX6Cn+C3tvDb3YQXXfPbFGCt8n0IfoKf4Cf4rQh+23DNT5nfKgF0NI8l+Al+gp/g
tyL4HfywpzK/zbj+djQgKPgJfoKf4Le28Nvna35a57chk1sOB1fBT/AT/AS/FcFPw55a6rA+
majgJ/gJfoLf2sJvd5nfnie8KPNT5qc7vOgOL5mR2stWi9y3fJG7JrwcbghxHX3K/JT5KfNT
5qfM7/B72SrzU+anzE+ZnzI/3d4M5wHXX0fmtw2zPXV7s3XM8g7XZmV+yvyU+SnzW9vMb3dL
HXSHl8Od/LfdJ/gJfoKf4Lfh8NvzhBfd21PDnhr21LCnhj017Hl9w56tLnVQ5rftWd7h3r8y
P2V+yvyU+W145if4He7kv+0+wU/wE/wEvxXBr9UJL3uGn2Z7athTw54a9tSwp4Y913XYU9f8
tj3LO9z7V+anzE+ZnzK/FWV+uuan25vp9mYJOx97Y1IyHHEAYr0NfRh714+D5z0S6OptSoMf
bQwmFVcwPoYwev/5qN64MYWQTDJ+Cup9TGFA1dGYvrhCciEN2KvS2OIanB+Dczz2WNowoOwG
xPRjeb3RDYKf4Cf4bTj8lPkdLvPZdp8yP8FP8BP8Nhx+uua37aA73PsX/AQ/wU/wWxH8Wp3w
oszvcCf/bfcJfoKf4Cf4rQh+uuana3665qdrfryqmYYhDt73Pa5sslNsfWdwjTOEYF10KV94
9J11dnDwOoOwKcpZFMyQQiyXNX3nTUi2H513ti8Ve5Nc6ntrx5TydVTfDXb0uPhpgkuG3V28
4uiSDx7bMURnS1ToY59GVDRuutrquxh8ih4vm3qTm5ovnR7yw3fa1UG7OlzHvT1bhd8qMz/d
23NTMkZlfsr8lPkp81vbzI/dudiZmIyxsR+idZ6kgwuT5kKMfUBfMe35mt9UMfYOE/hScKML
UfAT/PrQ59TCdZhnmTDPcoDK+jLV0inzU+ZnA6behiISTM8NveltsHZKb12HNNZF45nh+jKR
10ZMAEa+3Lvgs5Rslyxn9hokvr1hYmFtN+JMZM0AuZlpIq/tem9jRL47IC/O6a3tnInDgJTX
myHmY5kO5y+DtHsMw5QDmy5gKjCyc9NjunDOuk03GnjGYAPaUurh3IdcHLOMkTEr87uOzK/V
a36rhB/lFbponPNhHJxLceBITOgwmX3APHUMz5ho+UlsCiQ29X0o81Pmp8xP8NvwzG+Vw56C
36bAUPAT/AQ/wU/wO/xmtocZ9hT8BD8Ne7qe4BxDHi5zHYbdeuuwij9hBI7jc5rwomHPgCFX
zG0acecGjo0ljLNivBYCSb6fRnZTNw5mjL13GC2LnspJmLcURodpUoNBNMdeU+cx0muGMQSP
QVmOvSZcbzA9ZinxVg64eUN2WYz0puh8HPohz2VKHW7pgGlSGILGb/KQcOwShpUtRi89hoRH
VoxrCz9+Etd/zU+Z36YAa5XvQ5mfMj9lfsr8Nhx+q7zmpwkvqwTQ0TyW4Cf4CX6Cn+CnYc+t
m6Aj+Al+gp/gtyL4rc9sz2mCZuKqWczsTbh98Fgu5mHy5oDhZ8w6nm4KjJmdyysddMnvaCZr
q3xtsU/sE/vEvhWxr9U17qsc9RT8Vgmgo3kswU/wE/wEv7WFH1Gk+S5aUrgXiAp+gp/gJ/it
Lfw02VPg2wv4WEfwE/wEP8Fvw+GnYc+9AmKT6wl+gp/gJ/itLfw07KnMb6+AFvwEP8FP8Ftb
+O3zsOe0OF6zPTdyFYTgJ/gJfoLf2sJvd5mfhj33mh1tcj3BT/AT/AS/FcFvfZb5Ra3z28hs
rgbWgp/gJ/gJfiuCX6vr/HRrzxoobEus4Cf4CX6Cn+C36zu86NaemwJHwU/wE/wEv7WF3+6u
+Snz2xRgrfJ9CH6Cn+An+Al+u878iFtt5L5KCB2tYwl+gt9Wwi/vdWcNttcbxyGKfqKf6Ld1
M2BEP9FvK+nHDrzgty2b2Wqtw9FKr1p+XcFP8BP8lPmtbea311XuWuqwdYneoRwW+8Q+sW+r
2cekKG4d+/a+zk+zPQ+FyLqWBT/BT/DbavhxJuSmw2+Vo56C37rC7tB2C36Cn+An+G145rdK
+Gm256EQWdey4Cf4CX6C34bDT+v81hVQ+9luwU/wE/wEP8FPKx22bgKM4Cf4CX5bDT9NeBmD
TeOu4adrfvuZjR3ksQU/wU/w22r4beeEF6102LpE71Cuin1in9gn9m3dqKfYJ/a5zrHjlxlo
4zgaGwcfqIzsCv04Jhvg59gIXeMYrXU+9qGfK4aUrHeD7VPfl6g0huSNSWmu523ow9i7fhx8
vrWG63xvUxr8aGOYbjUFVzA+hjB6//mo3jgMSIRkkvHTwXsfUxhQdTSmvF4fkgtpQCuMLa7B
+TE4x2OPpe0Dym5ATD+WNzi6QewT+8S+FbGv1d38NN3l0KRH5UK4mXSCH+g+Rme9d9YY5wvd
Q++BfBOB875wNJoUXE9wjmF2RdNbB7onG7mrGY6VBtw00vu+B+J5XrC+M4B9CMG66FImsO+s
s4OD1xmETVHOomCGFGLhu++8Ccn2o0PT+lKxN8mhv2HRipQ7FL4b7Iiuy2CCSya33nejSz74
EAzeWIkKfezTiIrGTd0O38XgU/R42dSb3NTchzjkh+9wmGH0dsArTt0a3+FN40XRIUlumN9k
GKKLNqAnEubPEG+mxwcUrJ3epOvwZlw0nu/Tl36NjegP4VPrXfD5tW2Hrhc6OgZvvzf5Y7Xd
iJ6VNQP6Wmbq19iu9/jQ8a4HfDr5TdrOmTgMeOO4f1fMxzJdSsHgwx/DMH0SurEnvk1+QZu+
yo/vMXQponfc408KstcS95sp81PmB3QMTEDL+VfwE/yGiBkQASAu0OzdiO4IRhzQaeBsB9wR
1JG9NkE2YUK+6dAVcWBwsqPNgxSpQ68D4EU/Z8RwBnssCbfRBrUB6uT7ie+pGwczxt670cTo
yfeEPkwYHbpMg0E0G5E6D94DVSF4tI6NSJ0LpkePheMbGNHILgvep4iBmaEfcr8mdeiwocuE
jgh+kzsGsUvoXNjeeL8tN/YU/JTpXRv2eWwTfzb5UZmfMj9lfhjhF/yYDIaeyTowSb5zSCIi
5zauBzUDkurE3mLsBqTR/QAMI4+3B7+PO9P82CGRM7hg0w8RV2SmVBZoH0LE1RkMlCS2fk+Z
30RNdGAw2ICxntGhS5SPFQ16OmEcnEtxYL8mdLiqg1ERj+EZg1EPuASctj8DwU/X/PJwrIY9
XR5yNp3g55hYCn4YgM+j6ti6T/DbRJALfoKf4KcJLyua8HLwmd/E6evL/PY87KnMb4MzWMFP
8BP8BL+tg980Upk4faxuhbtGPTclCRT7xD6xT+zbOvbtfbKn4Cf4aZmfVjpkbGqlQ17focme
R2W+yz6Pek4TZXTJbyPn7ijzU+anzE+ZnzK/Xd/YU5mfMj9lfsr8lPlpmd9RXumgzK/t1QQt
g1KZnzI/ZX7K/FaU+XEAOHZY/e9GQBE3VMHquMmFmxviXjseSwLHsj6Q9z0yuLNR6nG7nWkV
oQu49yBvdoSbDA0T1nDHIdzsMN+JCHcoysfCXYNwjIQbGppQXPs22VPDnprsqVt76u5mmZG6
uxlPwLrBSzNr3HeX+U0MW83dzTTs2XI2V9M2ZX7K/JT5KfNbUea3ccv8lPkp81Pmp8xPmZ9u
7dne3c2U+emaX022txyrzE+ZnzI/ZX4bnvntedjzMDd4IW5xwzPd2nPtlz8IfoKf4Cf4bTj8
9nx3Mw17athTw54a9tSwp4Y92xv25PSTfdzUQfAT/AQ/wU/wE/zag9/urvkp81u+1qXn03VS
DXtq2FPDnhr2XNthz91lfquEn675bQo8BT/BT/AT/PYCP24wvyZ72Qp+mwKsVb4PwU/w20r4
Gd55BIvVA/YrHaLotxf6NbGT++7GPfc83VMX/XTRTxf9dNEvQ1K3eOHZVrd4WbNbvKwy9dMt
XlaZfh3NYyn1U+q3lakfT2HK/LwZRoIhbnjmt2f4TRW1p9HaL+o7HGQFP8FP8NOwp+CnPY02
EnCHg97sE/wEP8FP8Ntw+Oma33zC1+M194MT/AQ/wU/w23D47XnYUxNeNOFFE1404SUzUhNe
NOGlNz6s2YQXZX7K+K7J+ObPQpmfMj9lfsr8lPnpmp+u+RkbB5/3X85cDP04JhuU+SnzU+an
+5ut6/3NlPnN2Y4er8kAlfkp81Pmp8xvRZlfyMsm+tS7cQgDtk4fcz86dr0NvQ/eD7Yf07Q6
3vf9YAY3pn6wlnSKnQuDd3DZ3oRhWr7uDFIybw0eTZxctg84RgrJmVBcJiaDbns/ROv8tHbD
4MVCjH2wfUq65ifoXQO9+bMQ/AQ/wU/wWxH81mcrd97hJ3TJO9A42DRq1FOjnhr1jM56/EkY
M3Uh0TtAn3XUqKdGPTXq2d6o5z7f2Fpr3DXZU5f8BD/BT/C7Pvi1Ouq550t+gp/gJ/gJfoKf
4Leu8NMlv/kylx6vufSnS3665KdLfrrkt+GX/Pac+U0Vv+DWnpx0E7ponPNhHJxLcZiuH4ax
H0bvcQ3RRMscWKBp+zMQ/AQ/wU/wW1v47fM1v8PAT5s6bArUBT/BT/AT/FYEv4O/5rc7+K0y
8xP8BL8+9BxJJz1DShbLc7CepufuznQlrO/xxqRkqDt4PNb5YFzA9ePgKR+6eosFOH60MUxb
i8IVjI8B63r856N6g5VAISQs8+HyINTrfUxYQ5SG0Zjyej3W/IQ0oBXGFtfg/Bic47HH0oYB
ZYeFRAZLjaZDjW4Q/PCh+i4Gn6K3WE2FJVb8cPLHeMgP3+nuZrq72XXc3ezg4Tet/NMyv00B
0kG+D4JqOHWBf5d/7AZ8WFx+T/68+tB/n7uav/sY7aZLv2cs/x0DW64yHefyj12d6+WQa/04
odSZf/E1d+Qzvv5kPCZtKi8/Zud1/HjoAq97o4cvLlmcu3jy4un4eQE9tJtfsjgHnsfDzlk8
Db95/MIshkVYpEWPn4g4cY44xD8fgY/H7iw86uHZLS7GMZ6AoxyuVofXfRJ+gzjaLc9cXLR4
BjyXLp4Krz3ktbvFUxYXLs6bow99/NIdHO0C/J6vdxFaf+niiYvzFxfDc8HiP64+Hz/5ji7E
7/Fax8+li+fjHHvZ4rLFqSzdoDze6FmocRE+oWfgWDnu5v3CISbgszgV7TP475rHYT5SK4/H
XoxP8fPf7MpadUw+0s0Xxx1GYcccxrfsmn//5ctOPP8U/6qu/Mi33/L0L/xF9i8W5mXF/2nG
HdV/d8ar36KiBW9C7A7sdbDjc73TT39JfpzOFvjr/dglKJe/gV0/5kOUH6x7ff9Our6AI/z+
+BvyF/P39qilqAfm59ecj+bzEt3dUlx+eutDHSgfg3/TR/L5X+72+92fuFM+346rr/7LY79k
cb+LnnHphWeec9E5Tzv3knMv+gp8hYd+0jxHz/+ueSs3Aiq+rLiXI+bIL3ycuPKFvmtKt8pP
D/8p81cnXc7v5rralQ8w/zjkj/a3PvGge/zWJz5x9/nXh5bxR3n6YnEqbC//2Orp328+/Oo/
ufqTi5MeeN8H3Dd/73c65k5o9X9b3Htx7A34jz+Pxb/jbngc/51wwxsef8Mbn3DiiTc+4cY3
PvGmN7/piTf5kpvc+MY3O/lmX3Lzk046+aQTb3qLW97ipFvi+Uk8yDGseexxJ6DiSTe58U3g
rfx39ccXJ59w7Kfw3zEnL25w8jHHnnzM1b+8uBWa+v+39yVgTSRru50EgktQIiAgihG8IDgi
Mew7I4jOISKGiAoogoRN9h0VgswSEAOeUQcCAhOcgImCKHtEo4PAURYRIrLKIjthURCV7VYn
MuPMmXNmzv//997nuY/RpKtr+er73m+pqu6mGkLBZrosB4RAosTE0RIrQam5FAJCoBBopATg
GY2C64BSrJj4ui14C7sTgWjpXbEXf2yUUSZ8ebDANehBj6zKbpLEVku3v09qn5uKAxTW/4a0
sA8EEuTLY+GCXzsFJdgtCPxSG4QB3SCxKCxkBi1epwpbfP75jMBnBD4j8BmBzwh8RuAzAp8R
+IzAZwQ+I/AZgc8IfEYAWnO6TaCaQdF8yVI1tFZ4Z26g6fsE/+6QD6fKA7tgwbpZlJvpyi8/
88bM/MTi9hucN3ZK9ueWoPhRs46keZcVbYya+Wbbq7jW/S+arUv8Ot5bVs+g23TrNo94jST1
p2S+hIayvYZGB8ODYhLwb16tSfBhlnYxS9lGla8U/k+Aj0pzLNT+sEEvn8zIaWUa1Bjv2P+c
PzLgdprf+MEzsysqLkOFSqDzahQqXeDuD6eywq+nxk9sfHCvi+vgf/kDy4hcPSthVVEQZra+
TieiSf9DHLOr5Rlf8CgksirGJaS9eXgioCgqIafQdjNVlwrT+J/8vNa90lWSU3dVSdOpXyf6
aPTttZns/iezqoK2gXL24C7JZnNd0iaLdPNddJeaj/2qKkfydB2bvXdEbxoZnmxYSzX0Ffg6
K3X1B/bJZyYb7hCkkd4Ve+e898AvIJr8j2eXPV7Amz2ajQnwj49PrBxAmP/P8Y/IW2TWMzq6
7gdtYxnWmPp7+XLbalsL0sKiFtl3F6lvEMWduJc2rojbiORd1AO/9ivOZN+s9+WTpecJ1BDH
NsMnMSMTEWSFxe7h7FP8zedz4qdY+cNmB0ARw/AdMdTO7JHtDB0aLgnjv6jjXGrZ/LMB2uVX
av+tlH4Y/XnTkEr4lOY0U+2HTJcz9fmOuc87Zn4YbfCk278310ZWBqI/4BSZiHTUNrT5b/uS
78uoeFDelU/2edHs0E+omItjdbU0k95dGcp/Ml4DVHHBxEnTLihpI8XUyaLJ/8hP3Ifnp23e
plbOI0p/S+m/dPYVm5XCYKfQ6ATCU6X1z6bjDAqyMldypz/E/ZzKYHmzKZSI2tqpZHPEbVqv
ylmt7b7a9YTEiJqtL5vae5znQhpStvqEnFkI4c8X1p6r4lqZjTglLUGXzlWV7DabCalOd1FU
z6sLTAsX8PsP7OpM6aP+TvqVfRstLnNLfKNl24YmE1i4TbpvWbfpsmRiw0BO0hNoqKT4+hLk
YGsf0WSwMLkm7fTfrIIXPHPeZ0PDLLbPhRGNhOy7+y1+R/M/xSF4ZKb8rOT9I7n5m67TQyPN
TT08fX33PL36jyVI83mEnXRDQ6k+FVKwXFGvet4u7fvE1yyDmhsVfszB1dpWpRP1+deQZ+n9
DRVRbPZEhYFUzj4/fcum/nWr3x5OeuKwuAvjQcTWpy5BVRaJL1hm2ifl66+oBnOlTSZ/tDle
ZNbfVWa7BJ1aHDLMrbgBNDHEHLPx+K7z4pGq8qpwv4mjmX2J1tWX4s645tYRpJV+Lxly7w6C
9v4ZWSKhK7Uy7mzFjzdKNu6srfYuXYICQtrbHVS+aZfh99l0A1Tv/f2+T3T8okY0dbgkt+D0
ZL6dw6U4l98T/OvnqMdtp4Pqk3RD3nFP/zDZNDgtUffy/mlymP/xMh2+yUl5KvSFZU38qCp7
gUzryr/UoJ8zqmE45jmcPf/k+wpCPSWGvd09Ku1QXxhdX/AQwawghtqu8gJGHr0Lo8GNygv3
fkerCmdF1sbOcmt2zfzgipfzTsLEbeM62cqz8g2tPORukh/2X8+pSm14HJ01zOTqVFoRbN55
SE8mH71pOZn5Nc9g5Gk7K9hbo8jsgf77IJRhuxOHOR3GGW+ozq+xuuArM3nfj3tMZ49b30Zx
f1b59sRGJ7LSulWfAiBGXSEBQWKVtua+JezmtnkTq8Ce9OqHwAlPeefOf+WZZ1xgNjcuQawo
ouTJnWqxTnR12aQ788HoXj2TljpsP95Qq9jr6obHZX1K9C+ntbhhnWnBYYJAK5mp1FSJel+z
vZojBA+rtLD3xDNszpNbxgHuUqsgJWOmfm3DNqobNpjswLlTQbxHclDnPCk8Mzh7T+VpUU4B
s0SxUfFFz1fbie0znRmEn6+hjs9I8Vhih2WkZCppbqUsxFW5PDt5Vlm1Vx9Sz46zEHJ6OHNY
uYQUVddQp7QoPf0+Tp2pH1gVeXKDn+dNmwmrirayAbr06wHM2WPslwVR2+ktKklV0BwxJFo3
o/yM11zja/ST8LHOeaPChrsK1E/kDRbL4EHwnZvVftwr91eV5y4eSQHoXb9ZUv/KYfMj26fA
TF/Olcec1YnZ9wFEQX6jw0M/ovS8XVImLtQuqLOmjnupZdNwehzuE6J/LSmh9LSN4Xt1jx+/
IshtvJ0ePE09U8z1HAm7UDfKd6Vlci2DqMHmu2ji0BqsNJlEo2c9rmeM5wGnI94LtI1ROI7t
JPjs2y+QZyxBJx12hJKDwtnpNVv3QLzzSOoKCC2uijjD46lC1VoeVk8unZatjX6o28hmm7DN
pnoWvvHLsaPcC8aa4pPGMLNeKbX7Ve7b0nQ6njlyq7ghfDO2wbwFZ6xkx+IaZvkZjbnGGakZ
BicmnrKdPm07ffHQVef4q21shobA3tWiXFUjsbLy/a9CS1Bx8hAGKczAPgzeqHYXFVoRdrtl
VahsXxEJDCbsrrb7tr1HmffVGcBPSopDigLKiGHzffjXAPpjjNnV4UOpggwz8GTCf/IRk4gv
MlFmPj/lqbo9/1LHoE1k+ALt6uigTx63qO7J5Toy2SA1tfZx/IobWQqQWC0JqxOY2m8TnBwy
XEjuYmse68E+NiQhDTVfMvmm7Op7VkFkAqESs8dcvDoQYYOgaq2SWEN1wYAEJA9BRylsNW0y
3nSdZOGIH0lgSe57HK0l2Txyky+gGPeZ3dK1bC8DceDS4Nw5MuX8RW0bkn1oPDqhUJtkUKLT
ntmTsXnNl/iO5+1vfZivwth6J+3nnA8tQUqPHhsHpryDp0EvyhSY/YQJdO1g4jIIajgIlSiC
FWSJpkv3o1t6juWl0C86iOZL7krNjUFmCem2NcBwO6XftUVdXzwS/wHF6nrW6NQfrZ7ZN3e/
1NCLzcjWrrUJ/3TustzLHx/RVw9xbLOL9IrklBPc+kyl1l5pSwu3y6/jHClyK47gD05jB9i7
qkO8XBHpkIQCJyghnCN4Zrx4zqiwfJVnfEVU3pmRi0e8dYwaR8aqBFJrTnkknusGj8/Ii6dI
VSa4UZHIFEgGA+HU6UxkyiQKcsOB+WG0wCwtSuXaFLpNJ6KHTFByionJ1W2K4gfWZ7bPfgAR
IN1D/03/FJpTrqjnEcW1r13M7TGT75WUzsqj6+rIbRPInh36MF9p+34uml+uWT1Zr9ZjZucg
uDLcE5UgWIK0A97F+ertaBlrkZ74OAFS6jYH9/zBV/QxP6DOyL06osFOnbDpewsm0z/dLFks
5G9i0zLHwbjv9ypaJ8F7ihn4OjPXcMzXWfZ958y9vDz+5PvXEi7LNP7tEVXXluZve6fXt+l8
yRJkabvijcTjkRnGhdDWiutlOrZ7h7FtuD259u42oZfIspfMNXdhbjrmLTgWl5Ke38/h2w21
Nh1pbO8qw/bYhmzIH9leYXKdbocsPNe9G5lnhHTBILt3Qy4H1pyFePIomiZCpVJuHSSPgpCx
VIj3rVGCy/oETvYFWaLpQdiIrfVZZyJtaxS9+HamzTaRVdHUduIhTj/elLQE3RZrZ0V4JHl1
S8qOzckGpuGVtCcXYtkh4bnzO8AAZE9B0EOL+yaOMgdf16sNSLRvy/mmbXvJfCNP0Yvrd59S
mhmxC+DQDeGgYBRPahkSMXExSN7Bkgx1ZrX9MC2n3NnGzqucZHjQJxLPIqYvOVg9Vu6XtbLn
K8TTb2Goy63+9VG+xVl3mDHKVmel1NbWKyPecB2efcWpu3CVQDRmTRx5LRhYi6SATzChyt3O
dReGqSzljrxhvqsHy8hReB8XlmkdTMJX2DzapD4xoNKYWpSdI1NJPFtunve3H7ZzD80cxOA7
rHjyMuLVB2BAOyRKIfyLtTgncG+YqgVODhjzesVAuJhFuiKiPCBLkLua6k58UlilDMax/kn0
Yx1yU31K9XdrxyQL2MyzeUqBC25DkhfJ7PfBk+lgdqTKJzxUNc6haju1PtcYpCh73DQ2O7HB
Y3dQ0oNmB9tv7FJkExvzS977diStrDy3n8U2U7QNor9JrDz94PIGjuycnkqXZFl8vwG0Josa
IRzTPkIFwobzk0CtNVe/L8zZHTzWMjifkPP1IggKQ73BVX++bEI8yWszdM70f+69vc+0Disg
v1p7qc3xOLnQ+1FwmbeBY3zPxASux/4w/TYm9oTsJeRUvUB7wsHENGuicayNzXl+LL02NKVn
L53zw9AdW05BVVTzdrqrd3rtgIVrilRnLPGFeCf9oTz94UUp9JjL7jBx1WQ9C73ApysT98qj
5FFKkGUgaqM5T1M/9tWW2H10KoRGBD7FQKsTA2vkh9CQOE9eipeTIo8OaQnKwDr13dIlXc/L
CFQa3/xCUZ1vZ6yRlHjWlNpKDOPQM4aRnswYXeN3qNWM7Q4RLd6Mu4HQAMe9DSzZgjqWIMnj
B04YEn03f5fLur8qe7OWm47PtrfTZfTpeku3t0/sJ8EYtQQx0le1Wo2S5/TU38WZyqNq1gao
/WLQkDmE5hT3uuGmdTWb04I3bCIeD79czoqMWftUafJf262oZK2i94fdHvvSNhDbS8qIx69k
3ogb2Hm8IrdML7+DXT4yuAsjKyOzx65zgzs2tRLlnkbuutqOz+wdHv8Qx3825Hs4O3pwxYTx
q3WLbO8LTwK5liHYeo3YNygFKRoKmQf8HZKpjon4DqeMCHwhjTWBKq237GNZ2oTH7qVqofUR
PbgAbESC2yu0Wi52k0VgC5S8GuQjAnvRhgiqEyIWYRPYu5qG2ghVBqGgxxrsTEpZUsSu8yXq
gsnqMclLI+wkb7V+XOuG86HBCTEuHkrsvCNJmWMSbGYelkzolpTTpWTkham/oYHKsqcYXvPb
S3z7ru13G1BZ2Tg69HZn4/Fv7GIP27Z7vp1Oa+yKb6iRr89jmK3vfBJTtx9x2TBNdoolMJ30
kJZWiI9//cvjNwiIp32sSFqaetpI0Zs4dEGJlf/GK6nMfjHiQ1zLv8cbzZ0dG75JHJ1VTlAf
3LU2pS0juYs/cfgZhZ/aQ3jP/vBldrWVLOQutfprBesVtZMSx9J2B81XdlxoU3s9+2bi1dqD
O1qf2VUpe/xkZufUku8QdYNvbITCRCBoVK0tiatWuJB51Cx5qSpzHssIDscpUtU0Jch8I5QS
L9MpVk39VhxPVdaCNiIC0KZaYryddyH8Uwyyr1S+d7XWSuoxqjkI05HI/RbddsMvs8N12uoy
fRyiZurE/1FyPc3QsWRbkX1wF5tBUVa5VDtZa+OBV3bIzpqOcxUcZoX5PW8cKRE0hWWSohkD
nmxlLw7WmKWqqlaYMJHAtHBTOojp7W9oIfQYW1zy1rTeryRN9c058uzGXK/aEGa4uZ2Tbl0N
1WvcsQ/KfPkWxW/nXA7EtQR7eI1TfAqsSCbhbrhBjpvXHYZXXvwE8aAk+VRa8+Ka26WLngn3
qA9D0r6ik7xfne61+HqhmK6nTXarIKxTWcm32nyeIthcZ8Pj7Mm3PX4nDHFb085BY1g0LIBh
AOmGawyKZ+XmxaekpFdWm59F/6Mt8GbJSF6t1QeVCesR+uRa83+nT8SDwrdVP1CaEgajx6o7
S6SrX7YhXkd1/shu0ztLYd7DjjUp1Zl+RQ85IG5FQ1vvJzA7yeQyKyN+mGAgrrlxrGP/wssK
hyMZdtOy/GA7q5SOO1X5/GmJHSSd/TOki+twByGeppiWOnAIY0TguBhPE7iTWjdaHE+TksEG
doA1sFsuJ3ZlrM2KENSmd7HcXnXuBE96r2KWC7AIKTRYqGtC1VSlbkRgt0SNDAaMzBTEz0W+
gqhCfn0V96dsOxmy7nAzyeiyQxK3QnsqIbgBe3HzDx+IQz/M777P4rp2neN/mGkmvxU4XyXr
aXDJ+Fnl0jwGxdeSb1SszvTqIRxanH5kf2Z+WCeDPlRx7GlTS4ynwKhFPbXlcF79k2fEUH//
pv2sTrweRZnik8Lw6hPwtRuDshtbGZ3EfKsdPiay00lkq6M7CvYkjDc+P8bdcKTI25Xb6EZM
72J56F5P9G+x53O1m2RqLe6DCwOyYfXnrmbHkItCQA17EqX+6R3LkXGbgPQmb98morR9lU8m
16Y3Je2yw+yB/GsvXk79jXSjgM0tLBbzivlZ8KiOaHovl51SP2ZDDCH5T+ynMCgD81UEm/2u
WJ/OnKaFb/xt/RbBRUxrZzuf56351kHl0zMdVf3ce3kaCZr7vea+N+pw+05me1PZ8M7s4vyz
GeOdrdPOXR0dHLIluaJdYbB7+7P4+D7plIxbmGxc/fb8GdtLU2i7sPJIt86f36JDRvKsject
0n1UbljzFKqYHW9os7bNChNHOfd5mKMZZNIUWk776Ok7aVd8+fPNlXFWpxV3Oy2KWb+uBZFL
55TRGcHITrt2WQoiL2z/7Uw3x3F2YtzKp4KjkUTG/ICLPLHiJ2uT9bOvW6Aq/+M57Y3HkjSC
Vho+0Z4LdIbNf4dhhY5THm/X+bcel9tMcfUarEiydD/OhoLInm+X86qgXGeVq+G11v7U2v5l
1736ade0S5N5GU3TEof/jfUbSxYNY4ZHOdY/VnbQZTsGuSbZlZt1yGQHp5ag62x2DoFgkJp8
OBFCMitR2+hKmygWTaxG5/tVBCsTj0sNjRL5OY2tTY7xKQmupoRX2xXbGJy5K31hyZ5VETXy
4p3i1eb4bjRwAGOoEw7/sXR9VAjGJhAlvWBe+RoFlU6K8RTvQlVQNXYtpKx/LpZ+F6p2UdZH
0HtT3tFKh3Fu323ZF4sJl+lEhW80olkpp91Gj8XSjanVUoZgIopPNgA/PMmnqhm493X3hzSr
24/W6TZl27KaRrVbKAIH0yd+5aFY7TqjH5huOk0KCUyCPJvhkXVxcGQJ6rHN/jAy2uytY8jw
76zYcP7yERZ//Qg7LdQxZ77iH9nf6PDjUxilVd5X2wJU6rlL0CodxtFC7VNm+3Ksr7Xynco8
9u2nd5D0tvfpUfLMBmzqjpRp105d6HxZUeGl5Nc2vbnJ6AdO03BI1Fe6vnUmh75wbDw+UzJN
rj/r3qbB1WX6cCsOzTwuGU20OTtUdmgoKmqzhW5x03Mv7/aoC8d+2O1j63zh0JV61k0T7rye
b5MfP+379ddZ6RTX0gSW2vieCImXntNRzugr9d9Z5ZTkNA0Lmrz5nJBH2o7MlEfaldYraLTK
L7eHWFN3KvFKwYIoSxpy2xiJnGh5EhWAYfYHtvdQ3Tecv7gETTQrVOXl3ddH23HoBZtv7bpA
lG4awDBnypagNzju2w+11pkQ3jvP8TbG55lX3ukwT059SrI3x31IY/CnkkGZ7g3sF1zT/OnA
fnuedseL4qE+P85FJdnX7y6r2Iy1ZbfyjycZxCe9sC9yO/5jxYarOm1+ZFtDil7wpthpBpG8
gYsPozE8Lts3GHoUxgX8SytFPWnnkubNiCMC8uLZLpklCBOau3lTfbCxhatWbm7WqguXHNls
ZgqLkte4BN1FDA+9dap95JCtE5zgdilmIkTpAsmHKF9JtHtmYN3ssOPJ5U425boYT77a3AlM
EjfBs0NktxQGQQc4bby9SsLcGEJR5al65sBcqS6SL1Ah67x48vQv162uPbAbmYw2XFHK28gT
f43KRaZgAyGwqi9fTRtCj4WhwsTxSji/akgvAlEuZpesp5al+uqNWEey3km5MAvXZPy4eCdS
JUteLAWSA81cVsajwMEcK72R5SIXlVdk8/7co9Bq9STqF8fKNgVPJB8vdJp6F7eN7/Binb+V
k3dO0tcxAUd9Sgg1Cu1dBcEthxOn8zIm1+7vfOzXKNtoEP/76/C/4tnE4R9tHB5t7konWXo0
8DZL3uB3tnj7NHdlVthP0i9V76V6gwtF65U9Ous9sug3Nb8dZ7qFqTJi7Ks3B5hcVT3HZ+gx
lVXS+SbRWfXjLPULT/C0jODnVsFggCOYwIJtfBAZiFqHhqh4A3Eg/hng8RORKIUeZcUsK5zf
7EXiSykt9JDibTQEJAZ/EeGyIvEN8H76RoSeeedosnKyzYpSiPSBFtiQwkla8yXQiTwIHcZa
GtQt9CxkFUSbhMjdW8ZleDtpW3lbed+KOyHfI7rFwlAQgj4pVmWJ30itDANBQgp0cgt8s4jG
5p1Ag9VSqsk25lvrtKfYFlcY8+Rj/QaZUlFHI9margY2FItnv0L029TapPY5B0Fbkh0l//UX
DZhob+4Cot8ShUNc5YY6cYIYFDbX2tb0cZKD9e3SJueJCgd9lsrXkdYzVlGB6wune3PjU+YL
nnRJyvk7hEU0QD7VVE0IXJcoBWsTV5UOtJgBog/nJj+wGt+8IgmCeFgl6G6sMoCmdAr4Ko8U
JqYX9cq+M1kYOsFc7h4O2FglJhAVItnFIyor3lan4i9CWqsTY6nK4ngeBjnHEx+ORZjj5Hjr
XKShe+bWyUrmMC2XlUnQAZsVlqvAdRFoDRVBx4WgqND3P6dosQXYJ7QL5GPsyAAJnfZ36ZYD
J5WuNDSRvZOcT39DeiwedcW3Dl9hf3Z4uA1R+FtsfjmT+G5YlT+nk3/rBWe+vWB2wGyH2RGJ
JwAlVVd86uBDlRvvUXf23ck//ohc2WjbMLfibWGb4tEoFaxM0yaK2YkjHc2P8GUUfFfe7TXR
BOOTK6hOJ+XCO9ATOCdkt2XysXReCqoacsP3ooc49G6wgNgSa2PtorUF263RDSZGYKZMxb/A
ILDwQoNiDNuRrJ5HBgJMqKRWQyE8KhaZMrR6AvxNCBqH2WOAiJULr5RsJD5V3YrZK58ysjqe
/iUWxhoqpdogQ1GbqGBeVk3TVMuSR0lvQoC5GtSPc5GBEPrIvlsbTyLkyc74Znlia4Zd7FE2
2yMlUYOtTFAunOhsdhgpnK4j9TxGDHsWO+t6J3CSHE/37zVxDFOOf8kOZ7+3Tv6X90f7247O
nTb62yHmPcLjhBiyc+zkbL5Ts3PezAiLPZpeey4osWHbiGSxdkt+Q0eOzCI7+y09a2baUbWz
vISVmvfqTerg1DDSaMD3cGIAO3f4mbhnWVB/ax3J1Pyizax4gstu6G4AkGMWec5cE99BggLB
ale8MhZrigQWxIW4d6Niy7eAI5M1IaV3EmPrgleWl+HBy2JwgSJFUwsN9TQly4t1oMLpyuYp
SFdLoAv9VS5ym8RAEW9jOZIKL6DBEhtJhVhi4jYrXNRjHbANSHmqMo60KWh1rLQ06NUSQX+K
VttITRFLGUETGpLxaVf68s7E5nGaHqfwElXZ7EEDWXoAhpLlzY1OC6yKiNth+p3djSVo11gd
x+mN8SvrgmtPG71pTL5SHv1OUsWBvLZtLFonEw8t3/n9xR4/JtA6fKJMXShfpsmGQom0RPUW
Vz3L9/Jmlaae132zvvd0+JvkoNaioNkeUsoC6aFZefazZ2PlwbJOczMhtdFP4/glOSUUQlDg
PL5hbtXll6lgOSzT1IZgK1s6Ifu+k0K4GpojL0qtBh6IWVWaEYEKkQtDBMZiQmVdxczxdCoY
bRGvNLotabKRwpsSWmiVFNbYGQvVTBzAOAIBz4bkeV9YS8EXgjEI2hh6bK9i2Su02LdDrK0Y
2xOYVbfAdUykpv4q163g+htJSVnTCEHv9ktIuQhac3Gu5jQUdZu8GE8JV0oV35dCL4CqOIXW
mrgWPUqEpSVqZWpGMBzyuuXrjS2+CbW0VuBp+3feP85uatQhm5SvmA45rZoWahV+v47b/pNy
BTDTdPLxLraB9V509++RXD5HvOm6ODremTnZqYqvF0T2zGe9LpzTTa/snHvTZFzxdO3B87pj
JNljbPXJQYe3aLvCHXaKxZ4MQv31PsIEUtPqH7UO0qauO9fwSqnHERYrqpcgZp4WuJl2brzm
a0swi9sqNwBBbrc0ob5ayDAgGd8hR1M7FSCepAWhQGyjqj+F8B1fuuKroM74Xg2/GsUsV/PZ
2KfQYWgtGFTASAMAzeCB0bsUXO5xgX2dhzHXNIwtFzMHI60YwJqKfQIC8CgPcgqn4js2jLBp
o0rdJ8gjUSTTyRN6PhkF2G4MwXjAHPWtOZqgBUzRE5jimZzESeqpgjv5IwXHmBT+3cmcN3tN
rmp+e17bSndoJuTdadLAGrYXMEXWvzZFCArylfRo9fVr7wsbXKWiMNuthDnCaumqOKYaUR/B
x5FvJATvz7jaMdmVQTCd9GKwrteF2tRgqe7ysYrqFUEGDinox6E61quux4Pj+sEMV6tTLC9O
a0qyO/UwDRu5yo16fhxakwxtU5rE80hI6DZaJVmNpmkEFOeqbGWHMLfDuCAsEGBwHY4lKQGA
AD6BSBfpkJXXMDbBwFKpB/DViYhKmbUBUClSGbZMECFCk7XAlUgwOwoTY5wEy1NLRDy0zs9u
4wj1hN5ww4pUtHRUmQB6eJ1RWndwJQ0FpYBLEmq4felIonNsHrfAkgLWN3zDq76O5d4e4TeD
H+KUWOfd2+7MXk86ctzxclASLkr7CCu+a9AhEs1bNrF/PiqFlScMlzmTHr+yJB3375lc7H5/
lRyuPTtwvhHfbkJe5W8dgatn9JVjevOl3GWRlecqE8pqzq/DDFcE0ckN4+Cq0miSd8pFRy++
Y0Yg/g32dlrx4OUATN8Pxu9iTc3vuUDqm0u3UaEI5LRYT7MMwlbLmCqOQsqjkBkuLjK7N1nh
eXIbjam8jVuB29FdSrtXPtQHNx3AuANCamUoWIUjuL3wVS6j2HjeOrTKrW2bEGdiEa7gDgD7
Oq3PHrUq35FOIrxSWdkcUEnKNJD9+mWZMUvlsdgJAvlYc+3cI3Mo2dgswITnkax6xoJQKV/3
pRb73m1J02Iu/8NNk7Iyh+/Mw4aLjfn4Q+zrZQ5DrAjr9LjnJSxmgmsqrTKIpSK13XPbP6P2
S87WSrI00U5a+qGrxaBP8Y4LzmVMfPx8UVCS+iD0nvhjQVhGXWpenY6DzzR/QeNV0cZDby9o
80cmLNvzp/nydu3+DkS7hoG4s3rDGWV7da0Cn1lcssfcaZbBnHu1HhFx7hHZWj3lNVgPa1oP
pk5edFRxcApguJ6JLb5Klq6Pj1V4NBr8/p5whWqz94s9Vk62Ac5dr5XHZ2UqXTCh4iNog0lx
niqCYhSbBOm53VIdiwCXPdBD8sn4p2uo4BJhljm4pcpbkxVSby4OIIZ4wG6RAHy8iTlYKkJQ
xsZ3KIUyy2hPsbTnfXfjFJqjGRaJXXmRrmIndMgOhoNKrqwJmjyWDkbzEQ2XtVK70BYEHmRT
HbAvhXqCfHaQajByn2DvWGTT4vSa1ruGo6g88z6h6HIdvoHf2PDSBDE6PB12g8S1wlqZXF+8
vYZGY+GxYIL8bz9igw8tBkcrNrce/UDZ6eUVn1FYZeqUcLHbewFd5qMzVneqetLhyRIUvXrv
69ANm8rueCz6WJFDrAd/3LO++ObdcQeClTMncZ+Eb4WzTlDmOYt7aQUO6ha3NRo2JjxR1rRy
OldZO40+PCVOi1Uwl1qdbHfE6nHf5WClKYWmXO7mzFfb9fkdgr27LpwMLZlM9tjAcWaDmwdz
pMelszxCwlAGuXLuwRXXSBdw5RvaCyHnHiACVlL1Il6jwrO2NuFKk22QsYk1WOieC9KtUk4J
Qr6P/RlnDialiS2WwWxT3PdhHbYbsqGMey9tGkqlBdrTrJPyC6zr/ZYrqvw7MkhJATco/cH1
19/RUidwJzHvYjO6IfWn5lJS9qm9W5JtEs7Eqrpl4Rm3MBpl2Axc0yGmNyeIL+uUF7MDnxzy
ovXo+TfSnLKyzYLGqvwz0xI3WU/bmpq4fjSmYV9iQ3oci+HFwtuAudiffhAPbrw4vd3Z5tHC
prsNR93W2fV4V4gzUxlv/Yq5pGeMnHPNSdvtblfgWsvSyv2dLaO9Y2bRIZ4lRa7xCf5NztcX
9atr424/L+4MBJ5jetCikTjiwZa81GIbgQ48TtOc1IxCvpLbMlJZ7eKU4L/H0imhDKlqEbTl
okPueWmqu5wGnWxz+tHh+2Fq7Zm0XResJlpeo+3YZZuUzzxwc3A46gWW2EtQyRvxOafQ7IHV
b0sXpKeQOvbRjNhL3jffcrol2nZEzCOim7yjGnhygvXcGrW2HeGZ1J3CX7X8oiYzyPa4T6Vc
S7sApArt2rL2NVtGH0EJzN4uumR6ZTa+QQl0FhmWtoVOgr1q+WUf7n15rbPMjHGWlzYz2H5R
vnaqd7Wpy7n8CZxHL9oNCpbqRps32EBiexVQ+iiD1yicP9Km5sZJy673Cd87BOzLhx5ySkex
EH+Uw3XgFPhxLoexdqmwq6rvR7mGhuvFCNr7TN8Pbec3efp6DXeWWOn2FRkP1ls0EbWb5MGI
mPWnyhJWMAg1Ilhw4i/s+Xtn5KB+ZcM9RJ93xYrWEsKhv/fXmRyT/rm7SOVJc9TOksL0kJbc
ZtIm1UDwgIr6RtkR3W/pN+v8vp0pm8wx65hRPCVw1NMnBRHajfca5vJJDvaHRvwt+2iEhF4L
1yz3FPGuGs1ol5NyOC4P/JRdtKGBBLkWWY3HUDVe7TYWd5rBBk+gcJavZSmnaxTEaxSohF6g
WePuNfqTKGNq/IhE6doAKYlkbMY58Pe9wzUHduMgSEGs9nU1REiVSaUSx3HEY+YnJXvWefeu
1Dlp30XPeuhDQ5dPkGwobKbY37RHQsGd0O2U60ktxupJEUbTc2s0rgqc/8E1Y2VybavTE6bH
hn2P5AQlqLMym2xczUr1LC33KP9lHGEwwZMXTjlB/TJ8m2k2AXqjk5F4ytdfkfGVJ2fG7qHL
tUi5hRV5dCMzLwdrb789J7ytxQXxw0pJi4yrVvjnHVOZgXH0sG8EOo6MCp1RwsbZ690WjR5e
rWXxTAGhf6s10ZCtMf80oR24xA2Ufr6JRfi8RXhseGzQ6mSnVyuSnbudx7tPypm8WnHRIcKq
RkGm4YQc7iS5RgFlggjakol1IDRLjiOxyqmxmHmrwxcxr0gRkmMrCpRZp5GDuQpTqNPQSWkT
C3BZiNC821T5e33sLvWM5C27VlY8c5HGX9yXgiVUG6AJyrfYA/o1OlELIyU7SOTQMBZB2dD3
VF10dvujlKk5/hmcw485Lxg+h9n9prfzZvXny6K7p9WLrPR70oMazClCg/vrP6jVV24654QJ
yn3o/D0uSpT8xrPxnDry0HXm9fnmgMvXwPMhEqz0+u88O0vaGO8eHNT3+2A0rPQDwUq3SKZ6
OH3f3ldlp7281DZUZEa/pI/vPb+n5Q6BSz59py23cr7G0PN5e54+ed1Fx+v3LRddPOTcrsVt
u7F+O72b24WD/3cYnJtATiAqelffRZszYsPvWjkPSdUo8sr6eJLdzkODF4k9kmOr/C1pZTxF
YMldsZLjD9MeKnZekxzPIkYrg2TrAHqWptiF8w+U1aN2VeMle0hnJKcklyAp4iRxCcIe9LMO
lK8bonpftbEZt2OwM+zABZF7Xec9X7499SF3IihiXoVmdOrUip5D7BkHtZI7m7ccu3x103mZ
8fYSIr4tpTJmIuU/t9Ff4EfaWFapIp7ktjrqkaXlpg95N5hx49+jau8PHaviGj33KnONEbTQ
jl4c7JzeecSHwGzjdjIF/0vl7wM/T/8AuLf1m8E/T3g3j9k409l29Pjiobpmx6mOhjGMV9tb
t29Cxxu8mW6zuKGSvDtOZ9t6D4JHa7Zl1iV7yDGj4raVQQXBeRbhDy4dQi9BNE3wPagxJd4F
QoRiN5fnbw4ws7LoBdh3WYRTu1Cncf4J/oi7W+5Xks7sjpCc1OsrVQVtFOf190ofVn2n2J22
8Ig4v+L7IKNzxCHg9Tet8NVaGK+KoOk+W2/uVVMBwUwrtLXV6OCiKtvzju3Ufo/+nwfWjCrR
W+MTivR8uKYE2jvrZpXGguym4eHOO94Mt4da20MsLV1VwLNw//VPY7hV9v13bY7kwRm7dWtN
wZorbdUSpPC0yYr0PD7l8rWAzmkV6yXob/nNrW+uTnRc38j/sLnIt2H+XvMdp5gOpmu01Ybt
L0z/frTf9dFYdFrKQu2G7XeKx6I1a5pdDcCVoc0q6NQ22aPpxwqiXr5xTME9vsBhZSgVp7/9
B3oktJjd7/SVRbq318IBTO+8rbr4+aerR10tzvrTdt6cEp9JlrhB77532yh2FLf2yKZuuecR
saMqpUp3TMxnksU6hiRu0EYkbk6JzVzsWHtY4ia9O4N791zUSykTfy+xmS5cxv1K+XqmUdxK
fpP0haEGl1Ml++/Y6Rf8xD0W893mUsObY843Tys223mbJeSZQaFt0xSPJej7G+wz2xJXjRfc
KvalmzK3Z8xMLTzoJJZvoyVso1V/YQ4/X/Lf/IgxXHMf2UlvuraxJYxSD5BXlPWoKK0x0Iza
eUszuLWY6XGToL347KDB6LSRG3lsD/Pl667MkcILOh9kWUuQtZd37ptOzgcZz/ynAnezuGLC
/Nvov9tfIEftKMl9q1P+1fxs9oe9e8qLJa6FBBWx8h+Pm0VonTBSe2YYOVbDee/XaNb88+H9
3/s1CsbOLwpaF649yIupzH37dn+x2aKOrUBMvj7bzraIybe+yrj3tbSgyLqIIjANG1ixVaAY
w6AYd8cuqrEaFAvn927ujfI7Vp4Zj5q3JS7OmK2TeHclbeGD6VZ1UIEePvQuWc1r+H5X9hKk
rLJ5iqj9usJmroaj+CXfyYtjegConJP/zfqd5PnikWR36bz8F63lrVNzOjFfSl4aLq6Irnrc
PDfUufDg9tXLJSMZirvYbu/yGme0/LIbBdzgthyi//s8m8VG1TXnoxNGR+Z9f/TO7Gd6L0xi
+f6NRONo0+KFhi8OHjS8GWV02/dNU13DINtdttXHKrtA/s5PRdaXtSQbsRuV//yJlP9Q0etc
1dIt4xTuUCLbmDEfeGq5BYt19+dd1tp5LDDMpqjHST4L4JlI6uESPwM7m9OxgdjH/+Ms/Icc
f67+GYHPCHxG4DMCnxH4jMBnBD4j8BmBzwh8RuAzAp8R+IzAZwT+ryAQs9S63A+8gS38oQq3
+fx0e2thWrgpLVzn/9yW2NDW5f5hHqhmwj04f+FJlCfiT8SjsOgPf/7NltiS9mAT6FDIHfyd
GrxBtTvYCtod/BGqG/gF266i/2AbbOzv6+HAptbuYDNmd9AqBGwnHQS3XBpG20ORwg2pDf+A
9j+3MQK1LMF21PC23H6AC3hjaviIg7ZBNuAX3rba4eNxL6QOwVR1hFtUwyXwdtWEj6XLaV9A
C6ZKhE4INwKHaQUAquGghyCQDgZyB4B/pwCfMLVd4B+85bU0Dk5rC9OHwPlO8BX1BJfoCvP3
QlFC2gc+oef2keNQ4UbcIR8lgCnjwddBWJ/0UToYJRxkL8TME8jpD7jwB5t5izjZC9p6gO29
cRBFqJNAoYZgrUQKqVh85NsL5JwAmIuw+gLUh6U5IdQe3O8+QPkkoAv3FvwnLeHNyf0B53A7
NyGVYNBmORemfUrIbQjgBbYTHODvBMg7BcFlsK7coR2gfxjbYOE5nEsB/2Au3T/Wgsv9hPVg
Pv2ELX9bx/Oj7DvARucngLw4oC94o3J30J9oq3IRrQAhb/B26rDViRCA8YKl9wJceQlzYXuG
+RPphiLkbtm+cUIKsMwiHcOWB9sxvGm8B8j7VHa4b9jCT/0uH8ZfhMantWGuQoS8f5oL13MT
1v5VZ7/t5aSw7+X+l/EVcQdvd35CiCfcBpYLPod1AeMY8lFKuA3M/TKNT/v3EWICbxsPIwBL
CksEoxMM9AbbSAhI/VavIp7dQfmvGMP+AFurK/gXKWzvAO0GeXA+rKtg0MOn/f6x/v7ZNuEc
kVSwVX2KERwNYF5Ftglv6w/rF5YT9u9/1Q6uvRvwKYpmsK26A2+AefQC/P3afi+0B1hkMJAF
7t39ow/oAcl2gdrW4NETka9bCSnA1gZL5wcouIHyYPAL0z4B0Fi2O5EXHwG0RF5HBCkYd1g3
Ip+F7ehft9wP6IsiF2zxsHZF3MK6gaWHY0PIx5glild4Ia+ieGf7UVu+oC1s276A2p9R+QLS
F9YUReFfo/myX4msCkYQRpXwMQre+hhTYE3AZSKPxwE5RXFgOVb8cxsSkMod1PMByMNWhAMU
QsF5ENAQXPtX7HYLqf0W3eV+fEFZMKCxjA4sZwhoDZ/DvhQGvrAvwvqB8XYHvYjGF9jS4X6W
kT4o5AbWEewPsE/B7eF2cK0X4IsHYwCMJTwe4cFLEvSEZ7fBSARj9tv2sGfCmMB+Buvuv0oH
jnGfjsh/jZd/PaKLIgccIT1/kcvgF6l0hS9+8IWWZbIXegrsaSJ7EyEIR41lvO0hK7D9/27g
Ib/V2Z+1hGvDvgWPp6IXTcDj7ikwxsNY2gP6sJZ+3x/cCn7xhijfDRzh9qIcXyFPcGuSkOsQ
oYzLfIrsIuCjdeA/6hhG1gt8YXnCQH8iruDXXsB9LI/XcLT4c2p+gLYvsGTRzAIe93Bg1mIF
ZjRwRIUjIwXIFwo8UaRReESEbQOWWvTiDpE9wl4YAHgPhjSFWPxVaWDq/oDSsm5gWZZt+89p
7Pq3iIgQ/qt4iGj9ET+f+rRobifykxAQA361smWdiUZsUawVeeGyPF8COWHNwRbwazs47S7U
I+zrFIA1HPdhPOC+PsVjz+/KRMhbA83AdhIg1AAciUSviIFHBHi0CP6ILkwNjhHwTA62uh1A
u3Bv8JgFxzF4TIZnwXBsgnt3E9a2ASmRFy3LB0d/2AbgnmAeYZrwTBW2JFG8sgUaFNkOnNoB
2YJxao+w3n7QUkTPVcjz8mi2A/TxqxS/xwDuAcYwSMgbjBJsl7B8sA+Ixgl4Ji/yItH8QMQt
bMNwLD0hxPFLICm8YoClhGdFnsIWDqAcTotiDDzmwJSXZ15/pMd9QFYRuiJdwyPCbzX2q8Xs
A6uTHYDz31o4nAvP2WGOYeyWdbUcbw8ATmFbEekBrmUh9FIv0JPI++AWotfmiGiL5rawtewQ
UhbFGNHs/xaIdDANeE4BextcF64ZDqQWzU9+XwojfhD0aSOsZyCMLIRfuIU1LZqvLo+TQZAa
4BaOPbBVwBzBXIpmE/DoEwm4hUtEs4pD4AxO/2rhu4GNEIWRdQeo/VfmPgcgMojAMJ9wJN8v
5BNe+WiB8U0fjAdwdP7NC5KEL+MA6zv4+N97pRFM4Z9fVLRM/59fT7Rc8n/7iIHtB9bESSH2
J0FkdhXazEcUfs/P/4MXE/3hov+TTAScRkLg7zd/+3knvLbx27w/OvurL6T5o7b/M3n//72Y
CPvHwGB+b06fnotpAeODnROYHkqU/r0RiqgOooT6hv43iuHmtw==
    SensorDataFile = <blob elided: 365386 chars, md5=6bdf4b68>
    Type Image = RLX_057947.jpg
    URL = http://relux.com
    VarID = var1
    Voltage = 0 V
    Weight = 0.00 kg
    Width = 100 mm  [stored 0.328084 ft]

note: [stored X ft] marks values corroborated as IEEE doubles in the binary element streams (Revit-internal decimal feet)

## geometry (parser evidence)
native form markers: Blend x2, Sweep x23
no freeform markers — native parametric forms only
